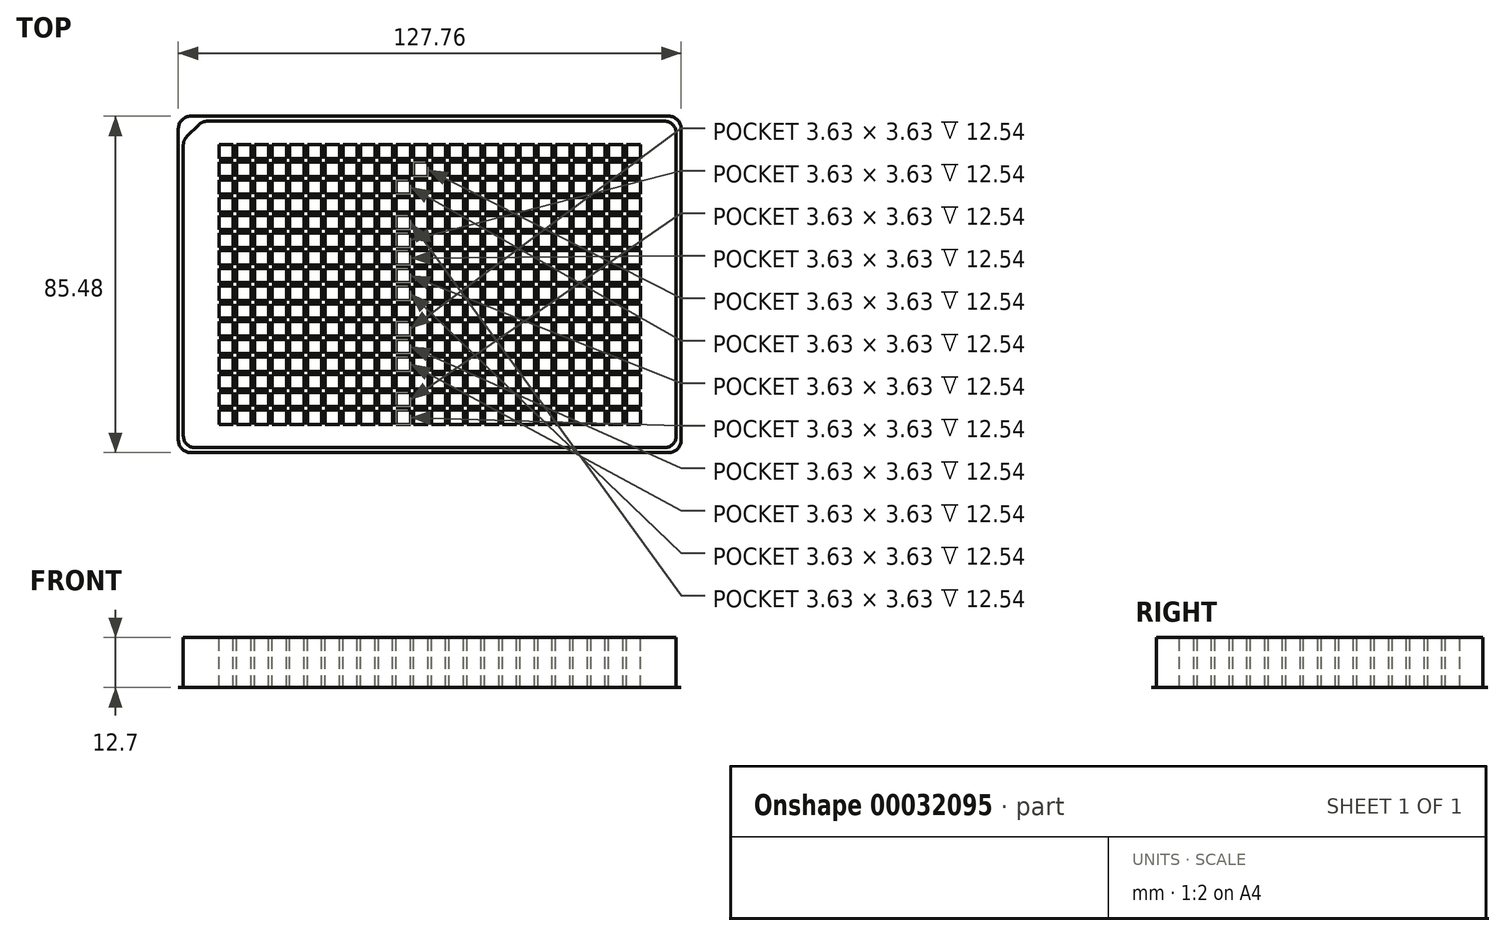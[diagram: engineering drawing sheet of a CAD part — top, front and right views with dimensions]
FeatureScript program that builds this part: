
annotation { "Feature Type Name" : "Feature", "Feature Type Description" : "" }
export const myFeature = defineFeature(function(context is Context, id is Id, definition is map)
    precondition{}
    {
        {
            var Q0;
            Q0=qCreatedBy(makeId("Top.planeOp"),FACE);
            var sketch = newSketch(context, id + "F0", { "sketchPlane" : qUnion([Q0])});
            skLineSegment(sketch, "E0.bottom", {"start": v(-60.7, 42.74) * mm, "end": v(60.7, 42.74) * mm});
            skLineSegment(sketch, "E0.top", {"start": v(-60.7, -42.74) * mm, "end": v(60.7, -42.74) * mm});
            skLineSegment(sketch, "E0.left", {"start": v(-63.88, 39.56) * mm, "end": v(-63.88, -39.56) * mm});
            skLineSegment(sketch, "E0.right", {"start": v(63.88, 39.56) * mm, "end": v(63.88, -39.56) * mm});
            skLineSegment(sketch, "E1", {"start": v(-63.88, 42.74) * mm, "end": v(63.88, -42.74) * mm, "construction": true});
            skPoint(sketch, "E2.visualSharp", {"position": v(-63.88, 42.74) * mm});
            skArc(sketch, "E2.filletArc", {"start": v(-60.7, 42.74) * mm, "mid": v(-62.95, 41.8) * mm, "end": v(-63.88, 39.56) * mm});
            skPoint(sketch, "E3.visualSharp", {"position": v(-63.88, -42.74) * mm});
            skArc(sketch, "E3.filletArc", {"start": v(-63.88, -39.56) * mm, "mid": v(-62.95, -41.8) * mm, "end": v(-60.7, -42.74) * mm});
            skPoint(sketch, "E4.visualSharp", {"position": v(63.88, 42.74) * mm});
            skArc(sketch, "E4.filletArc", {"start": v(63.88, 39.56) * mm, "mid": v(62.95, 41.8) * mm, "end": v(60.7, 42.74) * mm});
            skPoint(sketch, "E5.visualSharp", {"position": v(63.88, -42.74) * mm});
            skArc(sketch, "E5.filletArc", {"start": v(60.7, -42.74) * mm, "mid": v(62.95, -41.8) * mm, "end": v(63.88, -39.56) * mm});
            skSolve(sketch);
        }
        {
            var Q0;
            Q0=makeQuery(id+"F0.imprint","IMPRINT",FACE,{"disambiguationData":[TD([[makeQuery(id+"F0.imprint","IMPRINT",EDGE,{"derivedFrom":sQuery(id+"F0.wireOp",EDGE,"E0.bottom")}),-1.0]])]});
            extrude(context, id + "F1", {"entities" : qUnion([Q0]), "depth" : 3 / 812.8 * mm});
        }
        {
            var Q0;
            Q0=qCreatedBy(makeId("Top.planeOp"),FACE);
            var sketch = newSketch(context, id + "F2", { "sketchPlane" : qUnion([Q0])});
            skLineSegment(sketch, "E6.bottom", {"start": v(59.61, -41.47) * mm, "end": v(-59.6, -41.47) * mm});
            skLineSegment(sketch, "E6.top", {"start": v(59.61, 41.47) * mm, "end": v(-56.54, 41.47) * mm});
            skLineSegment(sketch, "E6.left", {"start": v(62.61, -38.47) * mm, "end": v(62.61, 38.47) * mm});
            skLineSegment(sketch, "E6.right", {"start": v(-62.6, -38.47) * mm, "end": v(-62.61, 35.4) * mm});
            skPoint(sketch, "E7.visualSharp", {"position": v(-62.61, -41.47) * mm});
            skArc(sketch, "E7.filletArc", {"start": v(-62.6, -38.47) * mm, "mid": v(-61.73, -40.6) * mm, "end": v(-59.6, -41.47) * mm});
            skPoint(sketch, "E8.visualSharp", {"position": v(62.6, -41.47) * mm});
            skArc(sketch, "E8.filletArc", {"start": v(59.61, -41.47) * mm, "mid": v(61.73, -40.6) * mm, "end": v(62.61, -38.47) * mm});
            skPoint(sketch, "E9.visualSharp", {"position": v(62.61, 41.47) * mm});
            skArc(sketch, "E9.filletArc", {"start": v(62.61, 38.47) * mm, "mid": v(61.73, 40.6) * mm, "end": v(59.61, 41.47) * mm});
            skLineSegment(sketch, "E10", {"start": v(-61.73, 37.52) * mm, "end": v(-58.66, 40.6) * mm});
            skPoint(sketch, "E11.orphan", {"position": v(-62.61, 41.47) * mm});
            skPoint(sketch, "E12.visualSharp", {"position": v(-62.61, 36.64) * mm});
            skArc(sketch, "E12.filletArc", {"start": v(-61.73, 37.52) * mm, "mid": v(-62.38, 36.55) * mm, "end": v(-62.61, 35.4) * mm});
            skPoint(sketch, "E13.visualSharp", {"position": v(-57.78, 41.47) * mm});
            skArc(sketch, "E13.filletArc", {"start": v(-56.54, 41.47) * mm, "mid": v(-57.69, 41.24) * mm, "end": v(-58.66, 40.6) * mm});
            skSolve(sketch);
        }
        {
            var Q0;
            Q0 = qSketchRegion(id + "F2", true);
            extrude(context, id + "F3", {"entities" : qUnion([Q0]), "operationType" : NewBodyOperationType.ADD, "depth" : 12.7 * mm});
        }
        {
            var Q0;
            Q0=makeQuery(id+"F3.opExtrude","CAP_FACE",FACE,{"disambiguationData":[OSD([sQuery(id+"F2.wireOp",EDGE,"E6.bottom"),sQuery(id+"F2.wireOp",EDGE,"E6.top"),sQuery(id+"F2.wireOp",EDGE,"E6.left"),sQuery(id+"F2.wireOp",EDGE,"E6.right"),sQuery(id+"F2.wireOp",EDGE,"E7.filletArc"),sQuery(id+"F2.wireOp",EDGE,"E8.filletArc"),sQuery(id+"F2.wireOp",EDGE,"E9.filletArc"),sQuery(id+"F2.wireOp",EDGE,"E10"),sQuery(id+"F2.wireOp",EDGE,"E12.filletArc"),sQuery(id+"F2.wireOp",EDGE,"E13.filletArc")])],"isStart":false});
            var sketch = newSketch(context, id + "F4", { "sketchPlane" : qUnion([Q0])});
            skLineSegment(sketch, "E14.rect.bottom", {"start": v(-49.94, 31.93) * mm, "end": v(-53.57, 31.93) * mm});
            skLineSegment(sketch, "E14.rect.top", {"start": v(-49.94, 35.56) * mm, "end": v(-53.57, 35.56) * mm});
            skLineSegment(sketch, "E14.rect.left", {"start": v(-49.94, 31.93) * mm, "end": v(-49.94, 35.56) * mm});
            skLineSegment(sketch, "E14.rect.right", {"start": v(-53.57, 31.93) * mm, "end": v(-53.57, 35.56) * mm});
            skPoint(sketch, "E14.rect.middle", {"position": v(-51.75, 33.75) * mm});
            skLineSegment(sketch, "E15.1.0.0", {"start": v(-49.94, 27.43) * mm, "end": v(-49.94, 31.06) * mm});
            skLineSegment(sketch, "E15.1.0.1", {"start": v(-49.94, 27.43) * mm, "end": v(-53.57, 27.43) * mm});
            skLineSegment(sketch, "E15.1.0.2", {"start": v(-53.57, 27.43) * mm, "end": v(-53.57, 31.06) * mm});
            skLineSegment(sketch, "E15.1.0.3", {"start": v(-49.94, 31.06) * mm, "end": v(-53.57, 31.06) * mm});
            skLineSegment(sketch, "E15.2.0.0", {"start": v(-49.94, 22.93) * mm, "end": v(-49.94, 26.56) * mm});
            skLineSegment(sketch, "E15.2.0.1", {"start": v(-49.94, 22.93) * mm, "end": v(-53.57, 22.93) * mm});
            skLineSegment(sketch, "E15.2.0.2", {"start": v(-53.57, 22.93) * mm, "end": v(-53.57, 26.56) * mm});
            skLineSegment(sketch, "E15.2.0.3", {"start": v(-49.94, 26.56) * mm, "end": v(-53.57, 26.56) * mm});
            skLineSegment(sketch, "E15.direction1", {"start": v(-49.94, 31.93) * mm, "end": v(-49.94, 27.43) * mm, "construction": true});
            skLineSegment(sketch, "E16.0.3.0", {"start": v(-49.94, 18.43) * mm, "end": v(-49.94, 22.06) * mm});
            skLineSegment(sketch, "E16.3.3.0", {"start": v(-49.94, 18.43) * mm, "end": v(-53.57, 18.43) * mm});
            skLineSegment(sketch, "E16.6.3.0", {"start": v(-53.57, 18.43) * mm, "end": v(-53.57, 22.06) * mm});
            skLineSegment(sketch, "E16.9.3.0", {"start": v(-49.94, 22.06) * mm, "end": v(-53.57, 22.06) * mm});
            skLineSegment(sketch, "E16.0.4.0", {"start": v(-49.94, 13.93) * mm, "end": v(-49.94, 17.56) * mm});
            skLineSegment(sketch, "E16.3.4.0", {"start": v(-49.94, 13.93) * mm, "end": v(-53.57, 13.93) * mm});
            skLineSegment(sketch, "E16.6.4.0", {"start": v(-53.57, 13.93) * mm, "end": v(-53.57, 17.56) * mm});
            skLineSegment(sketch, "E16.9.4.0", {"start": v(-49.94, 17.56) * mm, "end": v(-53.57, 17.56) * mm});
            skLineSegment(sketch, "E16.0.5.0", {"start": v(-49.94, 9.43) * mm, "end": v(-49.94, 13.06) * mm});
            skLineSegment(sketch, "E16.3.5.0", {"start": v(-49.94, 9.43) * mm, "end": v(-53.57, 9.43) * mm});
            skLineSegment(sketch, "E16.6.5.0", {"start": v(-53.57, 9.43) * mm, "end": v(-53.57, 13.06) * mm});
            skLineSegment(sketch, "E16.9.5.0", {"start": v(-49.94, 13.06) * mm, "end": v(-53.57, 13.06) * mm});
            skLineSegment(sketch, "E16.0.6.0", {"start": v(-49.94, 4.93) * mm, "end": v(-49.94, 8.56) * mm});
            skLineSegment(sketch, "E16.3.6.0", {"start": v(-49.94, 4.93) * mm, "end": v(-53.57, 4.93) * mm});
            skLineSegment(sketch, "E16.6.6.0", {"start": v(-53.57, 4.93) * mm, "end": v(-53.57, 8.56) * mm});
            skLineSegment(sketch, "E16.9.6.0", {"start": v(-49.94, 8.56) * mm, "end": v(-53.57, 8.56) * mm});
            skLineSegment(sketch, "E16.0.7.0", {"start": v(-49.94, 0.43) * mm, "end": v(-49.94, 4.06) * mm});
            skLineSegment(sketch, "E16.3.7.0", {"start": v(-49.94, 0.43) * mm, "end": v(-53.57, 0.43) * mm});
            skLineSegment(sketch, "E16.6.7.0", {"start": v(-53.57, 0.43) * mm, "end": v(-53.57, 4.06) * mm});
            skLineSegment(sketch, "E16.9.7.0", {"start": v(-49.94, 4.06) * mm, "end": v(-53.57, 4.06) * mm});
            skLineSegment(sketch, "E16.0.8.0", {"start": v(-49.94, -4.07) * mm, "end": v(-49.94, -0.44) * mm});
            skLineSegment(sketch, "E16.3.8.0", {"start": v(-49.94, -4.07) * mm, "end": v(-53.57, -4.07) * mm});
            skLineSegment(sketch, "E16.6.8.0", {"start": v(-53.57, -4.07) * mm, "end": v(-53.57, -0.44) * mm});
            skLineSegment(sketch, "E16.9.8.0", {"start": v(-49.94, -0.44) * mm, "end": v(-53.57, -0.44) * mm});
            skLineSegment(sketch, "E16.0.9.0", {"start": v(-49.94, -8.57) * mm, "end": v(-49.94, -4.94) * mm});
            skLineSegment(sketch, "E16.3.9.0", {"start": v(-49.94, -8.57) * mm, "end": v(-53.57, -8.57) * mm});
            skLineSegment(sketch, "E16.6.9.0", {"start": v(-53.57, -8.57) * mm, "end": v(-53.57, -4.94) * mm});
            skLineSegment(sketch, "E16.9.9.0", {"start": v(-49.94, -4.94) * mm, "end": v(-53.57, -4.94) * mm});
            skLineSegment(sketch, "E16.0.10.0", {"start": v(-49.94, -13.07) * mm, "end": v(-49.94, -9.44) * mm});
            skLineSegment(sketch, "E16.3.10.0", {"start": v(-49.94, -13.07) * mm, "end": v(-53.57, -13.07) * mm});
            skLineSegment(sketch, "E16.6.10.0", {"start": v(-53.57, -13.07) * mm, "end": v(-53.57, -9.44) * mm});
            skLineSegment(sketch, "E16.9.10.0", {"start": v(-49.94, -9.44) * mm, "end": v(-53.57, -9.44) * mm});
            skLineSegment(sketch, "E16.0.11.0", {"start": v(-49.94, -17.57) * mm, "end": v(-49.94, -13.94) * mm});
            skLineSegment(sketch, "E16.3.11.0", {"start": v(-49.94, -17.57) * mm, "end": v(-53.57, -17.57) * mm});
            skLineSegment(sketch, "E16.6.11.0", {"start": v(-53.57, -17.57) * mm, "end": v(-53.57, -13.94) * mm});
            skLineSegment(sketch, "E16.9.11.0", {"start": v(-49.94, -13.94) * mm, "end": v(-53.57, -13.94) * mm});
            skLineSegment(sketch, "E16.0.12.0", {"start": v(-49.94, -22.07) * mm, "end": v(-49.94, -18.44) * mm});
            skLineSegment(sketch, "E16.3.12.0", {"start": v(-49.94, -22.07) * mm, "end": v(-53.57, -22.07) * mm});
            skLineSegment(sketch, "E16.6.12.0", {"start": v(-53.57, -22.07) * mm, "end": v(-53.57, -18.44) * mm});
            skLineSegment(sketch, "E16.9.12.0", {"start": v(-49.94, -18.44) * mm, "end": v(-53.57, -18.44) * mm});
            skLineSegment(sketch, "E16.0.13.0", {"start": v(-49.94, -26.57) * mm, "end": v(-49.94, -22.94) * mm});
            skLineSegment(sketch, "E16.3.13.0", {"start": v(-49.94, -26.57) * mm, "end": v(-53.57, -26.57) * mm});
            skLineSegment(sketch, "E16.6.13.0", {"start": v(-53.57, -26.57) * mm, "end": v(-53.57, -22.94) * mm});
            skLineSegment(sketch, "E16.9.13.0", {"start": v(-49.94, -22.94) * mm, "end": v(-53.57, -22.94) * mm});
            skLineSegment(sketch, "E16.0.14.0", {"start": v(-49.94, -31.07) * mm, "end": v(-49.94, -27.44) * mm});
            skLineSegment(sketch, "E16.3.14.0", {"start": v(-49.94, -31.07) * mm, "end": v(-53.57, -31.07) * mm});
            skLineSegment(sketch, "E16.6.14.0", {"start": v(-53.57, -31.07) * mm, "end": v(-53.57, -27.44) * mm});
            skLineSegment(sketch, "E16.9.14.0", {"start": v(-49.94, -27.44) * mm, "end": v(-53.57, -27.44) * mm});
            skLineSegment(sketch, "E16.0.15.0", {"start": v(-49.94, -35.57) * mm, "end": v(-49.94, -31.94) * mm});
            skLineSegment(sketch, "E16.3.15.0", {"start": v(-49.94, -35.57) * mm, "end": v(-53.57, -35.57) * mm});
            skLineSegment(sketch, "E16.6.15.0", {"start": v(-53.57, -35.57) * mm, "end": v(-53.57, -31.94) * mm});
            skLineSegment(sketch, "E16.9.15.0", {"start": v(-49.94, -31.94) * mm, "end": v(-53.57, -31.94) * mm});
            skLineSegment(sketch, "E17.1.0.0", {"start": v(-49.07, 27.43) * mm, "end": v(-49.07, 31.06) * mm});
            skLineSegment(sketch, "E17.1.0.1", {"start": v(-45.44, 27.43) * mm, "end": v(-45.44, 31.06) * mm});
            skLineSegment(sketch, "E17.1.0.2", {"start": v(-45.44, -13.07) * mm, "end": v(-45.44, -9.44) * mm});
            skLineSegment(sketch, "E17.1.0.3", {"start": v(-49.07, 9.43) * mm, "end": v(-49.07, 13.06) * mm});
            skLineSegment(sketch, "E17.1.0.4", {"start": v(-49.07, -13.07) * mm, "end": v(-49.07, -9.44) * mm});
            skLineSegment(sketch, "E17.1.0.5", {"start": v(-49.07, -31.07) * mm, "end": v(-49.07, -27.44) * mm});
            skPoint(sketch, "E17.1.0.6", {"position": v(-47.25, 33.75) * mm});
            skLineSegment(sketch, "E17.1.0.7", {"start": v(-45.44, 9.43) * mm, "end": v(-45.44, 13.06) * mm});
            skLineSegment(sketch, "E17.1.0.8", {"start": v(-45.44, -31.07) * mm, "end": v(-45.44, -27.44) * mm});
            skLineSegment(sketch, "E17.1.0.9", {"start": v(-45.44, 31.93) * mm, "end": v(-45.44, 27.43) * mm, "construction": true});
            skLineSegment(sketch, "E17.1.0.10", {"start": v(-45.44, 31.06) * mm, "end": v(-49.07, 31.06) * mm});
            skLineSegment(sketch, "E17.1.0.11", {"start": v(-45.44, 4.93) * mm, "end": v(-49.07, 4.93) * mm});
            skLineSegment(sketch, "E17.1.0.12", {"start": v(-45.44, -13.07) * mm, "end": v(-49.07, -13.07) * mm});
            skLineSegment(sketch, "E17.1.0.13", {"start": v(-45.44, -31.07) * mm, "end": v(-49.07, -31.07) * mm});
            skLineSegment(sketch, "E17.1.0.14", {"start": v(-49.07, 31.93) * mm, "end": v(-49.07, 35.56) * mm});
            skLineSegment(sketch, "E17.1.0.15", {"start": v(-45.44, 31.93) * mm, "end": v(-45.44, 35.56) * mm});
            skLineSegment(sketch, "E17.1.0.16", {"start": v(-45.44, 31.93) * mm, "end": v(-49.07, 31.93) * mm});
            skLineSegment(sketch, "E17.1.0.17", {"start": v(-49.07, 18.43) * mm, "end": v(-49.07, 22.06) * mm});
            skLineSegment(sketch, "E17.1.0.18", {"start": v(-45.44, 13.06) * mm, "end": v(-49.07, 13.06) * mm});
            skLineSegment(sketch, "E17.1.0.19", {"start": v(-45.44, -4.94) * mm, "end": v(-49.07, -4.94) * mm});
            skLineSegment(sketch, "E17.1.0.20", {"start": v(-45.44, -22.94) * mm, "end": v(-49.07, -22.94) * mm});
            skLineSegment(sketch, "E17.1.0.21", {"start": v(-45.44, -26.57) * mm, "end": v(-45.44, -22.94) * mm});
            skLineSegment(sketch, "E17.1.0.22", {"start": v(-49.07, -8.57) * mm, "end": v(-49.07, -4.94) * mm});
            skLineSegment(sketch, "E17.1.0.23", {"start": v(-49.07, -26.57) * mm, "end": v(-49.07, -22.94) * mm});
            skLineSegment(sketch, "E17.1.0.24", {"start": v(-45.44, 17.56) * mm, "end": v(-49.07, 17.56) * mm});
            skLineSegment(sketch, "E17.1.0.25", {"start": v(-45.44, -0.44) * mm, "end": v(-49.07, -0.44) * mm});
            skLineSegment(sketch, "E17.1.0.26", {"start": v(-45.44, -9.44) * mm, "end": v(-49.07, -9.44) * mm});
            skLineSegment(sketch, "E17.1.0.27", {"start": v(-49.07, -22.07) * mm, "end": v(-49.07, -18.44) * mm});
            skLineSegment(sketch, "E17.1.0.28", {"start": v(-49.07, 13.93) * mm, "end": v(-49.07, 17.56) * mm});
            skLineSegment(sketch, "E17.1.0.29", {"start": v(-49.07, -4.07) * mm, "end": v(-49.07, -0.44) * mm});
            skLineSegment(sketch, "E17.1.0.30", {"start": v(-45.44, 13.93) * mm, "end": v(-49.07, 13.93) * mm});
            skLineSegment(sketch, "E17.1.0.31", {"start": v(-45.44, -4.07) * mm, "end": v(-49.07, -4.07) * mm});
            skLineSegment(sketch, "E17.1.0.32", {"start": v(-45.44, -17.57) * mm, "end": v(-49.07, -17.57) * mm});
            skLineSegment(sketch, "E17.1.0.33", {"start": v(-45.44, -27.44) * mm, "end": v(-49.07, -27.44) * mm});
            skLineSegment(sketch, "E17.1.0.34", {"start": v(-45.44, -35.57) * mm, "end": v(-49.07, -35.57) * mm});
            skLineSegment(sketch, "E17.1.0.35", {"start": v(-45.44, 0.43) * mm, "end": v(-49.07, 0.43) * mm});
            skLineSegment(sketch, "E17.1.0.36", {"start": v(-45.44, 13.93) * mm, "end": v(-45.44, 17.56) * mm});
            skLineSegment(sketch, "E17.1.0.37", {"start": v(-45.44, -22.07) * mm, "end": v(-45.44, -18.44) * mm});
            skLineSegment(sketch, "E17.1.0.38", {"start": v(-45.44, -17.57) * mm, "end": v(-45.44, -13.94) * mm});
            skLineSegment(sketch, "E17.1.0.39", {"start": v(-49.07, 4.93) * mm, "end": v(-49.07, 8.56) * mm});
            skLineSegment(sketch, "E17.1.0.40", {"start": v(-45.44, 26.56) * mm, "end": v(-49.07, 26.56) * mm});
            skLineSegment(sketch, "E17.1.0.41", {"start": v(-45.44, 9.43) * mm, "end": v(-49.07, 9.43) * mm});
            skLineSegment(sketch, "E17.1.0.42", {"start": v(-49.07, 22.93) * mm, "end": v(-49.07, 26.56) * mm});
            skLineSegment(sketch, "E17.1.0.43", {"start": v(-45.44, -13.94) * mm, "end": v(-49.07, -13.94) * mm});
            skLineSegment(sketch, "E17.1.0.44", {"start": v(-45.44, -31.94) * mm, "end": v(-49.07, -31.94) * mm});
            skLineSegment(sketch, "E17.1.0.45", {"start": v(-45.44, 22.06) * mm, "end": v(-49.07, 22.06) * mm});
            skLineSegment(sketch, "E17.1.0.46", {"start": v(-45.44, 4.06) * mm, "end": v(-49.07, 4.06) * mm});
            skLineSegment(sketch, "E17.1.0.47", {"start": v(-49.07, 0.43) * mm, "end": v(-49.07, 4.06) * mm});
            skLineSegment(sketch, "E17.1.0.48", {"start": v(-49.07, -35.57) * mm, "end": v(-49.07, -31.94) * mm});
            skLineSegment(sketch, "E17.1.0.49", {"start": v(-45.44, 0.43) * mm, "end": v(-45.44, 4.06) * mm});
            skLineSegment(sketch, "E17.1.0.50", {"start": v(-45.44, -26.57) * mm, "end": v(-49.07, -26.57) * mm});
            skLineSegment(sketch, "E17.1.0.51", {"start": v(-45.44, -35.57) * mm, "end": v(-45.44, -31.94) * mm});
            skLineSegment(sketch, "E17.1.0.52", {"start": v(-45.44, -4.07) * mm, "end": v(-45.44, -0.44) * mm});
            skLineSegment(sketch, "E17.1.0.53", {"start": v(-45.44, -22.07) * mm, "end": v(-49.07, -22.07) * mm});
            skLineSegment(sketch, "E17.1.0.54", {"start": v(-45.44, 18.43) * mm, "end": v(-45.44, 22.06) * mm});
            skLineSegment(sketch, "E17.1.0.55", {"start": v(-45.44, -18.44) * mm, "end": v(-49.07, -18.44) * mm});
            skLineSegment(sketch, "E17.1.0.56", {"start": v(-45.44, -8.57) * mm, "end": v(-45.44, -4.94) * mm});
            skLineSegment(sketch, "E17.1.0.57", {"start": v(-45.44, 18.43) * mm, "end": v(-49.07, 18.43) * mm});
            skLineSegment(sketch, "E17.1.0.58", {"start": v(-45.44, 35.56) * mm, "end": v(-49.07, 35.56) * mm});
            skLineSegment(sketch, "E17.1.0.59", {"start": v(-45.44, 4.93) * mm, "end": v(-45.44, 8.56) * mm});
            skLineSegment(sketch, "E17.1.0.60", {"start": v(-45.44, 27.43) * mm, "end": v(-49.07, 27.43) * mm});
            skLineSegment(sketch, "E17.1.0.61", {"start": v(-45.44, -8.57) * mm, "end": v(-49.07, -8.57) * mm});
            skLineSegment(sketch, "E17.1.0.62", {"start": v(-45.44, 8.56) * mm, "end": v(-49.07, 8.56) * mm});
            skLineSegment(sketch, "E17.1.0.63", {"start": v(-49.07, -17.57) * mm, "end": v(-49.07, -13.94) * mm});
            skLineSegment(sketch, "E17.1.0.64", {"start": v(-45.44, 22.93) * mm, "end": v(-49.07, 22.93) * mm});
            skLineSegment(sketch, "E17.1.0.65", {"start": v(-45.44, 22.93) * mm, "end": v(-45.44, 26.56) * mm});
            skLineSegment(sketch, "E17.2.0.0", {"start": v(-44.57, 27.43) * mm, "end": v(-44.57, 31.06) * mm});
            skLineSegment(sketch, "E17.2.0.1", {"start": v(-40.94, 27.43) * mm, "end": v(-40.94, 31.06) * mm});
            skLineSegment(sketch, "E17.2.0.2", {"start": v(-40.94, -13.07) * mm, "end": v(-40.94, -9.44) * mm});
            skLineSegment(sketch, "E17.2.0.3", {"start": v(-44.57, 9.43) * mm, "end": v(-44.57, 13.06) * mm});
            skLineSegment(sketch, "E17.2.0.4", {"start": v(-44.56, -13.07) * mm, "end": v(-44.56, -9.44) * mm});
            skLineSegment(sketch, "E17.2.0.5", {"start": v(-44.56, -31.07) * mm, "end": v(-44.56, -27.44) * mm});
            skPoint(sketch, "E17.2.0.6", {"position": v(-42.75, 33.75) * mm});
            skLineSegment(sketch, "E17.2.0.7", {"start": v(-40.94, 9.43) * mm, "end": v(-40.94, 13.06) * mm});
            skLineSegment(sketch, "E17.2.0.8", {"start": v(-40.94, -31.07) * mm, "end": v(-40.94, -27.44) * mm});
            skLineSegment(sketch, "E17.2.0.9", {"start": v(-40.94, 31.93) * mm, "end": v(-40.94, 27.43) * mm, "construction": true});
            skLineSegment(sketch, "E17.2.0.10", {"start": v(-40.94, 31.06) * mm, "end": v(-44.57, 31.06) * mm});
            skLineSegment(sketch, "E17.2.0.11", {"start": v(-40.94, 4.93) * mm, "end": v(-44.57, 4.93) * mm});
            skLineSegment(sketch, "E17.2.0.12", {"start": v(-40.94, -13.07) * mm, "end": v(-44.57, -13.07) * mm});
            skLineSegment(sketch, "E17.2.0.13", {"start": v(-40.94, -31.07) * mm, "end": v(-44.57, -31.07) * mm});
            skLineSegment(sketch, "E17.2.0.14", {"start": v(-44.57, 31.93) * mm, "end": v(-44.57, 35.56) * mm});
            skLineSegment(sketch, "E17.2.0.15", {"start": v(-40.94, 31.93) * mm, "end": v(-40.94, 35.56) * mm});
            skLineSegment(sketch, "E17.2.0.16", {"start": v(-40.94, 31.93) * mm, "end": v(-44.57, 31.93) * mm});
            skLineSegment(sketch, "E17.2.0.17", {"start": v(-44.57, 18.43) * mm, "end": v(-44.57, 22.06) * mm});
            skLineSegment(sketch, "E17.2.0.18", {"start": v(-40.94, 13.06) * mm, "end": v(-44.57, 13.06) * mm});
            skLineSegment(sketch, "E17.2.0.19", {"start": v(-40.94, -4.94) * mm, "end": v(-44.57, -4.94) * mm});
            skLineSegment(sketch, "E17.2.0.20", {"start": v(-40.94, -22.94) * mm, "end": v(-44.57, -22.94) * mm});
            skLineSegment(sketch, "E17.2.0.21", {"start": v(-40.94, -26.57) * mm, "end": v(-40.94, -22.94) * mm});
            skLineSegment(sketch, "E17.2.0.22", {"start": v(-44.56, -8.57) * mm, "end": v(-44.56, -4.94) * mm});
            skLineSegment(sketch, "E17.2.0.23", {"start": v(-44.56, -26.57) * mm, "end": v(-44.56, -22.94) * mm});
            skLineSegment(sketch, "E17.2.0.24", {"start": v(-40.94, 17.56) * mm, "end": v(-44.57, 17.56) * mm});
            skLineSegment(sketch, "E17.2.0.25", {"start": v(-40.94, -0.44) * mm, "end": v(-44.57, -0.44) * mm});
            skLineSegment(sketch, "E17.2.0.26", {"start": v(-40.94, -9.44) * mm, "end": v(-44.57, -9.44) * mm});
            skLineSegment(sketch, "E17.2.0.27", {"start": v(-44.56, -22.07) * mm, "end": v(-44.56, -18.44) * mm});
            skLineSegment(sketch, "E17.2.0.28", {"start": v(-44.57, 13.93) * mm, "end": v(-44.57, 17.56) * mm});
            skLineSegment(sketch, "E17.2.0.29", {"start": v(-44.56, -4.07) * mm, "end": v(-44.56, -0.44) * mm});
            skLineSegment(sketch, "E17.2.0.30", {"start": v(-40.94, 13.93) * mm, "end": v(-44.57, 13.93) * mm});
            skLineSegment(sketch, "E17.2.0.31", {"start": v(-40.94, -4.07) * mm, "end": v(-44.57, -4.07) * mm});
            skLineSegment(sketch, "E17.2.0.32", {"start": v(-40.94, -17.57) * mm, "end": v(-44.57, -17.57) * mm});
            skLineSegment(sketch, "E17.2.0.33", {"start": v(-40.94, -27.44) * mm, "end": v(-44.57, -27.44) * mm});
            skLineSegment(sketch, "E17.2.0.34", {"start": v(-40.94, -35.57) * mm, "end": v(-44.57, -35.57) * mm});
            skLineSegment(sketch, "E17.2.0.35", {"start": v(-40.94, 0.43) * mm, "end": v(-44.57, 0.43) * mm});
            skLineSegment(sketch, "E17.2.0.36", {"start": v(-40.94, 13.93) * mm, "end": v(-40.94, 17.56) * mm});
            skLineSegment(sketch, "E17.2.0.37", {"start": v(-40.94, -22.07) * mm, "end": v(-40.94, -18.44) * mm});
            skLineSegment(sketch, "E17.2.0.38", {"start": v(-40.94, -17.57) * mm, "end": v(-40.94, -13.94) * mm});
            skLineSegment(sketch, "E17.2.0.39", {"start": v(-44.57, 4.93) * mm, "end": v(-44.57, 8.56) * mm});
            skLineSegment(sketch, "E17.2.0.40", {"start": v(-40.94, 26.56) * mm, "end": v(-44.57, 26.56) * mm});
            skLineSegment(sketch, "E17.2.0.41", {"start": v(-40.94, 9.43) * mm, "end": v(-44.57, 9.43) * mm});
            skLineSegment(sketch, "E17.2.0.42", {"start": v(-44.57, 22.93) * mm, "end": v(-44.57, 26.56) * mm});
            skLineSegment(sketch, "E17.2.0.43", {"start": v(-40.94, -13.94) * mm, "end": v(-44.57, -13.94) * mm});
            skLineSegment(sketch, "E17.2.0.44", {"start": v(-40.94, -31.94) * mm, "end": v(-44.57, -31.94) * mm});
            skLineSegment(sketch, "E17.2.0.45", {"start": v(-40.94, 22.06) * mm, "end": v(-44.57, 22.06) * mm});
            skLineSegment(sketch, "E17.2.0.46", {"start": v(-40.94, 4.06) * mm, "end": v(-44.57, 4.06) * mm});
            skLineSegment(sketch, "E17.2.0.47", {"start": v(-44.56, 0.43) * mm, "end": v(-44.56, 4.06) * mm});
            skLineSegment(sketch, "E17.2.0.48", {"start": v(-44.56, -35.57) * mm, "end": v(-44.56, -31.94) * mm});
            skLineSegment(sketch, "E17.2.0.49", {"start": v(-40.94, 0.43) * mm, "end": v(-40.94, 4.06) * mm});
            skLineSegment(sketch, "E17.2.0.50", {"start": v(-40.94, -26.57) * mm, "end": v(-44.57, -26.57) * mm});
            skLineSegment(sketch, "E17.2.0.51", {"start": v(-40.94, -35.57) * mm, "end": v(-40.94, -31.94) * mm});
            skLineSegment(sketch, "E17.2.0.52", {"start": v(-40.94, -4.07) * mm, "end": v(-40.94, -0.44) * mm});
            skLineSegment(sketch, "E17.2.0.53", {"start": v(-40.94, -22.07) * mm, "end": v(-44.57, -22.07) * mm});
            skLineSegment(sketch, "E17.2.0.54", {"start": v(-40.94, 18.43) * mm, "end": v(-40.94, 22.06) * mm});
            skLineSegment(sketch, "E17.2.0.55", {"start": v(-40.94, -18.44) * mm, "end": v(-44.57, -18.44) * mm});
            skLineSegment(sketch, "E17.2.0.56", {"start": v(-40.94, -8.57) * mm, "end": v(-40.94, -4.94) * mm});
            skLineSegment(sketch, "E17.2.0.57", {"start": v(-40.94, 18.43) * mm, "end": v(-44.57, 18.43) * mm});
            skLineSegment(sketch, "E17.2.0.58", {"start": v(-40.94, 35.56) * mm, "end": v(-44.57, 35.56) * mm});
            skLineSegment(sketch, "E17.2.0.59", {"start": v(-40.94, 4.93) * mm, "end": v(-40.94, 8.56) * mm});
            skLineSegment(sketch, "E17.2.0.60", {"start": v(-40.94, 27.43) * mm, "end": v(-44.57, 27.43) * mm});
            skLineSegment(sketch, "E17.2.0.61", {"start": v(-40.94, -8.57) * mm, "end": v(-44.57, -8.57) * mm});
            skLineSegment(sketch, "E17.2.0.62", {"start": v(-40.94, 8.56) * mm, "end": v(-44.57, 8.56) * mm});
            skLineSegment(sketch, "E17.2.0.63", {"start": v(-44.56, -17.57) * mm, "end": v(-44.56, -13.94) * mm});
            skLineSegment(sketch, "E17.2.0.64", {"start": v(-40.94, 22.93) * mm, "end": v(-44.57, 22.93) * mm});
            skLineSegment(sketch, "E17.2.0.65", {"start": v(-40.94, 22.93) * mm, "end": v(-40.94, 26.56) * mm});
            skLineSegment(sketch, "E17.3.0.0", {"start": v(-40.07, 27.43) * mm, "end": v(-40.07, 31.06) * mm});
            skLineSegment(sketch, "E17.3.0.1", {"start": v(-36.43, 27.43) * mm, "end": v(-36.43, 31.06) * mm});
            skLineSegment(sketch, "E17.3.0.2", {"start": v(-36.43, -13.07) * mm, "end": v(-36.43, -9.44) * mm});
            skLineSegment(sketch, "E17.3.0.3", {"start": v(-40.07, 9.43) * mm, "end": v(-40.07, 13.06) * mm});
            skLineSegment(sketch, "E17.3.0.4", {"start": v(-40.06, -13.07) * mm, "end": v(-40.06, -9.44) * mm});
            skLineSegment(sketch, "E17.3.0.5", {"start": v(-40.06, -31.07) * mm, "end": v(-40.06, -27.44) * mm});
            skPoint(sketch, "E17.3.0.6", {"position": v(-38.25, 33.75) * mm});
            skLineSegment(sketch, "E17.3.0.7", {"start": v(-36.44, 9.43) * mm, "end": v(-36.44, 13.06) * mm});
            skLineSegment(sketch, "E17.3.0.8", {"start": v(-36.43, -31.07) * mm, "end": v(-36.43, -27.44) * mm});
            skLineSegment(sketch, "E17.3.0.9", {"start": v(-36.44, 31.93) * mm, "end": v(-36.44, 27.43) * mm, "construction": true});
            skLineSegment(sketch, "E17.3.0.10", {"start": v(-36.44, 31.06) * mm, "end": v(-40.07, 31.06) * mm});
            skLineSegment(sketch, "E17.3.0.11", {"start": v(-36.44, 4.93) * mm, "end": v(-40.07, 4.93) * mm});
            skLineSegment(sketch, "E17.3.0.12", {"start": v(-36.44, -13.07) * mm, "end": v(-40.07, -13.07) * mm});
            skLineSegment(sketch, "E17.3.0.13", {"start": v(-36.44, -31.07) * mm, "end": v(-40.07, -31.07) * mm});
            skLineSegment(sketch, "E17.3.0.14", {"start": v(-40.07, 31.93) * mm, "end": v(-40.07, 35.56) * mm});
            skLineSegment(sketch, "E17.3.0.15", {"start": v(-36.44, 31.93) * mm, "end": v(-36.44, 35.56) * mm});
            skLineSegment(sketch, "E17.3.0.16", {"start": v(-36.44, 31.93) * mm, "end": v(-40.07, 31.93) * mm});
            skLineSegment(sketch, "E17.3.0.17", {"start": v(-40.07, 18.43) * mm, "end": v(-40.07, 22.06) * mm});
            skLineSegment(sketch, "E17.3.0.18", {"start": v(-36.44, 13.06) * mm, "end": v(-40.07, 13.06) * mm});
            skLineSegment(sketch, "E17.3.0.19", {"start": v(-36.44, -4.94) * mm, "end": v(-40.07, -4.94) * mm});
            skLineSegment(sketch, "E17.3.0.20", {"start": v(-36.44, -22.94) * mm, "end": v(-40.07, -22.94) * mm});
            skLineSegment(sketch, "E17.3.0.21", {"start": v(-36.43, -26.57) * mm, "end": v(-36.43, -22.94) * mm});
            skLineSegment(sketch, "E17.3.0.22", {"start": v(-40.06, -8.57) * mm, "end": v(-40.06, -4.94) * mm});
            skLineSegment(sketch, "E17.3.0.23", {"start": v(-40.06, -26.57) * mm, "end": v(-40.06, -22.94) * mm});
            skLineSegment(sketch, "E17.3.0.24", {"start": v(-36.44, 17.56) * mm, "end": v(-40.07, 17.56) * mm});
            skLineSegment(sketch, "E17.3.0.25", {"start": v(-36.44, -0.44) * mm, "end": v(-40.07, -0.44) * mm});
            skLineSegment(sketch, "E17.3.0.26", {"start": v(-36.44, -9.44) * mm, "end": v(-40.07, -9.44) * mm});
            skLineSegment(sketch, "E17.3.0.27", {"start": v(-40.06, -22.07) * mm, "end": v(-40.06, -18.44) * mm});
            skLineSegment(sketch, "E17.3.0.28", {"start": v(-40.07, 13.93) * mm, "end": v(-40.07, 17.56) * mm});
            skLineSegment(sketch, "E17.3.0.29", {"start": v(-40.06, -4.07) * mm, "end": v(-40.06, -0.44) * mm});
            skLineSegment(sketch, "E17.3.0.30", {"start": v(-36.44, 13.93) * mm, "end": v(-40.07, 13.93) * mm});
            skLineSegment(sketch, "E17.3.0.31", {"start": v(-36.44, -4.07) * mm, "end": v(-40.07, -4.07) * mm});
            skLineSegment(sketch, "E17.3.0.32", {"start": v(-36.44, -17.57) * mm, "end": v(-40.07, -17.57) * mm});
            skLineSegment(sketch, "E17.3.0.33", {"start": v(-36.44, -27.44) * mm, "end": v(-40.07, -27.44) * mm});
            skLineSegment(sketch, "E17.3.0.34", {"start": v(-36.44, -35.57) * mm, "end": v(-40.07, -35.57) * mm});
            skLineSegment(sketch, "E17.3.0.35", {"start": v(-36.44, 0.43) * mm, "end": v(-40.07, 0.43) * mm});
            skLineSegment(sketch, "E17.3.0.36", {"start": v(-36.44, 13.93) * mm, "end": v(-36.44, 17.56) * mm});
            skLineSegment(sketch, "E17.3.0.37", {"start": v(-36.43, -22.07) * mm, "end": v(-36.43, -18.44) * mm});
            skLineSegment(sketch, "E17.3.0.38", {"start": v(-36.43, -17.57) * mm, "end": v(-36.43, -13.94) * mm});
            skLineSegment(sketch, "E17.3.0.39", {"start": v(-40.07, 4.93) * mm, "end": v(-40.07, 8.56) * mm});
            skLineSegment(sketch, "E17.3.0.40", {"start": v(-36.44, 26.56) * mm, "end": v(-40.07, 26.56) * mm});
            skLineSegment(sketch, "E17.3.0.41", {"start": v(-36.44, 9.43) * mm, "end": v(-40.07, 9.43) * mm});
            skLineSegment(sketch, "E17.3.0.42", {"start": v(-40.07, 22.93) * mm, "end": v(-40.07, 26.56) * mm});
            skLineSegment(sketch, "E17.3.0.43", {"start": v(-36.44, -13.94) * mm, "end": v(-40.07, -13.94) * mm});
            skLineSegment(sketch, "E17.3.0.44", {"start": v(-36.44, -31.94) * mm, "end": v(-40.07, -31.94) * mm});
            skLineSegment(sketch, "E17.3.0.45", {"start": v(-36.44, 22.06) * mm, "end": v(-40.07, 22.06) * mm});
            skLineSegment(sketch, "E17.3.0.46", {"start": v(-36.44, 4.06) * mm, "end": v(-40.07, 4.06) * mm});
            skLineSegment(sketch, "E17.3.0.47", {"start": v(-40.06, 0.43) * mm, "end": v(-40.06, 4.06) * mm});
            skLineSegment(sketch, "E17.3.0.48", {"start": v(-40.06, -35.57) * mm, "end": v(-40.06, -31.94) * mm});
            skLineSegment(sketch, "E17.3.0.49", {"start": v(-36.43, 0.43) * mm, "end": v(-36.43, 4.06) * mm});
            skLineSegment(sketch, "E17.3.0.50", {"start": v(-36.44, -26.57) * mm, "end": v(-40.07, -26.57) * mm});
            skLineSegment(sketch, "E17.3.0.51", {"start": v(-36.43, -35.57) * mm, "end": v(-36.43, -31.94) * mm});
            skLineSegment(sketch, "E17.3.0.52", {"start": v(-36.43, -4.07) * mm, "end": v(-36.43, -0.44) * mm});
            skLineSegment(sketch, "E17.3.0.53", {"start": v(-36.44, -22.07) * mm, "end": v(-40.07, -22.07) * mm});
            skLineSegment(sketch, "E17.3.0.54", {"start": v(-36.44, 18.43) * mm, "end": v(-36.44, 22.06) * mm});
            skLineSegment(sketch, "E17.3.0.55", {"start": v(-36.44, -18.44) * mm, "end": v(-40.07, -18.44) * mm});
            skLineSegment(sketch, "E17.3.0.56", {"start": v(-36.43, -8.57) * mm, "end": v(-36.43, -4.94) * mm});
            skLineSegment(sketch, "E17.3.0.57", {"start": v(-36.44, 18.43) * mm, "end": v(-40.07, 18.43) * mm});
            skLineSegment(sketch, "E17.3.0.58", {"start": v(-36.44, 35.56) * mm, "end": v(-40.07, 35.56) * mm});
            skLineSegment(sketch, "E17.3.0.59", {"start": v(-36.44, 4.93) * mm, "end": v(-36.44, 8.56) * mm});
            skLineSegment(sketch, "E17.3.0.60", {"start": v(-36.44, 27.43) * mm, "end": v(-40.07, 27.43) * mm});
            skLineSegment(sketch, "E17.3.0.61", {"start": v(-36.44, -8.57) * mm, "end": v(-40.07, -8.57) * mm});
            skLineSegment(sketch, "E17.3.0.62", {"start": v(-36.44, 8.56) * mm, "end": v(-40.07, 8.56) * mm});
            skLineSegment(sketch, "E17.3.0.63", {"start": v(-40.06, -17.57) * mm, "end": v(-40.06, -13.94) * mm});
            skLineSegment(sketch, "E17.3.0.64", {"start": v(-36.44, 22.93) * mm, "end": v(-40.07, 22.93) * mm});
            skLineSegment(sketch, "E17.3.0.65", {"start": v(-36.44, 22.93) * mm, "end": v(-36.44, 26.56) * mm});
            skLineSegment(sketch, "E17.4.0.0", {"start": v(-35.56, 27.43) * mm, "end": v(-35.56, 31.06) * mm});
            skLineSegment(sketch, "E17.4.0.1", {"start": v(-31.93, 27.43) * mm, "end": v(-31.93, 31.06) * mm});
            skLineSegment(sketch, "E17.4.0.2", {"start": v(-31.93, -13.07) * mm, "end": v(-31.93, -9.44) * mm});
            skLineSegment(sketch, "E17.4.0.3", {"start": v(-35.56, 9.43) * mm, "end": v(-35.56, 13.06) * mm});
            skLineSegment(sketch, "E17.4.0.4", {"start": v(-35.56, -13.07) * mm, "end": v(-35.56, -9.44) * mm});
            skLineSegment(sketch, "E17.4.0.5", {"start": v(-35.56, -31.07) * mm, "end": v(-35.56, -27.44) * mm});
            skPoint(sketch, "E17.4.0.6", {"position": v(-33.75, 33.75) * mm});
            skLineSegment(sketch, "E17.4.0.7", {"start": v(-31.93, 9.43) * mm, "end": v(-31.93, 13.06) * mm});
            skLineSegment(sketch, "E17.4.0.8", {"start": v(-31.93, -31.07) * mm, "end": v(-31.93, -27.44) * mm});
            skLineSegment(sketch, "E17.4.0.9", {"start": v(-31.93, 31.93) * mm, "end": v(-31.93, 27.43) * mm, "construction": true});
            skLineSegment(sketch, "E17.4.0.10", {"start": v(-31.93, 31.06) * mm, "end": v(-35.56, 31.06) * mm});
            skLineSegment(sketch, "E17.4.0.11", {"start": v(-31.94, 4.93) * mm, "end": v(-35.57, 4.93) * mm});
            skLineSegment(sketch, "E17.4.0.12", {"start": v(-31.93, -13.07) * mm, "end": v(-35.56, -13.07) * mm});
            skLineSegment(sketch, "E17.4.0.13", {"start": v(-31.93, -31.07) * mm, "end": v(-35.56, -31.07) * mm});
            skLineSegment(sketch, "E17.4.0.14", {"start": v(-35.56, 31.93) * mm, "end": v(-35.56, 35.56) * mm});
            skLineSegment(sketch, "E17.4.0.15", {"start": v(-31.93, 31.93) * mm, "end": v(-31.93, 35.56) * mm});
            skLineSegment(sketch, "E17.4.0.16", {"start": v(-31.94, 31.93) * mm, "end": v(-35.57, 31.93) * mm});
            skLineSegment(sketch, "E17.4.0.17", {"start": v(-35.56, 18.43) * mm, "end": v(-35.56, 22.06) * mm});
            skLineSegment(sketch, "E17.4.0.18", {"start": v(-31.94, 13.06) * mm, "end": v(-35.57, 13.06) * mm});
            skLineSegment(sketch, "E17.4.0.19", {"start": v(-31.93, -4.94) * mm, "end": v(-35.56, -4.94) * mm});
            skLineSegment(sketch, "E17.4.0.20", {"start": v(-31.93, -22.94) * mm, "end": v(-35.56, -22.94) * mm});
            skLineSegment(sketch, "E17.4.0.21", {"start": v(-31.93, -26.57) * mm, "end": v(-31.93, -22.94) * mm});
            skLineSegment(sketch, "E17.4.0.22", {"start": v(-35.56, -8.57) * mm, "end": v(-35.56, -4.94) * mm});
            skLineSegment(sketch, "E17.4.0.23", {"start": v(-35.56, -26.57) * mm, "end": v(-35.56, -22.94) * mm});
            skLineSegment(sketch, "E17.4.0.24", {"start": v(-31.94, 17.56) * mm, "end": v(-35.57, 17.56) * mm});
            skLineSegment(sketch, "E17.4.0.25", {"start": v(-31.93, -0.44) * mm, "end": v(-35.56, -0.44) * mm});
            skLineSegment(sketch, "E17.4.0.26", {"start": v(-31.93, -9.44) * mm, "end": v(-35.56, -9.44) * mm});
            skLineSegment(sketch, "E17.4.0.27", {"start": v(-35.56, -22.07) * mm, "end": v(-35.56, -18.44) * mm});
            skLineSegment(sketch, "E17.4.0.28", {"start": v(-35.56, 13.93) * mm, "end": v(-35.56, 17.56) * mm});
            skLineSegment(sketch, "E17.4.0.29", {"start": v(-35.56, -4.07) * mm, "end": v(-35.56, -0.44) * mm});
            skLineSegment(sketch, "E17.4.0.30", {"start": v(-31.94, 13.93) * mm, "end": v(-35.57, 13.93) * mm});
            skLineSegment(sketch, "E17.4.0.31", {"start": v(-31.93, -4.07) * mm, "end": v(-35.56, -4.07) * mm});
            skLineSegment(sketch, "E17.4.0.32", {"start": v(-31.93, -17.57) * mm, "end": v(-35.56, -17.57) * mm});
            skLineSegment(sketch, "E17.4.0.33", {"start": v(-31.93, -27.44) * mm, "end": v(-35.56, -27.44) * mm});
            skLineSegment(sketch, "E17.4.0.34", {"start": v(-31.93, -35.57) * mm, "end": v(-35.56, -35.57) * mm});
            skLineSegment(sketch, "E17.4.0.35", {"start": v(-31.93, 0.43) * mm, "end": v(-35.56, 0.43) * mm});
            skLineSegment(sketch, "E17.4.0.36", {"start": v(-31.93, 13.93) * mm, "end": v(-31.93, 17.56) * mm});
            skLineSegment(sketch, "E17.4.0.37", {"start": v(-31.93, -22.07) * mm, "end": v(-31.93, -18.44) * mm});
            skLineSegment(sketch, "E17.4.0.38", {"start": v(-31.93, -17.57) * mm, "end": v(-31.93, -13.94) * mm});
            skLineSegment(sketch, "E17.4.0.39", {"start": v(-35.56, 4.93) * mm, "end": v(-35.56, 8.56) * mm});
            skLineSegment(sketch, "E17.4.0.40", {"start": v(-31.93, 26.56) * mm, "end": v(-35.56, 26.56) * mm});
            skLineSegment(sketch, "E17.4.0.41", {"start": v(-31.94, 9.43) * mm, "end": v(-35.57, 9.43) * mm});
            skLineSegment(sketch, "E17.4.0.42", {"start": v(-35.56, 22.93) * mm, "end": v(-35.56, 26.56) * mm});
            skLineSegment(sketch, "E17.4.0.43", {"start": v(-31.93, -13.94) * mm, "end": v(-35.56, -13.94) * mm});
            skLineSegment(sketch, "E17.4.0.44", {"start": v(-31.93, -31.94) * mm, "end": v(-35.56, -31.94) * mm});
            skLineSegment(sketch, "E17.4.0.45", {"start": v(-31.94, 22.06) * mm, "end": v(-35.57, 22.06) * mm});
            skLineSegment(sketch, "E17.4.0.46", {"start": v(-31.93, 4.06) * mm, "end": v(-35.56, 4.06) * mm});
            skLineSegment(sketch, "E17.4.0.47", {"start": v(-35.56, 0.43) * mm, "end": v(-35.56, 4.06) * mm});
            skLineSegment(sketch, "E17.4.0.48", {"start": v(-35.56, -35.57) * mm, "end": v(-35.56, -31.94) * mm});
            skLineSegment(sketch, "E17.4.0.49", {"start": v(-31.93, 0.43) * mm, "end": v(-31.93, 4.06) * mm});
            skLineSegment(sketch, "E17.4.0.50", {"start": v(-31.93, -26.57) * mm, "end": v(-35.56, -26.57) * mm});
            skLineSegment(sketch, "E17.4.0.51", {"start": v(-31.93, -35.57) * mm, "end": v(-31.93, -31.94) * mm});
            skLineSegment(sketch, "E17.4.0.52", {"start": v(-31.93, -4.07) * mm, "end": v(-31.93, -0.44) * mm});
            skLineSegment(sketch, "E17.4.0.53", {"start": v(-31.93, -22.07) * mm, "end": v(-35.56, -22.07) * mm});
            skLineSegment(sketch, "E17.4.0.54", {"start": v(-31.93, 18.43) * mm, "end": v(-31.93, 22.06) * mm});
            skLineSegment(sketch, "E17.4.0.55", {"start": v(-31.93, -18.44) * mm, "end": v(-35.56, -18.44) * mm});
            skLineSegment(sketch, "E17.4.0.56", {"start": v(-31.93, -8.57) * mm, "end": v(-31.93, -4.94) * mm});
            skLineSegment(sketch, "E17.4.0.57", {"start": v(-31.94, 18.43) * mm, "end": v(-35.57, 18.43) * mm});
            skLineSegment(sketch, "E17.4.0.58", {"start": v(-31.94, 35.56) * mm, "end": v(-35.57, 35.56) * mm});
            skLineSegment(sketch, "E17.4.0.59", {"start": v(-31.93, 4.93) * mm, "end": v(-31.93, 8.56) * mm});
            skLineSegment(sketch, "E17.4.0.60", {"start": v(-31.93, 27.43) * mm, "end": v(-35.56, 27.43) * mm});
            skLineSegment(sketch, "E17.4.0.61", {"start": v(-31.93, -8.57) * mm, "end": v(-35.56, -8.57) * mm});
            skLineSegment(sketch, "E17.4.0.62", {"start": v(-31.94, 8.56) * mm, "end": v(-35.57, 8.56) * mm});
            skLineSegment(sketch, "E17.4.0.63", {"start": v(-35.56, -17.57) * mm, "end": v(-35.56, -13.94) * mm});
            skLineSegment(sketch, "E17.4.0.64", {"start": v(-31.93, 22.93) * mm, "end": v(-35.56, 22.93) * mm});
            skLineSegment(sketch, "E17.4.0.65", {"start": v(-31.93, 22.93) * mm, "end": v(-31.93, 26.56) * mm});
            skLineSegment(sketch, "E17.5.0.0", {"start": v(-31.06, 27.43) * mm, "end": v(-31.06, 31.06) * mm});
            skLineSegment(sketch, "E17.5.0.1", {"start": v(-27.43, 27.43) * mm, "end": v(-27.43, 31.06) * mm});
            skLineSegment(sketch, "E17.5.0.2", {"start": v(-27.43, -13.07) * mm, "end": v(-27.43, -9.44) * mm});
            skLineSegment(sketch, "E17.5.0.3", {"start": v(-31.06, 9.43) * mm, "end": v(-31.06, 13.06) * mm});
            skLineSegment(sketch, "E17.5.0.4", {"start": v(-31.06, -13.07) * mm, "end": v(-31.06, -9.44) * mm});
            skLineSegment(sketch, "E17.5.0.5", {"start": v(-31.06, -31.07) * mm, "end": v(-31.06, -27.44) * mm});
            skPoint(sketch, "E17.5.0.6", {"position": v(-29.25, 33.75) * mm});
            skLineSegment(sketch, "E17.5.0.7", {"start": v(-27.43, 9.43) * mm, "end": v(-27.43, 13.06) * mm});
            skLineSegment(sketch, "E17.5.0.8", {"start": v(-27.43, -31.07) * mm, "end": v(-27.43, -27.44) * mm});
            skLineSegment(sketch, "E17.5.0.9", {"start": v(-27.43, 31.93) * mm, "end": v(-27.43, 27.43) * mm, "construction": true});
            skLineSegment(sketch, "E17.5.0.10", {"start": v(-27.43, 31.06) * mm, "end": v(-31.06, 31.06) * mm});
            skLineSegment(sketch, "E17.5.0.11", {"start": v(-27.44, 4.93) * mm, "end": v(-31.07, 4.93) * mm});
            skLineSegment(sketch, "E17.5.0.12", {"start": v(-27.43, -13.07) * mm, "end": v(-31.06, -13.07) * mm});
            skLineSegment(sketch, "E17.5.0.13", {"start": v(-27.43, -31.07) * mm, "end": v(-31.06, -31.07) * mm});
            skLineSegment(sketch, "E17.5.0.14", {"start": v(-31.06, 31.93) * mm, "end": v(-31.06, 35.56) * mm});
            skLineSegment(sketch, "E17.5.0.15", {"start": v(-27.43, 31.93) * mm, "end": v(-27.43, 35.56) * mm});
            skLineSegment(sketch, "E17.5.0.16", {"start": v(-27.44, 31.93) * mm, "end": v(-31.07, 31.93) * mm});
            skLineSegment(sketch, "E17.5.0.17", {"start": v(-31.06, 18.43) * mm, "end": v(-31.06, 22.06) * mm});
            skLineSegment(sketch, "E17.5.0.18", {"start": v(-27.44, 13.06) * mm, "end": v(-31.07, 13.06) * mm});
            skLineSegment(sketch, "E17.5.0.19", {"start": v(-27.43, -4.94) * mm, "end": v(-31.06, -4.94) * mm});
            skLineSegment(sketch, "E17.5.0.20", {"start": v(-27.43, -22.94) * mm, "end": v(-31.06, -22.94) * mm});
            skLineSegment(sketch, "E17.5.0.21", {"start": v(-27.43, -26.57) * mm, "end": v(-27.43, -22.94) * mm});
            skLineSegment(sketch, "E17.5.0.22", {"start": v(-31.06, -8.57) * mm, "end": v(-31.06, -4.94) * mm});
            skLineSegment(sketch, "E17.5.0.23", {"start": v(-31.06, -26.57) * mm, "end": v(-31.06, -22.94) * mm});
            skLineSegment(sketch, "E17.5.0.24", {"start": v(-27.44, 17.56) * mm, "end": v(-31.07, 17.56) * mm});
            skLineSegment(sketch, "E17.5.0.25", {"start": v(-27.43, -0.44) * mm, "end": v(-31.06, -0.44) * mm});
            skLineSegment(sketch, "E17.5.0.26", {"start": v(-27.43, -9.44) * mm, "end": v(-31.06, -9.44) * mm});
            skLineSegment(sketch, "E17.5.0.27", {"start": v(-31.06, -22.07) * mm, "end": v(-31.06, -18.44) * mm});
            skLineSegment(sketch, "E17.5.0.28", {"start": v(-31.06, 13.93) * mm, "end": v(-31.06, 17.56) * mm});
            skLineSegment(sketch, "E17.5.0.29", {"start": v(-31.06, -4.07) * mm, "end": v(-31.06, -0.44) * mm});
            skLineSegment(sketch, "E17.5.0.30", {"start": v(-27.44, 13.93) * mm, "end": v(-31.07, 13.93) * mm});
            skLineSegment(sketch, "E17.5.0.31", {"start": v(-27.43, -4.07) * mm, "end": v(-31.06, -4.07) * mm});
            skLineSegment(sketch, "E17.5.0.32", {"start": v(-27.43, -17.57) * mm, "end": v(-31.06, -17.57) * mm});
            skLineSegment(sketch, "E17.5.0.33", {"start": v(-27.43, -27.44) * mm, "end": v(-31.06, -27.44) * mm});
            skLineSegment(sketch, "E17.5.0.34", {"start": v(-27.43, -35.57) * mm, "end": v(-31.06, -35.57) * mm});
            skLineSegment(sketch, "E17.5.0.35", {"start": v(-27.43, 0.43) * mm, "end": v(-31.06, 0.43) * mm});
            skLineSegment(sketch, "E17.5.0.36", {"start": v(-27.43, 13.93) * mm, "end": v(-27.43, 17.56) * mm});
            skLineSegment(sketch, "E17.5.0.37", {"start": v(-27.43, -22.07) * mm, "end": v(-27.43, -18.44) * mm});
            skLineSegment(sketch, "E17.5.0.38", {"start": v(-27.43, -17.57) * mm, "end": v(-27.43, -13.94) * mm});
            skLineSegment(sketch, "E17.5.0.39", {"start": v(-31.06, 4.93) * mm, "end": v(-31.06, 8.56) * mm});
            skLineSegment(sketch, "E17.5.0.40", {"start": v(-27.43, 26.56) * mm, "end": v(-31.06, 26.56) * mm});
            skLineSegment(sketch, "E17.5.0.41", {"start": v(-27.44, 9.43) * mm, "end": v(-31.07, 9.43) * mm});
            skLineSegment(sketch, "E17.5.0.42", {"start": v(-31.06, 22.93) * mm, "end": v(-31.06, 26.56) * mm});
            skLineSegment(sketch, "E17.5.0.43", {"start": v(-27.43, -13.94) * mm, "end": v(-31.06, -13.94) * mm});
            skLineSegment(sketch, "E17.5.0.44", {"start": v(-27.43, -31.94) * mm, "end": v(-31.06, -31.94) * mm});
            skLineSegment(sketch, "E17.5.0.45", {"start": v(-27.44, 22.06) * mm, "end": v(-31.07, 22.06) * mm});
            skLineSegment(sketch, "E17.5.0.46", {"start": v(-27.43, 4.06) * mm, "end": v(-31.06, 4.06) * mm});
            skLineSegment(sketch, "E17.5.0.47", {"start": v(-31.06, 0.43) * mm, "end": v(-31.06, 4.06) * mm});
            skLineSegment(sketch, "E17.5.0.48", {"start": v(-31.06, -35.57) * mm, "end": v(-31.06, -31.94) * mm});
            skLineSegment(sketch, "E17.5.0.49", {"start": v(-27.43, 0.43) * mm, "end": v(-27.43, 4.06) * mm});
            skLineSegment(sketch, "E17.5.0.50", {"start": v(-27.43, -26.57) * mm, "end": v(-31.06, -26.57) * mm});
            skLineSegment(sketch, "E17.5.0.51", {"start": v(-27.43, -35.57) * mm, "end": v(-27.43, -31.94) * mm});
            skLineSegment(sketch, "E17.5.0.52", {"start": v(-27.43, -4.07) * mm, "end": v(-27.43, -0.44) * mm});
            skLineSegment(sketch, "E17.5.0.53", {"start": v(-27.43, -22.07) * mm, "end": v(-31.06, -22.07) * mm});
            skLineSegment(sketch, "E17.5.0.54", {"start": v(-27.43, 18.43) * mm, "end": v(-27.43, 22.06) * mm});
            skLineSegment(sketch, "E17.5.0.55", {"start": v(-27.43, -18.44) * mm, "end": v(-31.06, -18.44) * mm});
            skLineSegment(sketch, "E17.5.0.56", {"start": v(-27.43, -8.57) * mm, "end": v(-27.43, -4.94) * mm});
            skLineSegment(sketch, "E17.5.0.57", {"start": v(-27.44, 18.43) * mm, "end": v(-31.07, 18.43) * mm});
            skLineSegment(sketch, "E17.5.0.58", {"start": v(-27.44, 35.56) * mm, "end": v(-31.07, 35.56) * mm});
            skLineSegment(sketch, "E17.5.0.59", {"start": v(-27.43, 4.93) * mm, "end": v(-27.43, 8.56) * mm});
            skLineSegment(sketch, "E17.5.0.60", {"start": v(-27.43, 27.43) * mm, "end": v(-31.06, 27.43) * mm});
            skLineSegment(sketch, "E17.5.0.61", {"start": v(-27.43, -8.57) * mm, "end": v(-31.06, -8.57) * mm});
            skLineSegment(sketch, "E17.5.0.62", {"start": v(-27.44, 8.56) * mm, "end": v(-31.07, 8.56) * mm});
            skLineSegment(sketch, "E17.5.0.63", {"start": v(-31.06, -17.57) * mm, "end": v(-31.06, -13.94) * mm});
            skLineSegment(sketch, "E17.5.0.64", {"start": v(-27.43, 22.93) * mm, "end": v(-31.06, 22.93) * mm});
            skLineSegment(sketch, "E17.5.0.65", {"start": v(-27.43, 22.93) * mm, "end": v(-27.43, 26.56) * mm});
            skLineSegment(sketch, "E17.6.0.0", {"start": v(-26.56, 27.43) * mm, "end": v(-26.56, 31.06) * mm});
            skLineSegment(sketch, "E17.6.0.1", {"start": v(-22.93, 27.43) * mm, "end": v(-22.93, 31.06) * mm});
            skLineSegment(sketch, "E17.6.0.2", {"start": v(-22.93, -13.07) * mm, "end": v(-22.93, -9.44) * mm});
            skLineSegment(sketch, "E17.6.0.3", {"start": v(-26.56, 9.43) * mm, "end": v(-26.56, 13.06) * mm});
            skLineSegment(sketch, "E17.6.0.4", {"start": v(-26.56, -13.07) * mm, "end": v(-26.56, -9.44) * mm});
            skLineSegment(sketch, "E17.6.0.5", {"start": v(-26.56, -31.07) * mm, "end": v(-26.56, -27.44) * mm});
            skPoint(sketch, "E17.6.0.6", {"position": v(-24.75, 33.75) * mm});
            skLineSegment(sketch, "E17.6.0.7", {"start": v(-22.93, 9.43) * mm, "end": v(-22.93, 13.06) * mm});
            skLineSegment(sketch, "E17.6.0.8", {"start": v(-22.93, -31.07) * mm, "end": v(-22.93, -27.44) * mm});
            skLineSegment(sketch, "E17.6.0.9", {"start": v(-22.93, 31.93) * mm, "end": v(-22.93, 27.43) * mm, "construction": true});
            skLineSegment(sketch, "E17.6.0.10", {"start": v(-22.93, 31.06) * mm, "end": v(-26.56, 31.06) * mm});
            skLineSegment(sketch, "E17.6.0.11", {"start": v(-22.93, 4.93) * mm, "end": v(-26.56, 4.93) * mm});
            skLineSegment(sketch, "E17.6.0.12", {"start": v(-22.93, -13.07) * mm, "end": v(-26.56, -13.07) * mm});
            skLineSegment(sketch, "E17.6.0.13", {"start": v(-22.93, -31.07) * mm, "end": v(-26.56, -31.07) * mm});
            skLineSegment(sketch, "E17.6.0.14", {"start": v(-26.56, 31.93) * mm, "end": v(-26.56, 35.56) * mm});
            skLineSegment(sketch, "E17.6.0.15", {"start": v(-22.93, 31.93) * mm, "end": v(-22.93, 35.56) * mm});
            skLineSegment(sketch, "E17.6.0.16", {"start": v(-22.93, 31.93) * mm, "end": v(-26.56, 31.93) * mm});
            skLineSegment(sketch, "E17.6.0.17", {"start": v(-26.56, 18.43) * mm, "end": v(-26.56, 22.06) * mm});
            skLineSegment(sketch, "E17.6.0.18", {"start": v(-22.93, 13.06) * mm, "end": v(-26.56, 13.06) * mm});
            skLineSegment(sketch, "E17.6.0.19", {"start": v(-22.93, -4.94) * mm, "end": v(-26.56, -4.94) * mm});
            skLineSegment(sketch, "E17.6.0.20", {"start": v(-22.93, -22.94) * mm, "end": v(-26.56, -22.94) * mm});
            skLineSegment(sketch, "E17.6.0.21", {"start": v(-22.93, -26.57) * mm, "end": v(-22.93, -22.94) * mm});
            skLineSegment(sketch, "E17.6.0.22", {"start": v(-26.56, -8.57) * mm, "end": v(-26.56, -4.94) * mm});
            skLineSegment(sketch, "E17.6.0.23", {"start": v(-26.56, -26.57) * mm, "end": v(-26.56, -22.94) * mm});
            skLineSegment(sketch, "E17.6.0.24", {"start": v(-22.93, 17.56) * mm, "end": v(-26.56, 17.56) * mm});
            skLineSegment(sketch, "E17.6.0.25", {"start": v(-22.93, -0.44) * mm, "end": v(-26.56, -0.44) * mm});
            skLineSegment(sketch, "E17.6.0.26", {"start": v(-22.93, -9.44) * mm, "end": v(-26.56, -9.44) * mm});
            skLineSegment(sketch, "E17.6.0.27", {"start": v(-26.56, -22.07) * mm, "end": v(-26.56, -18.44) * mm});
            skLineSegment(sketch, "E17.6.0.28", {"start": v(-26.56, 13.93) * mm, "end": v(-26.56, 17.56) * mm});
            skLineSegment(sketch, "E17.6.0.29", {"start": v(-26.56, -4.07) * mm, "end": v(-26.56, -0.44) * mm});
            skLineSegment(sketch, "E17.6.0.30", {"start": v(-22.93, 13.93) * mm, "end": v(-26.56, 13.93) * mm});
            skLineSegment(sketch, "E17.6.0.31", {"start": v(-22.93, -4.07) * mm, "end": v(-26.56, -4.07) * mm});
            skLineSegment(sketch, "E17.6.0.32", {"start": v(-22.93, -17.57) * mm, "end": v(-26.56, -17.57) * mm});
            skLineSegment(sketch, "E17.6.0.33", {"start": v(-22.93, -27.44) * mm, "end": v(-26.56, -27.44) * mm});
            skLineSegment(sketch, "E17.6.0.34", {"start": v(-22.93, -35.57) * mm, "end": v(-26.56, -35.57) * mm});
            skLineSegment(sketch, "E17.6.0.35", {"start": v(-22.93, 0.43) * mm, "end": v(-26.56, 0.43) * mm});
            skLineSegment(sketch, "E17.6.0.36", {"start": v(-22.93, 13.93) * mm, "end": v(-22.93, 17.56) * mm});
            skLineSegment(sketch, "E17.6.0.37", {"start": v(-22.93, -22.07) * mm, "end": v(-22.93, -18.44) * mm});
            skLineSegment(sketch, "E17.6.0.38", {"start": v(-22.93, -17.57) * mm, "end": v(-22.93, -13.94) * mm});
            skLineSegment(sketch, "E17.6.0.39", {"start": v(-26.56, 4.93) * mm, "end": v(-26.56, 8.56) * mm});
            skLineSegment(sketch, "E17.6.0.40", {"start": v(-22.93, 26.56) * mm, "end": v(-26.56, 26.56) * mm});
            skLineSegment(sketch, "E17.6.0.41", {"start": v(-22.93, 9.43) * mm, "end": v(-26.56, 9.43) * mm});
            skLineSegment(sketch, "E17.6.0.42", {"start": v(-26.56, 22.93) * mm, "end": v(-26.56, 26.56) * mm});
            skLineSegment(sketch, "E17.6.0.43", {"start": v(-22.93, -13.94) * mm, "end": v(-26.56, -13.94) * mm});
            skLineSegment(sketch, "E17.6.0.44", {"start": v(-22.93, -31.94) * mm, "end": v(-26.56, -31.94) * mm});
            skLineSegment(sketch, "E17.6.0.45", {"start": v(-22.93, 22.06) * mm, "end": v(-26.56, 22.06) * mm});
            skLineSegment(sketch, "E17.6.0.46", {"start": v(-22.93, 4.06) * mm, "end": v(-26.56, 4.06) * mm});
            skLineSegment(sketch, "E17.6.0.47", {"start": v(-26.56, 0.43) * mm, "end": v(-26.56, 4.06) * mm});
            skLineSegment(sketch, "E17.6.0.48", {"start": v(-26.56, -35.57) * mm, "end": v(-26.56, -31.94) * mm});
            skLineSegment(sketch, "E17.6.0.49", {"start": v(-22.93, 0.43) * mm, "end": v(-22.93, 4.06) * mm});
            skLineSegment(sketch, "E17.6.0.50", {"start": v(-22.93, -26.57) * mm, "end": v(-26.56, -26.57) * mm});
            skLineSegment(sketch, "E17.6.0.51", {"start": v(-22.93, -35.57) * mm, "end": v(-22.93, -31.94) * mm});
            skLineSegment(sketch, "E17.6.0.52", {"start": v(-22.93, -4.07) * mm, "end": v(-22.93, -0.44) * mm});
            skLineSegment(sketch, "E17.6.0.53", {"start": v(-22.93, -22.07) * mm, "end": v(-26.56, -22.07) * mm});
            skLineSegment(sketch, "E17.6.0.54", {"start": v(-22.93, 18.43) * mm, "end": v(-22.93, 22.06) * mm});
            skLineSegment(sketch, "E17.6.0.55", {"start": v(-22.93, -18.44) * mm, "end": v(-26.56, -18.44) * mm});
            skLineSegment(sketch, "E17.6.0.56", {"start": v(-22.93, -8.57) * mm, "end": v(-22.93, -4.94) * mm});
            skLineSegment(sketch, "E17.6.0.57", {"start": v(-22.93, 18.43) * mm, "end": v(-26.56, 18.43) * mm});
            skLineSegment(sketch, "E17.6.0.58", {"start": v(-22.93, 35.56) * mm, "end": v(-26.56, 35.56) * mm});
            skLineSegment(sketch, "E17.6.0.59", {"start": v(-22.93, 4.93) * mm, "end": v(-22.93, 8.56) * mm});
            skLineSegment(sketch, "E17.6.0.60", {"start": v(-22.93, 27.43) * mm, "end": v(-26.56, 27.43) * mm});
            skLineSegment(sketch, "E17.6.0.61", {"start": v(-22.93, -8.57) * mm, "end": v(-26.56, -8.57) * mm});
            skLineSegment(sketch, "E17.6.0.62", {"start": v(-22.93, 8.56) * mm, "end": v(-26.56, 8.56) * mm});
            skLineSegment(sketch, "E17.6.0.63", {"start": v(-26.56, -17.57) * mm, "end": v(-26.56, -13.94) * mm});
            skLineSegment(sketch, "E17.6.0.64", {"start": v(-22.93, 22.93) * mm, "end": v(-26.56, 22.93) * mm});
            skLineSegment(sketch, "E17.6.0.65", {"start": v(-22.93, 22.93) * mm, "end": v(-22.93, 26.56) * mm});
            skLineSegment(sketch, "E17.7.0.0", {"start": v(-22.06, 27.43) * mm, "end": v(-22.06, 31.06) * mm});
            skLineSegment(sketch, "E17.7.0.1", {"start": v(-18.43, 27.43) * mm, "end": v(-18.43, 31.06) * mm});
            skLineSegment(sketch, "E17.7.0.2", {"start": v(-18.43, -13.07) * mm, "end": v(-18.43, -9.44) * mm});
            skLineSegment(sketch, "E17.7.0.3", {"start": v(-22.06, 9.43) * mm, "end": v(-22.06, 13.06) * mm});
            skLineSegment(sketch, "E17.7.0.4", {"start": v(-22.06, -13.07) * mm, "end": v(-22.06, -9.44) * mm});
            skLineSegment(sketch, "E17.7.0.5", {"start": v(-22.06, -31.07) * mm, "end": v(-22.06, -27.44) * mm});
            skPoint(sketch, "E17.7.0.6", {"position": v(-20.25, 33.75) * mm});
            skLineSegment(sketch, "E17.7.0.7", {"start": v(-18.43, 9.43) * mm, "end": v(-18.43, 13.06) * mm});
            skLineSegment(sketch, "E17.7.0.8", {"start": v(-18.43, -31.07) * mm, "end": v(-18.43, -27.44) * mm});
            skLineSegment(sketch, "E17.7.0.9", {"start": v(-18.43, 31.93) * mm, "end": v(-18.43, 27.43) * mm, "construction": true});
            skLineSegment(sketch, "E17.7.0.10", {"start": v(-18.43, 31.06) * mm, "end": v(-22.06, 31.06) * mm});
            skLineSegment(sketch, "E17.7.0.11", {"start": v(-18.43, 4.93) * mm, "end": v(-22.06, 4.93) * mm});
            skLineSegment(sketch, "E17.7.0.12", {"start": v(-18.43, -13.07) * mm, "end": v(-22.06, -13.07) * mm});
            skLineSegment(sketch, "E17.7.0.13", {"start": v(-18.43, -31.07) * mm, "end": v(-22.06, -31.07) * mm});
            skLineSegment(sketch, "E17.7.0.14", {"start": v(-22.06, 31.93) * mm, "end": v(-22.06, 35.56) * mm});
            skLineSegment(sketch, "E17.7.0.15", {"start": v(-18.43, 31.93) * mm, "end": v(-18.43, 35.56) * mm});
            skLineSegment(sketch, "E17.7.0.16", {"start": v(-18.43, 31.93) * mm, "end": v(-22.06, 31.93) * mm});
            skLineSegment(sketch, "E17.7.0.17", {"start": v(-22.06, 18.43) * mm, "end": v(-22.06, 22.06) * mm});
            skLineSegment(sketch, "E17.7.0.18", {"start": v(-18.43, 13.06) * mm, "end": v(-22.06, 13.06) * mm});
            skLineSegment(sketch, "E17.7.0.19", {"start": v(-18.43, -4.94) * mm, "end": v(-22.06, -4.94) * mm});
            skLineSegment(sketch, "E17.7.0.20", {"start": v(-18.43, -22.94) * mm, "end": v(-22.06, -22.94) * mm});
            skLineSegment(sketch, "E17.7.0.21", {"start": v(-18.43, -26.57) * mm, "end": v(-18.43, -22.94) * mm});
            skLineSegment(sketch, "E17.7.0.22", {"start": v(-22.06, -8.57) * mm, "end": v(-22.06, -4.94) * mm});
            skLineSegment(sketch, "E17.7.0.23", {"start": v(-22.06, -26.57) * mm, "end": v(-22.06, -22.94) * mm});
            skLineSegment(sketch, "E17.7.0.24", {"start": v(-18.43, 17.56) * mm, "end": v(-22.06, 17.56) * mm});
            skLineSegment(sketch, "E17.7.0.25", {"start": v(-18.43, -0.44) * mm, "end": v(-22.06, -0.44) * mm});
            skLineSegment(sketch, "E17.7.0.26", {"start": v(-18.43, -9.44) * mm, "end": v(-22.06, -9.44) * mm});
            skLineSegment(sketch, "E17.7.0.27", {"start": v(-22.06, -22.07) * mm, "end": v(-22.06, -18.44) * mm});
            skLineSegment(sketch, "E17.7.0.28", {"start": v(-22.06, 13.93) * mm, "end": v(-22.06, 17.56) * mm});
            skLineSegment(sketch, "E17.7.0.29", {"start": v(-22.06, -4.07) * mm, "end": v(-22.06, -0.44) * mm});
            skLineSegment(sketch, "E17.7.0.30", {"start": v(-18.43, 13.93) * mm, "end": v(-22.06, 13.93) * mm});
            skLineSegment(sketch, "E17.7.0.31", {"start": v(-18.43, -4.07) * mm, "end": v(-22.06, -4.07) * mm});
            skLineSegment(sketch, "E17.7.0.32", {"start": v(-18.43, -17.57) * mm, "end": v(-22.06, -17.57) * mm});
            skLineSegment(sketch, "E17.7.0.33", {"start": v(-18.43, -27.44) * mm, "end": v(-22.06, -27.44) * mm});
            skLineSegment(sketch, "E17.7.0.34", {"start": v(-18.43, -35.57) * mm, "end": v(-22.06, -35.57) * mm});
            skLineSegment(sketch, "E17.7.0.35", {"start": v(-18.43, 0.43) * mm, "end": v(-22.06, 0.43) * mm});
            skLineSegment(sketch, "E17.7.0.36", {"start": v(-18.43, 13.93) * mm, "end": v(-18.43, 17.56) * mm});
            skLineSegment(sketch, "E17.7.0.37", {"start": v(-18.43, -22.07) * mm, "end": v(-18.43, -18.44) * mm});
            skLineSegment(sketch, "E17.7.0.38", {"start": v(-18.43, -17.57) * mm, "end": v(-18.43, -13.94) * mm});
            skLineSegment(sketch, "E17.7.0.39", {"start": v(-22.06, 4.93) * mm, "end": v(-22.06, 8.56) * mm});
            skLineSegment(sketch, "E17.7.0.40", {"start": v(-18.43, 26.56) * mm, "end": v(-22.06, 26.56) * mm});
            skLineSegment(sketch, "E17.7.0.41", {"start": v(-18.43, 9.43) * mm, "end": v(-22.06, 9.43) * mm});
            skLineSegment(sketch, "E17.7.0.42", {"start": v(-22.06, 22.93) * mm, "end": v(-22.06, 26.56) * mm});
            skLineSegment(sketch, "E17.7.0.43", {"start": v(-18.43, -13.94) * mm, "end": v(-22.06, -13.94) * mm});
            skLineSegment(sketch, "E17.7.0.44", {"start": v(-18.43, -31.94) * mm, "end": v(-22.06, -31.94) * mm});
            skLineSegment(sketch, "E17.7.0.45", {"start": v(-18.43, 22.06) * mm, "end": v(-22.06, 22.06) * mm});
            skLineSegment(sketch, "E17.7.0.46", {"start": v(-18.43, 4.06) * mm, "end": v(-22.06, 4.06) * mm});
            skLineSegment(sketch, "E17.7.0.47", {"start": v(-22.06, 0.43) * mm, "end": v(-22.06, 4.06) * mm});
            skLineSegment(sketch, "E17.7.0.48", {"start": v(-22.06, -35.57) * mm, "end": v(-22.06, -31.94) * mm});
            skLineSegment(sketch, "E17.7.0.49", {"start": v(-18.43, 0.43) * mm, "end": v(-18.43, 4.06) * mm});
            skLineSegment(sketch, "E17.7.0.50", {"start": v(-18.43, -26.57) * mm, "end": v(-22.06, -26.57) * mm});
            skLineSegment(sketch, "E17.7.0.51", {"start": v(-18.43, -35.57) * mm, "end": v(-18.43, -31.94) * mm});
            skLineSegment(sketch, "E17.7.0.52", {"start": v(-18.43, -4.07) * mm, "end": v(-18.43, -0.44) * mm});
            skLineSegment(sketch, "E17.7.0.53", {"start": v(-18.43, -22.07) * mm, "end": v(-22.06, -22.07) * mm});
            skLineSegment(sketch, "E17.7.0.54", {"start": v(-18.43, 18.43) * mm, "end": v(-18.43, 22.06) * mm});
            skLineSegment(sketch, "E17.7.0.55", {"start": v(-18.43, -18.44) * mm, "end": v(-22.06, -18.44) * mm});
            skLineSegment(sketch, "E17.7.0.56", {"start": v(-18.43, -8.57) * mm, "end": v(-18.43, -4.94) * mm});
            skLineSegment(sketch, "E17.7.0.57", {"start": v(-18.43, 18.43) * mm, "end": v(-22.06, 18.43) * mm});
            skLineSegment(sketch, "E17.7.0.58", {"start": v(-18.43, 35.56) * mm, "end": v(-22.06, 35.56) * mm});
            skLineSegment(sketch, "E17.7.0.59", {"start": v(-18.43, 4.93) * mm, "end": v(-18.43, 8.56) * mm});
            skLineSegment(sketch, "E17.7.0.60", {"start": v(-18.43, 27.43) * mm, "end": v(-22.06, 27.43) * mm});
            skLineSegment(sketch, "E17.7.0.61", {"start": v(-18.43, -8.57) * mm, "end": v(-22.06, -8.57) * mm});
            skLineSegment(sketch, "E17.7.0.62", {"start": v(-18.43, 8.56) * mm, "end": v(-22.06, 8.56) * mm});
            skLineSegment(sketch, "E17.7.0.63", {"start": v(-22.06, -17.57) * mm, "end": v(-22.06, -13.94) * mm});
            skLineSegment(sketch, "E17.7.0.64", {"start": v(-18.43, 22.93) * mm, "end": v(-22.06, 22.93) * mm});
            skLineSegment(sketch, "E17.7.0.65", {"start": v(-18.43, 22.93) * mm, "end": v(-18.43, 26.56) * mm});
            skLineSegment(sketch, "E17.8.0.0", {"start": v(-17.56, 27.43) * mm, "end": v(-17.56, 31.06) * mm});
            skLineSegment(sketch, "E17.8.0.1", {"start": v(-13.93, 27.43) * mm, "end": v(-13.93, 31.06) * mm});
            skLineSegment(sketch, "E17.8.0.2", {"start": v(-13.93, -13.07) * mm, "end": v(-13.93, -9.44) * mm});
            skLineSegment(sketch, "E17.8.0.3", {"start": v(-17.56, 9.43) * mm, "end": v(-17.56, 13.06) * mm});
            skLineSegment(sketch, "E17.8.0.4", {"start": v(-17.56, -13.07) * mm, "end": v(-17.56, -9.44) * mm});
            skLineSegment(sketch, "E17.8.0.5", {"start": v(-17.56, -31.07) * mm, "end": v(-17.56, -27.44) * mm});
            skPoint(sketch, "E17.8.0.6", {"position": v(-15.75, 33.75) * mm});
            skLineSegment(sketch, "E17.8.0.7", {"start": v(-13.93, 9.43) * mm, "end": v(-13.93, 13.06) * mm});
            skLineSegment(sketch, "E17.8.0.8", {"start": v(-13.93, -31.07) * mm, "end": v(-13.93, -27.44) * mm});
            skLineSegment(sketch, "E17.8.0.9", {"start": v(-13.93, 31.93) * mm, "end": v(-13.93, 27.43) * mm, "construction": true});
            skLineSegment(sketch, "E17.8.0.10", {"start": v(-13.93, 31.06) * mm, "end": v(-17.56, 31.06) * mm});
            skLineSegment(sketch, "E17.8.0.11", {"start": v(-13.93, 4.93) * mm, "end": v(-17.56, 4.93) * mm});
            skLineSegment(sketch, "E17.8.0.12", {"start": v(-13.93, -13.07) * mm, "end": v(-17.56, -13.07) * mm});
            skLineSegment(sketch, "E17.8.0.13", {"start": v(-13.93, -31.07) * mm, "end": v(-17.56, -31.07) * mm});
            skLineSegment(sketch, "E17.8.0.14", {"start": v(-17.56, 31.93) * mm, "end": v(-17.56, 35.56) * mm});
            skLineSegment(sketch, "E17.8.0.15", {"start": v(-13.93, 31.93) * mm, "end": v(-13.93, 35.56) * mm});
            skLineSegment(sketch, "E17.8.0.16", {"start": v(-13.93, 31.93) * mm, "end": v(-17.56, 31.93) * mm});
            skLineSegment(sketch, "E17.8.0.17", {"start": v(-17.56, 18.43) * mm, "end": v(-17.56, 22.06) * mm});
            skLineSegment(sketch, "E17.8.0.18", {"start": v(-13.93, 13.06) * mm, "end": v(-17.56, 13.06) * mm});
            skLineSegment(sketch, "E17.8.0.19", {"start": v(-13.93, -4.94) * mm, "end": v(-17.56, -4.94) * mm});
            skLineSegment(sketch, "E17.8.0.20", {"start": v(-13.93, -22.94) * mm, "end": v(-17.56, -22.94) * mm});
            skLineSegment(sketch, "E17.8.0.21", {"start": v(-13.93, -26.57) * mm, "end": v(-13.93, -22.94) * mm});
            skLineSegment(sketch, "E17.8.0.22", {"start": v(-17.56, -8.57) * mm, "end": v(-17.56, -4.94) * mm});
            skLineSegment(sketch, "E17.8.0.23", {"start": v(-17.56, -26.57) * mm, "end": v(-17.56, -22.94) * mm});
            skLineSegment(sketch, "E17.8.0.24", {"start": v(-13.93, 17.56) * mm, "end": v(-17.56, 17.56) * mm});
            skLineSegment(sketch, "E17.8.0.25", {"start": v(-13.93, -0.44) * mm, "end": v(-17.56, -0.44) * mm});
            skLineSegment(sketch, "E17.8.0.26", {"start": v(-13.93, -9.44) * mm, "end": v(-17.56, -9.44) * mm});
            skLineSegment(sketch, "E17.8.0.27", {"start": v(-17.56, -22.07) * mm, "end": v(-17.56, -18.44) * mm});
            skLineSegment(sketch, "E17.8.0.28", {"start": v(-17.56, 13.93) * mm, "end": v(-17.56, 17.56) * mm});
            skLineSegment(sketch, "E17.8.0.29", {"start": v(-17.56, -4.07) * mm, "end": v(-17.56, -0.44) * mm});
            skLineSegment(sketch, "E17.8.0.30", {"start": v(-13.93, 13.93) * mm, "end": v(-17.56, 13.93) * mm});
            skLineSegment(sketch, "E17.8.0.31", {"start": v(-13.93, -4.07) * mm, "end": v(-17.56, -4.07) * mm});
            skLineSegment(sketch, "E17.8.0.32", {"start": v(-13.93, -17.57) * mm, "end": v(-17.56, -17.57) * mm});
            skLineSegment(sketch, "E17.8.0.33", {"start": v(-13.93, -27.44) * mm, "end": v(-17.56, -27.44) * mm});
            skLineSegment(sketch, "E17.8.0.34", {"start": v(-13.93, -35.57) * mm, "end": v(-17.56, -35.57) * mm});
            skLineSegment(sketch, "E17.8.0.35", {"start": v(-13.93, 0.43) * mm, "end": v(-17.56, 0.43) * mm});
            skLineSegment(sketch, "E17.8.0.36", {"start": v(-13.93, 13.93) * mm, "end": v(-13.93, 17.56) * mm});
            skLineSegment(sketch, "E17.8.0.37", {"start": v(-13.93, -22.07) * mm, "end": v(-13.93, -18.44) * mm});
            skLineSegment(sketch, "E17.8.0.38", {"start": v(-13.93, -17.57) * mm, "end": v(-13.93, -13.94) * mm});
            skLineSegment(sketch, "E17.8.0.39", {"start": v(-17.56, 4.93) * mm, "end": v(-17.56, 8.56) * mm});
            skLineSegment(sketch, "E17.8.0.40", {"start": v(-13.93, 26.56) * mm, "end": v(-17.56, 26.56) * mm});
            skLineSegment(sketch, "E17.8.0.41", {"start": v(-13.93, 9.43) * mm, "end": v(-17.56, 9.43) * mm});
            skLineSegment(sketch, "E17.8.0.42", {"start": v(-17.56, 22.93) * mm, "end": v(-17.56, 26.56) * mm});
            skLineSegment(sketch, "E17.8.0.43", {"start": v(-13.93, -13.94) * mm, "end": v(-17.56, -13.94) * mm});
            skLineSegment(sketch, "E17.8.0.44", {"start": v(-13.93, -31.94) * mm, "end": v(-17.56, -31.94) * mm});
            skLineSegment(sketch, "E17.8.0.45", {"start": v(-13.93, 22.06) * mm, "end": v(-17.56, 22.06) * mm});
            skLineSegment(sketch, "E17.8.0.46", {"start": v(-13.93, 4.06) * mm, "end": v(-17.56, 4.06) * mm});
            skLineSegment(sketch, "E17.8.0.47", {"start": v(-17.56, 0.43) * mm, "end": v(-17.56, 4.06) * mm});
            skLineSegment(sketch, "E17.8.0.48", {"start": v(-17.56, -35.57) * mm, "end": v(-17.56, -31.94) * mm});
            skLineSegment(sketch, "E17.8.0.49", {"start": v(-13.93, 0.43) * mm, "end": v(-13.93, 4.06) * mm});
            skLineSegment(sketch, "E17.8.0.50", {"start": v(-13.93, -26.57) * mm, "end": v(-17.56, -26.57) * mm});
            skLineSegment(sketch, "E17.8.0.51", {"start": v(-13.93, -35.57) * mm, "end": v(-13.93, -31.94) * mm});
            skLineSegment(sketch, "E17.8.0.52", {"start": v(-13.93, -4.07) * mm, "end": v(-13.93, -0.44) * mm});
            skLineSegment(sketch, "E17.8.0.53", {"start": v(-13.93, -22.07) * mm, "end": v(-17.56, -22.07) * mm});
            skLineSegment(sketch, "E17.8.0.54", {"start": v(-13.93, 18.43) * mm, "end": v(-13.93, 22.06) * mm});
            skLineSegment(sketch, "E17.8.0.55", {"start": v(-13.93, -18.44) * mm, "end": v(-17.56, -18.44) * mm});
            skLineSegment(sketch, "E17.8.0.56", {"start": v(-13.93, -8.57) * mm, "end": v(-13.93, -4.94) * mm});
            skLineSegment(sketch, "E17.8.0.57", {"start": v(-13.93, 18.43) * mm, "end": v(-17.56, 18.43) * mm});
            skLineSegment(sketch, "E17.8.0.58", {"start": v(-13.93, 35.56) * mm, "end": v(-17.56, 35.56) * mm});
            skLineSegment(sketch, "E17.8.0.59", {"start": v(-13.93, 4.93) * mm, "end": v(-13.93, 8.56) * mm});
            skLineSegment(sketch, "E17.8.0.60", {"start": v(-13.93, 27.43) * mm, "end": v(-17.56, 27.43) * mm});
            skLineSegment(sketch, "E17.8.0.61", {"start": v(-13.93, -8.57) * mm, "end": v(-17.56, -8.57) * mm});
            skLineSegment(sketch, "E17.8.0.62", {"start": v(-13.93, 8.56) * mm, "end": v(-17.56, 8.56) * mm});
            skLineSegment(sketch, "E17.8.0.63", {"start": v(-17.56, -17.57) * mm, "end": v(-17.56, -13.94) * mm});
            skLineSegment(sketch, "E17.8.0.64", {"start": v(-13.93, 22.93) * mm, "end": v(-17.56, 22.93) * mm});
            skLineSegment(sketch, "E17.8.0.65", {"start": v(-13.93, 22.93) * mm, "end": v(-13.93, 26.56) * mm});
            skLineSegment(sketch, "E17.9.0.0", {"start": v(-13.06, 27.43) * mm, "end": v(-13.06, 31.06) * mm});
            skLineSegment(sketch, "E17.9.0.1", {"start": v(-9.43, 27.43) * mm, "end": v(-9.43, 31.06) * mm});
            skLineSegment(sketch, "E17.9.0.2", {"start": v(-9.43, -13.07) * mm, "end": v(-9.43, -9.44) * mm});
            skLineSegment(sketch, "E17.9.0.3", {"start": v(-13.06, 9.43) * mm, "end": v(-13.06, 13.06) * mm});
            skLineSegment(sketch, "E17.9.0.4", {"start": v(-13.06, -13.07) * mm, "end": v(-13.06, -9.44) * mm});
            skLineSegment(sketch, "E17.9.0.5", {"start": v(-13.06, -31.07) * mm, "end": v(-13.06, -27.44) * mm});
            skPoint(sketch, "E17.9.0.6", {"position": v(-11.25, 33.75) * mm});
            skLineSegment(sketch, "E17.9.0.7", {"start": v(-9.43, 9.43) * mm, "end": v(-9.43, 13.06) * mm});
            skLineSegment(sketch, "E17.9.0.8", {"start": v(-9.43, -31.07) * mm, "end": v(-9.43, -27.44) * mm});
            skLineSegment(sketch, "E17.9.0.9", {"start": v(-9.43, 31.93) * mm, "end": v(-9.43, 27.43) * mm, "construction": true});
            skLineSegment(sketch, "E17.9.0.10", {"start": v(-9.43, 31.06) * mm, "end": v(-13.06, 31.06) * mm});
            skLineSegment(sketch, "E17.9.0.11", {"start": v(-9.43, 4.93) * mm, "end": v(-13.06, 4.93) * mm});
            skLineSegment(sketch, "E17.9.0.12", {"start": v(-9.43, -13.07) * mm, "end": v(-13.06, -13.07) * mm});
            skLineSegment(sketch, "E17.9.0.13", {"start": v(-9.43, -31.07) * mm, "end": v(-13.06, -31.07) * mm});
            skLineSegment(sketch, "E17.9.0.14", {"start": v(-13.06, 31.93) * mm, "end": v(-13.06, 35.56) * mm});
            skLineSegment(sketch, "E17.9.0.15", {"start": v(-9.43, 31.93) * mm, "end": v(-9.43, 35.56) * mm});
            skLineSegment(sketch, "E17.9.0.16", {"start": v(-9.43, 31.93) * mm, "end": v(-13.06, 31.93) * mm});
            skLineSegment(sketch, "E17.9.0.17", {"start": v(-13.06, 18.43) * mm, "end": v(-13.06, 22.06) * mm});
            skLineSegment(sketch, "E17.9.0.18", {"start": v(-9.43, 13.06) * mm, "end": v(-13.06, 13.06) * mm});
            skLineSegment(sketch, "E17.9.0.19", {"start": v(-9.43, -4.94) * mm, "end": v(-13.06, -4.94) * mm});
            skLineSegment(sketch, "E17.9.0.20", {"start": v(-9.43, -22.94) * mm, "end": v(-13.06, -22.94) * mm});
            skLineSegment(sketch, "E17.9.0.21", {"start": v(-9.43, -26.57) * mm, "end": v(-9.43, -22.94) * mm});
            skLineSegment(sketch, "E17.9.0.22", {"start": v(-13.06, -8.57) * mm, "end": v(-13.06, -4.94) * mm});
            skLineSegment(sketch, "E17.9.0.23", {"start": v(-13.06, -26.57) * mm, "end": v(-13.06, -22.94) * mm});
            skLineSegment(sketch, "E17.9.0.24", {"start": v(-9.43, 17.56) * mm, "end": v(-13.06, 17.56) * mm});
            skLineSegment(sketch, "E17.9.0.25", {"start": v(-9.43, -0.44) * mm, "end": v(-13.06, -0.44) * mm});
            skLineSegment(sketch, "E17.9.0.26", {"start": v(-9.43, -9.44) * mm, "end": v(-13.06, -9.44) * mm});
            skLineSegment(sketch, "E17.9.0.27", {"start": v(-13.06, -22.07) * mm, "end": v(-13.06, -18.44) * mm});
            skLineSegment(sketch, "E17.9.0.28", {"start": v(-13.06, 13.93) * mm, "end": v(-13.06, 17.56) * mm});
            skLineSegment(sketch, "E17.9.0.29", {"start": v(-13.06, -4.07) * mm, "end": v(-13.06, -0.44) * mm});
            skLineSegment(sketch, "E17.9.0.30", {"start": v(-9.43, 13.93) * mm, "end": v(-13.06, 13.93) * mm});
            skLineSegment(sketch, "E17.9.0.31", {"start": v(-9.43, -4.07) * mm, "end": v(-13.06, -4.07) * mm});
            skLineSegment(sketch, "E17.9.0.32", {"start": v(-9.43, -17.57) * mm, "end": v(-13.06, -17.57) * mm});
            skLineSegment(sketch, "E17.9.0.33", {"start": v(-9.43, -27.44) * mm, "end": v(-13.06, -27.44) * mm});
            skLineSegment(sketch, "E17.9.0.34", {"start": v(-9.43, -35.57) * mm, "end": v(-13.06, -35.57) * mm});
            skLineSegment(sketch, "E17.9.0.35", {"start": v(-9.43, 0.43) * mm, "end": v(-13.06, 0.43) * mm});
            skLineSegment(sketch, "E17.9.0.36", {"start": v(-9.43, 13.93) * mm, "end": v(-9.43, 17.56) * mm});
            skLineSegment(sketch, "E17.9.0.37", {"start": v(-9.43, -22.07) * mm, "end": v(-9.43, -18.44) * mm});
            skLineSegment(sketch, "E17.9.0.38", {"start": v(-9.43, -17.57) * mm, "end": v(-9.43, -13.94) * mm});
            skLineSegment(sketch, "E17.9.0.39", {"start": v(-13.06, 4.93) * mm, "end": v(-13.06, 8.56) * mm});
            skLineSegment(sketch, "E17.9.0.40", {"start": v(-9.43, 26.56) * mm, "end": v(-13.06, 26.56) * mm});
            skLineSegment(sketch, "E17.9.0.41", {"start": v(-9.43, 9.43) * mm, "end": v(-13.06, 9.43) * mm});
            skLineSegment(sketch, "E17.9.0.42", {"start": v(-13.06, 22.93) * mm, "end": v(-13.06, 26.56) * mm});
            skLineSegment(sketch, "E17.9.0.43", {"start": v(-9.43, -13.94) * mm, "end": v(-13.06, -13.94) * mm});
            skLineSegment(sketch, "E17.9.0.44", {"start": v(-9.43, -31.94) * mm, "end": v(-13.06, -31.94) * mm});
            skLineSegment(sketch, "E17.9.0.45", {"start": v(-9.43, 22.06) * mm, "end": v(-13.06, 22.06) * mm});
            skLineSegment(sketch, "E17.9.0.46", {"start": v(-9.43, 4.06) * mm, "end": v(-13.06, 4.06) * mm});
            skLineSegment(sketch, "E17.9.0.47", {"start": v(-13.06, 0.43) * mm, "end": v(-13.06, 4.06) * mm});
            skLineSegment(sketch, "E17.9.0.48", {"start": v(-13.06, -35.57) * mm, "end": v(-13.06, -31.94) * mm});
            skLineSegment(sketch, "E17.9.0.49", {"start": v(-9.43, 0.43) * mm, "end": v(-9.43, 4.06) * mm});
            skLineSegment(sketch, "E17.9.0.50", {"start": v(-9.43, -26.57) * mm, "end": v(-13.06, -26.57) * mm});
            skLineSegment(sketch, "E17.9.0.51", {"start": v(-9.43, -35.57) * mm, "end": v(-9.43, -31.94) * mm});
            skLineSegment(sketch, "E17.9.0.52", {"start": v(-9.43, -4.07) * mm, "end": v(-9.43, -0.44) * mm});
            skLineSegment(sketch, "E17.9.0.53", {"start": v(-9.43, -22.07) * mm, "end": v(-13.06, -22.07) * mm});
            skLineSegment(sketch, "E17.9.0.54", {"start": v(-9.43, 18.43) * mm, "end": v(-9.43, 22.06) * mm});
            skLineSegment(sketch, "E17.9.0.55", {"start": v(-9.43, -18.44) * mm, "end": v(-13.06, -18.44) * mm});
            skLineSegment(sketch, "E17.9.0.56", {"start": v(-9.43, -8.57) * mm, "end": v(-9.43, -4.94) * mm});
            skLineSegment(sketch, "E17.9.0.57", {"start": v(-9.43, 18.43) * mm, "end": v(-13.06, 18.43) * mm});
            skLineSegment(sketch, "E17.9.0.58", {"start": v(-9.43, 35.56) * mm, "end": v(-13.06, 35.56) * mm});
            skLineSegment(sketch, "E17.9.0.59", {"start": v(-9.43, 4.93) * mm, "end": v(-9.43, 8.56) * mm});
            skLineSegment(sketch, "E17.9.0.60", {"start": v(-9.43, 27.43) * mm, "end": v(-13.06, 27.43) * mm});
            skLineSegment(sketch, "E17.9.0.61", {"start": v(-9.43, -8.57) * mm, "end": v(-13.06, -8.57) * mm});
            skLineSegment(sketch, "E17.9.0.62", {"start": v(-9.43, 8.56) * mm, "end": v(-13.06, 8.56) * mm});
            skLineSegment(sketch, "E17.9.0.63", {"start": v(-13.06, -17.57) * mm, "end": v(-13.06, -13.94) * mm});
            skLineSegment(sketch, "E17.9.0.64", {"start": v(-9.43, 22.93) * mm, "end": v(-13.06, 22.93) * mm});
            skLineSegment(sketch, "E17.9.0.65", {"start": v(-9.43, 22.93) * mm, "end": v(-9.43, 26.56) * mm});
            skLineSegment(sketch, "E17.10.0.0", {"start": v(-8.56, 27.43) * mm, "end": v(-8.56, 31.06) * mm});
            skLineSegment(sketch, "E17.10.0.1", {"start": v(-4.93, 27.43) * mm, "end": v(-4.93, 31.06) * mm});
            skLineSegment(sketch, "E17.10.0.2", {"start": v(-4.93, -13.07) * mm, "end": v(-4.93, -9.44) * mm});
            skLineSegment(sketch, "E17.10.0.3", {"start": v(-8.56, 9.43) * mm, "end": v(-8.56, 13.06) * mm});
            skLineSegment(sketch, "E17.10.0.4", {"start": v(-8.56, -13.07) * mm, "end": v(-8.56, -9.44) * mm});
            skLineSegment(sketch, "E17.10.0.5", {"start": v(-8.56, -31.07) * mm, "end": v(-8.56, -27.44) * mm});
            skPoint(sketch, "E17.10.0.6", {"position": v(-6.75, 33.75) * mm});
            skLineSegment(sketch, "E17.10.0.7", {"start": v(-4.93, 9.43) * mm, "end": v(-4.93, 13.06) * mm});
            skLineSegment(sketch, "E17.10.0.8", {"start": v(-4.93, -31.07) * mm, "end": v(-4.93, -27.44) * mm});
            skLineSegment(sketch, "E17.10.0.9", {"start": v(-4.93, 31.93) * mm, "end": v(-4.93, 27.43) * mm, "construction": true});
            skLineSegment(sketch, "E17.10.0.10", {"start": v(-4.93, 31.06) * mm, "end": v(-8.56, 31.06) * mm});
            skLineSegment(sketch, "E17.10.0.11", {"start": v(-4.93, 4.93) * mm, "end": v(-8.56, 4.93) * mm});
            skLineSegment(sketch, "E17.10.0.12", {"start": v(-4.93, -13.07) * mm, "end": v(-8.56, -13.07) * mm});
            skLineSegment(sketch, "E17.10.0.13", {"start": v(-4.93, -31.07) * mm, "end": v(-8.56, -31.07) * mm});
            skLineSegment(sketch, "E17.10.0.14", {"start": v(-8.56, 31.93) * mm, "end": v(-8.56, 35.56) * mm});
            skLineSegment(sketch, "E17.10.0.15", {"start": v(-4.93, 31.93) * mm, "end": v(-4.93, 35.56) * mm});
            skLineSegment(sketch, "E17.10.0.16", {"start": v(-4.93, 31.93) * mm, "end": v(-8.56, 31.93) * mm});
            skLineSegment(sketch, "E17.10.0.17", {"start": v(-8.56, 18.43) * mm, "end": v(-8.56, 22.06) * mm});
            skLineSegment(sketch, "E17.10.0.18", {"start": v(-4.93, 13.06) * mm, "end": v(-8.56, 13.06) * mm});
            skLineSegment(sketch, "E17.10.0.19", {"start": v(-4.93, -4.94) * mm, "end": v(-8.56, -4.94) * mm});
            skLineSegment(sketch, "E17.10.0.20", {"start": v(-4.93, -22.94) * mm, "end": v(-8.56, -22.94) * mm});
            skLineSegment(sketch, "E17.10.0.21", {"start": v(-4.93, -26.57) * mm, "end": v(-4.93, -22.94) * mm});
            skLineSegment(sketch, "E17.10.0.22", {"start": v(-8.56, -8.57) * mm, "end": v(-8.56, -4.94) * mm});
            skLineSegment(sketch, "E17.10.0.23", {"start": v(-8.56, -26.57) * mm, "end": v(-8.56, -22.94) * mm});
            skLineSegment(sketch, "E17.10.0.24", {"start": v(-4.93, 17.56) * mm, "end": v(-8.56, 17.56) * mm});
            skLineSegment(sketch, "E17.10.0.25", {"start": v(-4.93, -0.44) * mm, "end": v(-8.56, -0.44) * mm});
            skLineSegment(sketch, "E17.10.0.26", {"start": v(-4.93, -9.44) * mm, "end": v(-8.56, -9.44) * mm});
            skLineSegment(sketch, "E17.10.0.27", {"start": v(-8.56, -22.07) * mm, "end": v(-8.56, -18.44) * mm});
            skLineSegment(sketch, "E17.10.0.28", {"start": v(-8.56, 13.93) * mm, "end": v(-8.56, 17.56) * mm});
            skLineSegment(sketch, "E17.10.0.29", {"start": v(-8.56, -4.07) * mm, "end": v(-8.56, -0.44) * mm});
            skLineSegment(sketch, "E17.10.0.30", {"start": v(-4.93, 13.93) * mm, "end": v(-8.56, 13.93) * mm});
            skLineSegment(sketch, "E17.10.0.31", {"start": v(-4.93, -4.07) * mm, "end": v(-8.56, -4.07) * mm});
            skLineSegment(sketch, "E17.10.0.32", {"start": v(-4.93, -17.57) * mm, "end": v(-8.56, -17.57) * mm});
            skLineSegment(sketch, "E17.10.0.33", {"start": v(-4.93, -27.44) * mm, "end": v(-8.56, -27.44) * mm});
            skLineSegment(sketch, "E17.10.0.34", {"start": v(-4.93, -35.57) * mm, "end": v(-8.56, -35.57) * mm});
            skLineSegment(sketch, "E17.10.0.35", {"start": v(-4.93, 0.43) * mm, "end": v(-8.56, 0.43) * mm});
            skLineSegment(sketch, "E17.10.0.36", {"start": v(-4.93, 13.93) * mm, "end": v(-4.93, 17.56) * mm});
            skLineSegment(sketch, "E17.10.0.37", {"start": v(-4.93, -22.07) * mm, "end": v(-4.93, -18.44) * mm});
            skLineSegment(sketch, "E17.10.0.38", {"start": v(-4.93, -17.57) * mm, "end": v(-4.93, -13.94) * mm});
            skLineSegment(sketch, "E17.10.0.39", {"start": v(-8.56, 4.93) * mm, "end": v(-8.56, 8.56) * mm});
            skLineSegment(sketch, "E17.10.0.40", {"start": v(-4.93, 26.56) * mm, "end": v(-8.56, 26.56) * mm});
            skLineSegment(sketch, "E17.10.0.41", {"start": v(-4.93, 9.43) * mm, "end": v(-8.56, 9.43) * mm});
            skLineSegment(sketch, "E17.10.0.42", {"start": v(-8.56, 22.93) * mm, "end": v(-8.56, 26.56) * mm});
            skLineSegment(sketch, "E17.10.0.43", {"start": v(-4.93, -13.94) * mm, "end": v(-8.56, -13.94) * mm});
            skLineSegment(sketch, "E17.10.0.44", {"start": v(-4.93, -31.94) * mm, "end": v(-8.56, -31.94) * mm});
            skLineSegment(sketch, "E17.10.0.45", {"start": v(-4.93, 22.06) * mm, "end": v(-8.56, 22.06) * mm});
            skLineSegment(sketch, "E17.10.0.46", {"start": v(-4.93, 4.06) * mm, "end": v(-8.56, 4.06) * mm});
            skLineSegment(sketch, "E17.10.0.47", {"start": v(-8.56, 0.43) * mm, "end": v(-8.56, 4.06) * mm});
            skLineSegment(sketch, "E17.10.0.48", {"start": v(-8.56, -35.57) * mm, "end": v(-8.56, -31.94) * mm});
            skLineSegment(sketch, "E17.10.0.49", {"start": v(-4.93, 0.43) * mm, "end": v(-4.93, 4.06) * mm});
            skLineSegment(sketch, "E17.10.0.50", {"start": v(-4.93, -26.57) * mm, "end": v(-8.56, -26.57) * mm});
            skLineSegment(sketch, "E17.10.0.51", {"start": v(-4.93, -35.57) * mm, "end": v(-4.93, -31.94) * mm});
            skLineSegment(sketch, "E17.10.0.52", {"start": v(-4.93, -4.07) * mm, "end": v(-4.93, -0.44) * mm});
            skLineSegment(sketch, "E17.10.0.53", {"start": v(-4.93, -22.07) * mm, "end": v(-8.56, -22.07) * mm});
            skLineSegment(sketch, "E17.10.0.54", {"start": v(-4.93, 18.43) * mm, "end": v(-4.93, 22.06) * mm});
            skLineSegment(sketch, "E17.10.0.55", {"start": v(-4.93, -18.44) * mm, "end": v(-8.56, -18.44) * mm});
            skLineSegment(sketch, "E17.10.0.56", {"start": v(-4.93, -8.57) * mm, "end": v(-4.93, -4.94) * mm});
            skLineSegment(sketch, "E17.10.0.57", {"start": v(-4.93, 18.43) * mm, "end": v(-8.56, 18.43) * mm});
            skLineSegment(sketch, "E17.10.0.58", {"start": v(-4.93, 35.56) * mm, "end": v(-8.56, 35.56) * mm});
            skLineSegment(sketch, "E17.10.0.59", {"start": v(-4.93, 4.93) * mm, "end": v(-4.93, 8.56) * mm});
            skLineSegment(sketch, "E17.10.0.60", {"start": v(-4.93, 27.43) * mm, "end": v(-8.56, 27.43) * mm});
            skLineSegment(sketch, "E17.10.0.61", {"start": v(-4.93, -8.57) * mm, "end": v(-8.56, -8.57) * mm});
            skLineSegment(sketch, "E17.10.0.62", {"start": v(-4.93, 8.56) * mm, "end": v(-8.56, 8.56) * mm});
            skLineSegment(sketch, "E17.10.0.63", {"start": v(-8.56, -17.57) * mm, "end": v(-8.56, -13.94) * mm});
            skLineSegment(sketch, "E17.10.0.64", {"start": v(-4.93, 22.93) * mm, "end": v(-8.56, 22.93) * mm});
            skLineSegment(sketch, "E17.10.0.65", {"start": v(-4.93, 22.93) * mm, "end": v(-4.93, 26.56) * mm});
            skLineSegment(sketch, "E17.11.0.0", {"start": v(-4.06, 27.43) * mm, "end": v(-4.06, 31.06) * mm});
            skLineSegment(sketch, "E17.11.0.1", {"start": v(-0.43, 27.43) * mm, "end": v(-0.43, 31.06) * mm});
            skLineSegment(sketch, "E17.11.0.2", {"start": v(-0.43, -13.07) * mm, "end": v(-0.43, -9.44) * mm});
            skLineSegment(sketch, "E17.11.0.3", {"start": v(-4.06, 9.43) * mm, "end": v(-4.06, 13.06) * mm});
            skLineSegment(sketch, "E17.11.0.4", {"start": v(-4.06, -13.07) * mm, "end": v(-4.06, -9.44) * mm});
            skLineSegment(sketch, "E17.11.0.5", {"start": v(-4.06, -31.07) * mm, "end": v(-4.06, -27.44) * mm});
            skPoint(sketch, "E17.11.0.6", {"position": v(-2.25, 33.75) * mm});
            skLineSegment(sketch, "E17.11.0.7", {"start": v(-0.43, 9.43) * mm, "end": v(-0.43, 13.06) * mm});
            skLineSegment(sketch, "E17.11.0.8", {"start": v(-0.43, -31.07) * mm, "end": v(-0.43, -27.44) * mm});
            skLineSegment(sketch, "E17.11.0.9", {"start": v(-0.43, 31.93) * mm, "end": v(-0.43, 27.43) * mm, "construction": true});
            skLineSegment(sketch, "E17.11.0.10", {"start": v(-0.43, 31.06) * mm, "end": v(-4.06, 31.06) * mm});
            skLineSegment(sketch, "E17.11.0.11", {"start": v(-0.43, 4.93) * mm, "end": v(-4.06, 4.93) * mm});
            skLineSegment(sketch, "E17.11.0.12", {"start": v(-0.43, -13.07) * mm, "end": v(-4.06, -13.07) * mm});
            skLineSegment(sketch, "E17.11.0.13", {"start": v(-0.43, -31.07) * mm, "end": v(-4.06, -31.07) * mm});
            skLineSegment(sketch, "E17.11.0.14", {"start": v(-4.06, 31.93) * mm, "end": v(-4.06, 35.56) * mm});
            skLineSegment(sketch, "E17.11.0.15", {"start": v(-0.43, 31.93) * mm, "end": v(-0.43, 35.56) * mm});
            skLineSegment(sketch, "E17.11.0.16", {"start": v(-0.43, 31.93) * mm, "end": v(-4.06, 31.93) * mm});
            skLineSegment(sketch, "E17.11.0.17", {"start": v(-4.06, 18.43) * mm, "end": v(-4.06, 22.06) * mm});
            skLineSegment(sketch, "E17.11.0.18", {"start": v(-0.43, 13.06) * mm, "end": v(-4.06, 13.06) * mm});
            skLineSegment(sketch, "E17.11.0.19", {"start": v(-0.43, -4.94) * mm, "end": v(-4.06, -4.94) * mm});
            skLineSegment(sketch, "E17.11.0.20", {"start": v(-0.43, -22.94) * mm, "end": v(-4.06, -22.94) * mm});
            skLineSegment(sketch, "E17.11.0.21", {"start": v(-0.43, -26.57) * mm, "end": v(-0.43, -22.94) * mm});
            skLineSegment(sketch, "E17.11.0.22", {"start": v(-4.06, -8.57) * mm, "end": v(-4.06, -4.94) * mm});
            skLineSegment(sketch, "E17.11.0.23", {"start": v(-4.06, -26.57) * mm, "end": v(-4.06, -22.94) * mm});
            skLineSegment(sketch, "E17.11.0.24", {"start": v(-0.43, 17.56) * mm, "end": v(-4.06, 17.56) * mm});
            skLineSegment(sketch, "E17.11.0.25", {"start": v(-0.43, -0.44) * mm, "end": v(-4.06, -0.44) * mm});
            skLineSegment(sketch, "E17.11.0.26", {"start": v(-0.43, -9.44) * mm, "end": v(-4.06, -9.44) * mm});
            skLineSegment(sketch, "E17.11.0.27", {"start": v(-4.06, -22.07) * mm, "end": v(-4.06, -18.44) * mm});
            skLineSegment(sketch, "E17.11.0.28", {"start": v(-4.06, 13.93) * mm, "end": v(-4.06, 17.56) * mm});
            skLineSegment(sketch, "E17.11.0.29", {"start": v(-4.06, -4.07) * mm, "end": v(-4.06, -0.44) * mm});
            skLineSegment(sketch, "E17.11.0.30", {"start": v(-0.43, 13.93) * mm, "end": v(-4.06, 13.93) * mm});
            skLineSegment(sketch, "E17.11.0.31", {"start": v(-0.43, -4.07) * mm, "end": v(-4.06, -4.07) * mm});
            skLineSegment(sketch, "E17.11.0.32", {"start": v(-0.43, -17.57) * mm, "end": v(-4.06, -17.57) * mm});
            skLineSegment(sketch, "E17.11.0.33", {"start": v(-0.43, -27.44) * mm, "end": v(-4.06, -27.44) * mm});
            skLineSegment(sketch, "E17.11.0.34", {"start": v(-0.43, -35.57) * mm, "end": v(-4.06, -35.57) * mm});
            skLineSegment(sketch, "E17.11.0.35", {"start": v(-0.43, 0.43) * mm, "end": v(-4.06, 0.43) * mm});
            skLineSegment(sketch, "E17.11.0.36", {"start": v(-0.43, 13.93) * mm, "end": v(-0.43, 17.56) * mm});
            skLineSegment(sketch, "E17.11.0.37", {"start": v(-0.43, -22.07) * mm, "end": v(-0.43, -18.44) * mm});
            skLineSegment(sketch, "E17.11.0.38", {"start": v(-0.43, -17.57) * mm, "end": v(-0.43, -13.94) * mm});
            skLineSegment(sketch, "E17.11.0.39", {"start": v(-4.06, 4.93) * mm, "end": v(-4.06, 8.56) * mm});
            skLineSegment(sketch, "E17.11.0.40", {"start": v(-0.43, 26.56) * mm, "end": v(-4.06, 26.56) * mm});
            skLineSegment(sketch, "E17.11.0.41", {"start": v(-0.43, 9.43) * mm, "end": v(-4.06, 9.43) * mm});
            skLineSegment(sketch, "E17.11.0.42", {"start": v(-4.06, 22.93) * mm, "end": v(-4.06, 26.56) * mm});
            skLineSegment(sketch, "E17.11.0.43", {"start": v(-0.43, -13.94) * mm, "end": v(-4.06, -13.94) * mm});
            skLineSegment(sketch, "E17.11.0.44", {"start": v(-0.43, -31.94) * mm, "end": v(-4.06, -31.94) * mm});
            skLineSegment(sketch, "E17.11.0.45", {"start": v(-0.43, 22.06) * mm, "end": v(-4.06, 22.06) * mm});
            skLineSegment(sketch, "E17.11.0.46", {"start": v(-0.43, 4.06) * mm, "end": v(-4.06, 4.06) * mm});
            skLineSegment(sketch, "E17.11.0.47", {"start": v(-4.06, 0.43) * mm, "end": v(-4.06, 4.06) * mm});
            skLineSegment(sketch, "E17.11.0.48", {"start": v(-4.06, -35.57) * mm, "end": v(-4.06, -31.94) * mm});
            skLineSegment(sketch, "E17.11.0.49", {"start": v(-0.43, 0.43) * mm, "end": v(-0.43, 4.06) * mm});
            skLineSegment(sketch, "E17.11.0.50", {"start": v(-0.43, -26.57) * mm, "end": v(-4.06, -26.57) * mm});
            skLineSegment(sketch, "E17.11.0.51", {"start": v(-0.43, -35.57) * mm, "end": v(-0.43, -31.94) * mm});
            skLineSegment(sketch, "E17.11.0.52", {"start": v(-0.43, -4.07) * mm, "end": v(-0.43, -0.44) * mm});
            skLineSegment(sketch, "E17.11.0.53", {"start": v(-0.43, -22.07) * mm, "end": v(-4.06, -22.07) * mm});
            skLineSegment(sketch, "E17.11.0.54", {"start": v(-0.43, 18.43) * mm, "end": v(-0.43, 22.06) * mm});
            skLineSegment(sketch, "E17.11.0.55", {"start": v(-0.43, -18.44) * mm, "end": v(-4.06, -18.44) * mm});
            skLineSegment(sketch, "E17.11.0.56", {"start": v(-0.43, -8.57) * mm, "end": v(-0.43, -4.94) * mm});
            skLineSegment(sketch, "E17.11.0.57", {"start": v(-0.43, 18.43) * mm, "end": v(-4.06, 18.43) * mm});
            skLineSegment(sketch, "E17.11.0.58", {"start": v(-0.43, 35.56) * mm, "end": v(-4.06, 35.56) * mm});
            skLineSegment(sketch, "E17.11.0.59", {"start": v(-0.43, 4.93) * mm, "end": v(-0.43, 8.56) * mm});
            skLineSegment(sketch, "E17.11.0.60", {"start": v(-0.43, 27.43) * mm, "end": v(-4.06, 27.43) * mm});
            skLineSegment(sketch, "E17.11.0.61", {"start": v(-0.43, -8.57) * mm, "end": v(-4.06, -8.57) * mm});
            skLineSegment(sketch, "E17.11.0.62", {"start": v(-0.43, 8.56) * mm, "end": v(-4.06, 8.56) * mm});
            skLineSegment(sketch, "E17.11.0.63", {"start": v(-4.06, -17.57) * mm, "end": v(-4.06, -13.94) * mm});
            skLineSegment(sketch, "E17.11.0.64", {"start": v(-0.43, 22.93) * mm, "end": v(-4.06, 22.93) * mm});
            skLineSegment(sketch, "E17.11.0.65", {"start": v(-0.43, 22.93) * mm, "end": v(-0.43, 26.56) * mm});
            skLineSegment(sketch, "E17.12.0.0", {"start": v(0.44, 27.43) * mm, "end": v(0.44, 31.06) * mm});
            skLineSegment(sketch, "E17.12.0.1", {"start": v(4.07, 27.43) * mm, "end": v(4.07, 31.06) * mm});
            skLineSegment(sketch, "E17.12.0.2", {"start": v(4.07, -13.07) * mm, "end": v(4.07, -9.44) * mm});
            skLineSegment(sketch, "E17.12.0.3", {"start": v(0.44, 9.43) * mm, "end": v(0.44, 13.06) * mm});
            skLineSegment(sketch, "E17.12.0.4", {"start": v(0.44, -13.07) * mm, "end": v(0.44, -9.44) * mm});
            skLineSegment(sketch, "E17.12.0.5", {"start": v(0.44, -31.07) * mm, "end": v(0.44, -27.44) * mm});
            skPoint(sketch, "E17.12.0.6", {"position": v(2.25, 33.75) * mm});
            skLineSegment(sketch, "E17.12.0.7", {"start": v(4.07, 9.43) * mm, "end": v(4.07, 13.06) * mm});
            skLineSegment(sketch, "E17.12.0.8", {"start": v(4.07, -31.07) * mm, "end": v(4.07, -27.44) * mm});
            skLineSegment(sketch, "E17.12.0.9", {"start": v(4.07, 31.93) * mm, "end": v(4.07, 27.43) * mm, "construction": true});
            skLineSegment(sketch, "E17.12.0.10", {"start": v(4.07, 31.06) * mm, "end": v(0.44, 31.06) * mm});
            skLineSegment(sketch, "E17.12.0.11", {"start": v(4.07, 4.93) * mm, "end": v(0.44, 4.93) * mm});
            skLineSegment(sketch, "E17.12.0.12", {"start": v(4.07, -13.07) * mm, "end": v(0.44, -13.07) * mm});
            skLineSegment(sketch, "E17.12.0.13", {"start": v(4.07, -31.07) * mm, "end": v(0.44, -31.07) * mm});
            skLineSegment(sketch, "E17.12.0.14", {"start": v(0.44, 31.93) * mm, "end": v(0.44, 35.56) * mm});
            skLineSegment(sketch, "E17.12.0.15", {"start": v(4.07, 31.93) * mm, "end": v(4.07, 35.56) * mm});
            skLineSegment(sketch, "E17.12.0.16", {"start": v(4.07, 31.93) * mm, "end": v(0.44, 31.93) * mm});
            skLineSegment(sketch, "E17.12.0.17", {"start": v(0.44, 18.43) * mm, "end": v(0.44, 22.06) * mm});
            skLineSegment(sketch, "E17.12.0.18", {"start": v(4.07, 13.06) * mm, "end": v(0.44, 13.06) * mm});
            skLineSegment(sketch, "E17.12.0.19", {"start": v(4.07, -4.94) * mm, "end": v(0.44, -4.94) * mm});
            skLineSegment(sketch, "E17.12.0.20", {"start": v(4.07, -22.94) * mm, "end": v(0.44, -22.94) * mm});
            skLineSegment(sketch, "E17.12.0.21", {"start": v(4.07, -26.57) * mm, "end": v(4.07, -22.94) * mm});
            skLineSegment(sketch, "E17.12.0.22", {"start": v(0.44, -8.57) * mm, "end": v(0.44, -4.94) * mm});
            skLineSegment(sketch, "E17.12.0.23", {"start": v(0.44, -26.57) * mm, "end": v(0.44, -22.94) * mm});
            skLineSegment(sketch, "E17.12.0.24", {"start": v(4.07, 17.56) * mm, "end": v(0.44, 17.56) * mm});
            skLineSegment(sketch, "E17.12.0.25", {"start": v(4.07, -0.44) * mm, "end": v(0.44, -0.44) * mm});
            skLineSegment(sketch, "E17.12.0.26", {"start": v(4.07, -9.44) * mm, "end": v(0.44, -9.44) * mm});
            skLineSegment(sketch, "E17.12.0.27", {"start": v(0.44, -22.07) * mm, "end": v(0.44, -18.44) * mm});
            skLineSegment(sketch, "E17.12.0.28", {"start": v(0.44, 13.93) * mm, "end": v(0.44, 17.56) * mm});
            skLineSegment(sketch, "E17.12.0.29", {"start": v(0.44, -4.07) * mm, "end": v(0.44, -0.44) * mm});
            skLineSegment(sketch, "E17.12.0.30", {"start": v(4.07, 13.93) * mm, "end": v(0.44, 13.93) * mm});
            skLineSegment(sketch, "E17.12.0.31", {"start": v(4.07, -4.07) * mm, "end": v(0.44, -4.07) * mm});
            skLineSegment(sketch, "E17.12.0.32", {"start": v(4.07, -17.57) * mm, "end": v(0.44, -17.57) * mm});
            skLineSegment(sketch, "E17.12.0.33", {"start": v(4.07, -27.44) * mm, "end": v(0.44, -27.44) * mm});
            skLineSegment(sketch, "E17.12.0.34", {"start": v(4.07, -35.57) * mm, "end": v(0.44, -35.57) * mm});
            skLineSegment(sketch, "E17.12.0.35", {"start": v(4.07, 0.43) * mm, "end": v(0.44, 0.43) * mm});
            skLineSegment(sketch, "E17.12.0.36", {"start": v(4.07, 13.93) * mm, "end": v(4.07, 17.56) * mm});
            skLineSegment(sketch, "E17.12.0.37", {"start": v(4.07, -22.07) * mm, "end": v(4.07, -18.44) * mm});
            skLineSegment(sketch, "E17.12.0.38", {"start": v(4.07, -17.57) * mm, "end": v(4.07, -13.94) * mm});
            skLineSegment(sketch, "E17.12.0.39", {"start": v(0.44, 4.93) * mm, "end": v(0.44, 8.56) * mm});
            skLineSegment(sketch, "E17.12.0.40", {"start": v(4.07, 26.56) * mm, "end": v(0.44, 26.56) * mm});
            skLineSegment(sketch, "E17.12.0.41", {"start": v(4.07, 9.43) * mm, "end": v(0.44, 9.43) * mm});
            skLineSegment(sketch, "E17.12.0.42", {"start": v(0.44, 22.93) * mm, "end": v(0.44, 26.56) * mm});
            skLineSegment(sketch, "E17.12.0.43", {"start": v(4.07, -13.94) * mm, "end": v(0.44, -13.94) * mm});
            skLineSegment(sketch, "E17.12.0.44", {"start": v(4.07, -31.94) * mm, "end": v(0.44, -31.94) * mm});
            skLineSegment(sketch, "E17.12.0.45", {"start": v(4.07, 22.06) * mm, "end": v(0.44, 22.06) * mm});
            skLineSegment(sketch, "E17.12.0.46", {"start": v(4.07, 4.06) * mm, "end": v(0.44, 4.06) * mm});
            skLineSegment(sketch, "E17.12.0.47", {"start": v(0.44, 0.43) * mm, "end": v(0.44, 4.06) * mm});
            skLineSegment(sketch, "E17.12.0.48", {"start": v(0.44, -35.57) * mm, "end": v(0.44, -31.94) * mm});
            skLineSegment(sketch, "E17.12.0.49", {"start": v(4.07, 0.43) * mm, "end": v(4.07, 4.06) * mm});
            skLineSegment(sketch, "E17.12.0.50", {"start": v(4.07, -26.57) * mm, "end": v(0.44, -26.57) * mm});
            skLineSegment(sketch, "E17.12.0.51", {"start": v(4.07, -35.57) * mm, "end": v(4.07, -31.94) * mm});
            skLineSegment(sketch, "E17.12.0.52", {"start": v(4.07, -4.07) * mm, "end": v(4.07, -0.44) * mm});
            skLineSegment(sketch, "E17.12.0.53", {"start": v(4.07, -22.07) * mm, "end": v(0.44, -22.07) * mm});
            skLineSegment(sketch, "E17.12.0.54", {"start": v(4.07, 18.43) * mm, "end": v(4.07, 22.06) * mm});
            skLineSegment(sketch, "E17.12.0.55", {"start": v(4.07, -18.44) * mm, "end": v(0.44, -18.44) * mm});
            skLineSegment(sketch, "E17.12.0.56", {"start": v(4.07, -8.57) * mm, "end": v(4.07, -4.94) * mm});
            skLineSegment(sketch, "E17.12.0.57", {"start": v(4.07, 18.43) * mm, "end": v(0.44, 18.43) * mm});
            skLineSegment(sketch, "E17.12.0.58", {"start": v(4.07, 35.56) * mm, "end": v(0.44, 35.56) * mm});
            skLineSegment(sketch, "E17.12.0.59", {"start": v(4.07, 4.93) * mm, "end": v(4.07, 8.56) * mm});
            skLineSegment(sketch, "E17.12.0.60", {"start": v(4.07, 27.43) * mm, "end": v(0.44, 27.43) * mm});
            skLineSegment(sketch, "E17.12.0.61", {"start": v(4.07, -8.57) * mm, "end": v(0.44, -8.57) * mm});
            skLineSegment(sketch, "E17.12.0.62", {"start": v(4.07, 8.56) * mm, "end": v(0.44, 8.56) * mm});
            skLineSegment(sketch, "E17.12.0.63", {"start": v(0.44, -17.57) * mm, "end": v(0.44, -13.94) * mm});
            skLineSegment(sketch, "E17.12.0.64", {"start": v(4.07, 22.93) * mm, "end": v(0.44, 22.93) * mm});
            skLineSegment(sketch, "E17.12.0.65", {"start": v(4.07, 22.93) * mm, "end": v(4.07, 26.56) * mm});
            skLineSegment(sketch, "E17.13.0.0", {"start": v(4.94, 27.43) * mm, "end": v(4.94, 31.06) * mm});
            skLineSegment(sketch, "E17.13.0.1", {"start": v(8.57, 27.43) * mm, "end": v(8.57, 31.06) * mm});
            skLineSegment(sketch, "E17.13.0.2", {"start": v(8.57, -13.07) * mm, "end": v(8.57, -9.44) * mm});
            skLineSegment(sketch, "E17.13.0.3", {"start": v(4.94, 9.43) * mm, "end": v(4.94, 13.06) * mm});
            skLineSegment(sketch, "E17.13.0.4", {"start": v(4.94, -13.07) * mm, "end": v(4.94, -9.44) * mm});
            skLineSegment(sketch, "E17.13.0.5", {"start": v(4.94, -31.07) * mm, "end": v(4.94, -27.44) * mm});
            skPoint(sketch, "E17.13.0.6", {"position": v(6.75, 33.75) * mm});
            skLineSegment(sketch, "E17.13.0.7", {"start": v(8.57, 9.43) * mm, "end": v(8.57, 13.06) * mm});
            skLineSegment(sketch, "E17.13.0.8", {"start": v(8.57, -31.07) * mm, "end": v(8.57, -27.44) * mm});
            skLineSegment(sketch, "E17.13.0.9", {"start": v(8.57, 31.93) * mm, "end": v(8.57, 27.43) * mm, "construction": true});
            skLineSegment(sketch, "E17.13.0.10", {"start": v(8.57, 31.06) * mm, "end": v(4.94, 31.06) * mm});
            skLineSegment(sketch, "E17.13.0.11", {"start": v(8.57, 4.93) * mm, "end": v(4.94, 4.93) * mm});
            skLineSegment(sketch, "E17.13.0.12", {"start": v(8.57, -13.07) * mm, "end": v(4.94, -13.07) * mm});
            skLineSegment(sketch, "E17.13.0.13", {"start": v(8.57, -31.07) * mm, "end": v(4.94, -31.07) * mm});
            skLineSegment(sketch, "E17.13.0.14", {"start": v(4.94, 31.93) * mm, "end": v(4.94, 35.56) * mm});
            skLineSegment(sketch, "E17.13.0.15", {"start": v(8.57, 31.93) * mm, "end": v(8.57, 35.56) * mm});
            skLineSegment(sketch, "E17.13.0.16", {"start": v(8.57, 31.93) * mm, "end": v(4.94, 31.93) * mm});
            skLineSegment(sketch, "E17.13.0.17", {"start": v(4.94, 18.43) * mm, "end": v(4.94, 22.06) * mm});
            skLineSegment(sketch, "E17.13.0.18", {"start": v(8.57, 13.06) * mm, "end": v(4.94, 13.06) * mm});
            skLineSegment(sketch, "E17.13.0.19", {"start": v(8.57, -4.94) * mm, "end": v(4.94, -4.94) * mm});
            skLineSegment(sketch, "E17.13.0.20", {"start": v(8.57, -22.94) * mm, "end": v(4.94, -22.94) * mm});
            skLineSegment(sketch, "E17.13.0.21", {"start": v(8.57, -26.57) * mm, "end": v(8.57, -22.94) * mm});
            skLineSegment(sketch, "E17.13.0.22", {"start": v(4.94, -8.57) * mm, "end": v(4.94, -4.94) * mm});
            skLineSegment(sketch, "E17.13.0.23", {"start": v(4.94, -26.57) * mm, "end": v(4.94, -22.94) * mm});
            skLineSegment(sketch, "E17.13.0.24", {"start": v(8.57, 17.56) * mm, "end": v(4.94, 17.56) * mm});
            skLineSegment(sketch, "E17.13.0.25", {"start": v(8.57, -0.44) * mm, "end": v(4.94, -0.44) * mm});
            skLineSegment(sketch, "E17.13.0.26", {"start": v(8.57, -9.44) * mm, "end": v(4.94, -9.44) * mm});
            skLineSegment(sketch, "E17.13.0.27", {"start": v(4.94, -22.07) * mm, "end": v(4.94, -18.44) * mm});
            skLineSegment(sketch, "E17.13.0.28", {"start": v(4.94, 13.93) * mm, "end": v(4.94, 17.56) * mm});
            skLineSegment(sketch, "E17.13.0.29", {"start": v(4.94, -4.07) * mm, "end": v(4.94, -0.44) * mm});
            skLineSegment(sketch, "E17.13.0.30", {"start": v(8.57, 13.93) * mm, "end": v(4.94, 13.93) * mm});
            skLineSegment(sketch, "E17.13.0.31", {"start": v(8.57, -4.07) * mm, "end": v(4.94, -4.07) * mm});
            skLineSegment(sketch, "E17.13.0.32", {"start": v(8.57, -17.57) * mm, "end": v(4.94, -17.57) * mm});
            skLineSegment(sketch, "E17.13.0.33", {"start": v(8.57, -27.44) * mm, "end": v(4.94, -27.44) * mm});
            skLineSegment(sketch, "E17.13.0.34", {"start": v(8.57, -35.57) * mm, "end": v(4.94, -35.57) * mm});
            skLineSegment(sketch, "E17.13.0.35", {"start": v(8.57, 0.43) * mm, "end": v(4.94, 0.43) * mm});
            skLineSegment(sketch, "E17.13.0.36", {"start": v(8.57, 13.93) * mm, "end": v(8.57, 17.56) * mm});
            skLineSegment(sketch, "E17.13.0.37", {"start": v(8.57, -22.07) * mm, "end": v(8.57, -18.44) * mm});
            skLineSegment(sketch, "E17.13.0.38", {"start": v(8.57, -17.57) * mm, "end": v(8.57, -13.94) * mm});
            skLineSegment(sketch, "E17.13.0.39", {"start": v(4.94, 4.93) * mm, "end": v(4.94, 8.56) * mm});
            skLineSegment(sketch, "E17.13.0.40", {"start": v(8.57, 26.56) * mm, "end": v(4.94, 26.56) * mm});
            skLineSegment(sketch, "E17.13.0.41", {"start": v(8.57, 9.43) * mm, "end": v(4.94, 9.43) * mm});
            skLineSegment(sketch, "E17.13.0.42", {"start": v(4.94, 22.93) * mm, "end": v(4.94, 26.56) * mm});
            skLineSegment(sketch, "E17.13.0.43", {"start": v(8.57, -13.94) * mm, "end": v(4.94, -13.94) * mm});
            skLineSegment(sketch, "E17.13.0.44", {"start": v(8.57, -31.94) * mm, "end": v(4.94, -31.94) * mm});
            skLineSegment(sketch, "E17.13.0.45", {"start": v(8.57, 22.06) * mm, "end": v(4.94, 22.06) * mm});
            skLineSegment(sketch, "E17.13.0.46", {"start": v(8.57, 4.06) * mm, "end": v(4.94, 4.06) * mm});
            skLineSegment(sketch, "E17.13.0.47", {"start": v(4.94, 0.43) * mm, "end": v(4.94, 4.06) * mm});
            skLineSegment(sketch, "E17.13.0.48", {"start": v(4.94, -35.57) * mm, "end": v(4.94, -31.94) * mm});
            skLineSegment(sketch, "E17.13.0.49", {"start": v(8.57, 0.43) * mm, "end": v(8.57, 4.06) * mm});
            skLineSegment(sketch, "E17.13.0.50", {"start": v(8.57, -26.57) * mm, "end": v(4.94, -26.57) * mm});
            skLineSegment(sketch, "E17.13.0.51", {"start": v(8.57, -35.57) * mm, "end": v(8.57, -31.94) * mm});
            skLineSegment(sketch, "E17.13.0.52", {"start": v(8.57, -4.07) * mm, "end": v(8.57, -0.44) * mm});
            skLineSegment(sketch, "E17.13.0.53", {"start": v(8.57, -22.07) * mm, "end": v(4.94, -22.07) * mm});
            skLineSegment(sketch, "E17.13.0.54", {"start": v(8.57, 18.43) * mm, "end": v(8.57, 22.06) * mm});
            skLineSegment(sketch, "E17.13.0.55", {"start": v(8.57, -18.44) * mm, "end": v(4.94, -18.44) * mm});
            skLineSegment(sketch, "E17.13.0.56", {"start": v(8.57, -8.57) * mm, "end": v(8.57, -4.94) * mm});
            skLineSegment(sketch, "E17.13.0.57", {"start": v(8.57, 18.43) * mm, "end": v(4.94, 18.43) * mm});
            skLineSegment(sketch, "E17.13.0.58", {"start": v(8.57, 35.56) * mm, "end": v(4.94, 35.56) * mm});
            skLineSegment(sketch, "E17.13.0.59", {"start": v(8.57, 4.93) * mm, "end": v(8.57, 8.56) * mm});
            skLineSegment(sketch, "E17.13.0.60", {"start": v(8.57, 27.43) * mm, "end": v(4.94, 27.43) * mm});
            skLineSegment(sketch, "E17.13.0.61", {"start": v(8.57, -8.57) * mm, "end": v(4.94, -8.57) * mm});
            skLineSegment(sketch, "E17.13.0.62", {"start": v(8.57, 8.56) * mm, "end": v(4.94, 8.56) * mm});
            skLineSegment(sketch, "E17.13.0.63", {"start": v(4.94, -17.57) * mm, "end": v(4.94, -13.94) * mm});
            skLineSegment(sketch, "E17.13.0.64", {"start": v(8.57, 22.93) * mm, "end": v(4.94, 22.93) * mm});
            skLineSegment(sketch, "E17.13.0.65", {"start": v(8.57, 22.93) * mm, "end": v(8.57, 26.56) * mm});
            skLineSegment(sketch, "E17.14.0.0", {"start": v(9.44, 27.43) * mm, "end": v(9.44, 31.06) * mm});
            skLineSegment(sketch, "E17.14.0.1", {"start": v(13.07, 27.43) * mm, "end": v(13.07, 31.06) * mm});
            skLineSegment(sketch, "E17.14.0.2", {"start": v(13.07, -13.07) * mm, "end": v(13.07, -9.44) * mm});
            skLineSegment(sketch, "E17.14.0.3", {"start": v(9.44, 9.43) * mm, "end": v(9.44, 13.06) * mm});
            skLineSegment(sketch, "E17.14.0.4", {"start": v(9.44, -13.07) * mm, "end": v(9.44, -9.44) * mm});
            skLineSegment(sketch, "E17.14.0.5", {"start": v(9.44, -31.07) * mm, "end": v(9.44, -27.44) * mm});
            skPoint(sketch, "E17.14.0.6", {"position": v(11.25, 33.75) * mm});
            skLineSegment(sketch, "E17.14.0.7", {"start": v(13.07, 9.43) * mm, "end": v(13.07, 13.06) * mm});
            skLineSegment(sketch, "E17.14.0.8", {"start": v(13.07, -31.07) * mm, "end": v(13.07, -27.44) * mm});
            skLineSegment(sketch, "E17.14.0.9", {"start": v(13.07, 31.93) * mm, "end": v(13.07, 27.43) * mm, "construction": true});
            skLineSegment(sketch, "E17.14.0.10", {"start": v(13.07, 31.06) * mm, "end": v(9.44, 31.06) * mm});
            skLineSegment(sketch, "E17.14.0.11", {"start": v(13.07, 4.93) * mm, "end": v(9.44, 4.93) * mm});
            skLineSegment(sketch, "E17.14.0.12", {"start": v(13.07, -13.07) * mm, "end": v(9.44, -13.07) * mm});
            skLineSegment(sketch, "E17.14.0.13", {"start": v(13.07, -31.07) * mm, "end": v(9.44, -31.07) * mm});
            skLineSegment(sketch, "E17.14.0.14", {"start": v(9.44, 31.93) * mm, "end": v(9.44, 35.56) * mm});
            skLineSegment(sketch, "E17.14.0.15", {"start": v(13.07, 31.93) * mm, "end": v(13.07, 35.56) * mm});
            skLineSegment(sketch, "E17.14.0.16", {"start": v(13.07, 31.93) * mm, "end": v(9.44, 31.93) * mm});
            skLineSegment(sketch, "E17.14.0.17", {"start": v(9.44, 18.43) * mm, "end": v(9.44, 22.06) * mm});
            skLineSegment(sketch, "E17.14.0.18", {"start": v(13.07, 13.06) * mm, "end": v(9.44, 13.06) * mm});
            skLineSegment(sketch, "E17.14.0.19", {"start": v(13.07, -4.94) * mm, "end": v(9.44, -4.94) * mm});
            skLineSegment(sketch, "E17.14.0.20", {"start": v(13.07, -22.94) * mm, "end": v(9.44, -22.94) * mm});
            skLineSegment(sketch, "E17.14.0.21", {"start": v(13.07, -26.57) * mm, "end": v(13.07, -22.94) * mm});
            skLineSegment(sketch, "E17.14.0.22", {"start": v(9.44, -8.57) * mm, "end": v(9.44, -4.94) * mm});
            skLineSegment(sketch, "E17.14.0.23", {"start": v(9.44, -26.57) * mm, "end": v(9.44, -22.94) * mm});
            skLineSegment(sketch, "E17.14.0.24", {"start": v(13.07, 17.56) * mm, "end": v(9.44, 17.56) * mm});
            skLineSegment(sketch, "E17.14.0.25", {"start": v(13.07, -0.44) * mm, "end": v(9.44, -0.44) * mm});
            skLineSegment(sketch, "E17.14.0.26", {"start": v(13.07, -9.44) * mm, "end": v(9.44, -9.44) * mm});
            skLineSegment(sketch, "E17.14.0.27", {"start": v(9.44, -22.07) * mm, "end": v(9.44, -18.44) * mm});
            skLineSegment(sketch, "E17.14.0.28", {"start": v(9.44, 13.93) * mm, "end": v(9.44, 17.56) * mm});
            skLineSegment(sketch, "E17.14.0.29", {"start": v(9.44, -4.07) * mm, "end": v(9.44, -0.44) * mm});
            skLineSegment(sketch, "E17.14.0.30", {"start": v(13.07, 13.93) * mm, "end": v(9.44, 13.93) * mm});
            skLineSegment(sketch, "E17.14.0.31", {"start": v(13.07, -4.07) * mm, "end": v(9.44, -4.07) * mm});
            skLineSegment(sketch, "E17.14.0.32", {"start": v(13.07, -17.57) * mm, "end": v(9.44, -17.57) * mm});
            skLineSegment(sketch, "E17.14.0.33", {"start": v(13.07, -27.44) * mm, "end": v(9.44, -27.44) * mm});
            skLineSegment(sketch, "E17.14.0.34", {"start": v(13.07, -35.57) * mm, "end": v(9.44, -35.57) * mm});
            skLineSegment(sketch, "E17.14.0.35", {"start": v(13.07, 0.43) * mm, "end": v(9.44, 0.43) * mm});
            skLineSegment(sketch, "E17.14.0.36", {"start": v(13.07, 13.93) * mm, "end": v(13.07, 17.56) * mm});
            skLineSegment(sketch, "E17.14.0.37", {"start": v(13.07, -22.07) * mm, "end": v(13.07, -18.44) * mm});
            skLineSegment(sketch, "E17.14.0.38", {"start": v(13.07, -17.57) * mm, "end": v(13.07, -13.94) * mm});
            skLineSegment(sketch, "E17.14.0.39", {"start": v(9.44, 4.93) * mm, "end": v(9.44, 8.56) * mm});
            skLineSegment(sketch, "E17.14.0.40", {"start": v(13.07, 26.56) * mm, "end": v(9.44, 26.56) * mm});
            skLineSegment(sketch, "E17.14.0.41", {"start": v(13.07, 9.43) * mm, "end": v(9.44, 9.43) * mm});
            skLineSegment(sketch, "E17.14.0.42", {"start": v(9.44, 22.93) * mm, "end": v(9.44, 26.56) * mm});
            skLineSegment(sketch, "E17.14.0.43", {"start": v(13.07, -13.94) * mm, "end": v(9.44, -13.94) * mm});
            skLineSegment(sketch, "E17.14.0.44", {"start": v(13.07, -31.94) * mm, "end": v(9.44, -31.94) * mm});
            skLineSegment(sketch, "E17.14.0.45", {"start": v(13.07, 22.06) * mm, "end": v(9.44, 22.06) * mm});
            skLineSegment(sketch, "E17.14.0.46", {"start": v(13.07, 4.06) * mm, "end": v(9.44, 4.06) * mm});
            skLineSegment(sketch, "E17.14.0.47", {"start": v(9.44, 0.43) * mm, "end": v(9.44, 4.06) * mm});
            skLineSegment(sketch, "E17.14.0.48", {"start": v(9.44, -35.57) * mm, "end": v(9.44, -31.94) * mm});
            skLineSegment(sketch, "E17.14.0.49", {"start": v(13.07, 0.43) * mm, "end": v(13.07, 4.06) * mm});
            skLineSegment(sketch, "E17.14.0.50", {"start": v(13.07, -26.57) * mm, "end": v(9.44, -26.57) * mm});
            skLineSegment(sketch, "E17.14.0.51", {"start": v(13.07, -35.57) * mm, "end": v(13.07, -31.94) * mm});
            skLineSegment(sketch, "E17.14.0.52", {"start": v(13.07, -4.07) * mm, "end": v(13.07, -0.44) * mm});
            skLineSegment(sketch, "E17.14.0.53", {"start": v(13.07, -22.07) * mm, "end": v(9.44, -22.07) * mm});
            skLineSegment(sketch, "E17.14.0.54", {"start": v(13.07, 18.43) * mm, "end": v(13.07, 22.06) * mm});
            skLineSegment(sketch, "E17.14.0.55", {"start": v(13.07, -18.44) * mm, "end": v(9.44, -18.44) * mm});
            skLineSegment(sketch, "E17.14.0.56", {"start": v(13.07, -8.57) * mm, "end": v(13.07, -4.94) * mm});
            skLineSegment(sketch, "E17.14.0.57", {"start": v(13.07, 18.43) * mm, "end": v(9.44, 18.43) * mm});
            skLineSegment(sketch, "E17.14.0.58", {"start": v(13.07, 35.56) * mm, "end": v(9.44, 35.56) * mm});
            skLineSegment(sketch, "E17.14.0.59", {"start": v(13.07, 4.93) * mm, "end": v(13.07, 8.56) * mm});
            skLineSegment(sketch, "E17.14.0.60", {"start": v(13.07, 27.43) * mm, "end": v(9.44, 27.43) * mm});
            skLineSegment(sketch, "E17.14.0.61", {"start": v(13.07, -8.57) * mm, "end": v(9.44, -8.57) * mm});
            skLineSegment(sketch, "E17.14.0.62", {"start": v(13.07, 8.56) * mm, "end": v(9.44, 8.56) * mm});
            skLineSegment(sketch, "E17.14.0.63", {"start": v(9.44, -17.57) * mm, "end": v(9.44, -13.94) * mm});
            skLineSegment(sketch, "E17.14.0.64", {"start": v(13.07, 22.93) * mm, "end": v(9.44, 22.93) * mm});
            skLineSegment(sketch, "E17.14.0.65", {"start": v(13.07, 22.93) * mm, "end": v(13.07, 26.56) * mm});
            skLineSegment(sketch, "E17.15.0.0", {"start": v(13.94, 27.43) * mm, "end": v(13.94, 31.06) * mm});
            skLineSegment(sketch, "E17.15.0.1", {"start": v(17.57, 27.43) * mm, "end": v(17.57, 31.06) * mm});
            skLineSegment(sketch, "E17.15.0.2", {"start": v(17.57, -13.07) * mm, "end": v(17.57, -9.44) * mm});
            skLineSegment(sketch, "E17.15.0.3", {"start": v(13.94, 9.43) * mm, "end": v(13.94, 13.06) * mm});
            skLineSegment(sketch, "E17.15.0.4", {"start": v(13.94, -13.07) * mm, "end": v(13.94, -9.44) * mm});
            skLineSegment(sketch, "E17.15.0.5", {"start": v(13.94, -31.07) * mm, "end": v(13.94, -27.44) * mm});
            skPoint(sketch, "E17.15.0.6", {"position": v(15.75, 33.75) * mm});
            skLineSegment(sketch, "E17.15.0.7", {"start": v(17.57, 9.43) * mm, "end": v(17.57, 13.06) * mm});
            skLineSegment(sketch, "E17.15.0.8", {"start": v(17.57, -31.07) * mm, "end": v(17.57, -27.44) * mm});
            skLineSegment(sketch, "E17.15.0.9", {"start": v(17.57, 31.93) * mm, "end": v(17.57, 27.43) * mm, "construction": true});
            skLineSegment(sketch, "E17.15.0.10", {"start": v(17.57, 31.06) * mm, "end": v(13.94, 31.06) * mm});
            skLineSegment(sketch, "E17.15.0.11", {"start": v(17.57, 4.93) * mm, "end": v(13.94, 4.93) * mm});
            skLineSegment(sketch, "E17.15.0.12", {"start": v(17.57, -13.07) * mm, "end": v(13.94, -13.07) * mm});
            skLineSegment(sketch, "E17.15.0.13", {"start": v(17.57, -31.07) * mm, "end": v(13.94, -31.07) * mm});
            skLineSegment(sketch, "E17.15.0.14", {"start": v(13.94, 31.93) * mm, "end": v(13.94, 35.56) * mm});
            skLineSegment(sketch, "E17.15.0.15", {"start": v(17.57, 31.93) * mm, "end": v(17.57, 35.56) * mm});
            skLineSegment(sketch, "E17.15.0.16", {"start": v(17.57, 31.93) * mm, "end": v(13.94, 31.93) * mm});
            skLineSegment(sketch, "E17.15.0.17", {"start": v(13.94, 18.43) * mm, "end": v(13.94, 22.06) * mm});
            skLineSegment(sketch, "E17.15.0.18", {"start": v(17.57, 13.06) * mm, "end": v(13.94, 13.06) * mm});
            skLineSegment(sketch, "E17.15.0.19", {"start": v(17.57, -4.94) * mm, "end": v(13.94, -4.94) * mm});
            skLineSegment(sketch, "E17.15.0.20", {"start": v(17.57, -22.94) * mm, "end": v(13.94, -22.94) * mm});
            skLineSegment(sketch, "E17.15.0.21", {"start": v(17.57, -26.57) * mm, "end": v(17.57, -22.94) * mm});
            skLineSegment(sketch, "E17.15.0.22", {"start": v(13.94, -8.57) * mm, "end": v(13.94, -4.94) * mm});
            skLineSegment(sketch, "E17.15.0.23", {"start": v(13.94, -26.57) * mm, "end": v(13.94, -22.94) * mm});
            skLineSegment(sketch, "E17.15.0.24", {"start": v(17.57, 17.56) * mm, "end": v(13.94, 17.56) * mm});
            skLineSegment(sketch, "E17.15.0.25", {"start": v(17.57, -0.44) * mm, "end": v(13.94, -0.44) * mm});
            skLineSegment(sketch, "E17.15.0.26", {"start": v(17.57, -9.44) * mm, "end": v(13.94, -9.44) * mm});
            skLineSegment(sketch, "E17.15.0.27", {"start": v(13.94, -22.07) * mm, "end": v(13.94, -18.44) * mm});
            skLineSegment(sketch, "E17.15.0.28", {"start": v(13.94, 13.93) * mm, "end": v(13.94, 17.56) * mm});
            skLineSegment(sketch, "E17.15.0.29", {"start": v(13.94, -4.07) * mm, "end": v(13.94, -0.44) * mm});
            skLineSegment(sketch, "E17.15.0.30", {"start": v(17.57, 13.93) * mm, "end": v(13.94, 13.93) * mm});
            skLineSegment(sketch, "E17.15.0.31", {"start": v(17.57, -4.07) * mm, "end": v(13.94, -4.07) * mm});
            skLineSegment(sketch, "E17.15.0.32", {"start": v(17.57, -17.57) * mm, "end": v(13.94, -17.57) * mm});
            skLineSegment(sketch, "E17.15.0.33", {"start": v(17.57, -27.44) * mm, "end": v(13.94, -27.44) * mm});
            skLineSegment(sketch, "E17.15.0.34", {"start": v(17.57, -35.57) * mm, "end": v(13.94, -35.57) * mm});
            skLineSegment(sketch, "E17.15.0.35", {"start": v(17.57, 0.43) * mm, "end": v(13.94, 0.43) * mm});
            skLineSegment(sketch, "E17.15.0.36", {"start": v(17.57, 13.93) * mm, "end": v(17.57, 17.56) * mm});
            skLineSegment(sketch, "E17.15.0.37", {"start": v(17.57, -22.07) * mm, "end": v(17.57, -18.44) * mm});
            skLineSegment(sketch, "E17.15.0.38", {"start": v(17.57, -17.57) * mm, "end": v(17.57, -13.94) * mm});
            skLineSegment(sketch, "E17.15.0.39", {"start": v(13.94, 4.93) * mm, "end": v(13.94, 8.56) * mm});
            skLineSegment(sketch, "E17.15.0.40", {"start": v(17.57, 26.56) * mm, "end": v(13.94, 26.56) * mm});
            skLineSegment(sketch, "E17.15.0.41", {"start": v(17.57, 9.43) * mm, "end": v(13.94, 9.43) * mm});
            skLineSegment(sketch, "E17.15.0.42", {"start": v(13.94, 22.93) * mm, "end": v(13.94, 26.56) * mm});
            skLineSegment(sketch, "E17.15.0.43", {"start": v(17.57, -13.94) * mm, "end": v(13.94, -13.94) * mm});
            skLineSegment(sketch, "E17.15.0.44", {"start": v(17.57, -31.94) * mm, "end": v(13.94, -31.94) * mm});
            skLineSegment(sketch, "E17.15.0.45", {"start": v(17.57, 22.06) * mm, "end": v(13.94, 22.06) * mm});
            skLineSegment(sketch, "E17.15.0.46", {"start": v(17.57, 4.06) * mm, "end": v(13.94, 4.06) * mm});
            skLineSegment(sketch, "E17.15.0.47", {"start": v(13.94, 0.43) * mm, "end": v(13.94, 4.06) * mm});
            skLineSegment(sketch, "E17.15.0.48", {"start": v(13.94, -35.57) * mm, "end": v(13.94, -31.94) * mm});
            skLineSegment(sketch, "E17.15.0.49", {"start": v(17.57, 0.43) * mm, "end": v(17.57, 4.06) * mm});
            skLineSegment(sketch, "E17.15.0.50", {"start": v(17.57, -26.57) * mm, "end": v(13.94, -26.57) * mm});
            skLineSegment(sketch, "E17.15.0.51", {"start": v(17.57, -35.57) * mm, "end": v(17.57, -31.94) * mm});
            skLineSegment(sketch, "E17.15.0.52", {"start": v(17.57, -4.07) * mm, "end": v(17.57, -0.44) * mm});
            skLineSegment(sketch, "E17.15.0.53", {"start": v(17.57, -22.07) * mm, "end": v(13.94, -22.07) * mm});
            skLineSegment(sketch, "E17.15.0.54", {"start": v(17.57, 18.43) * mm, "end": v(17.57, 22.06) * mm});
            skLineSegment(sketch, "E17.15.0.55", {"start": v(17.57, -18.44) * mm, "end": v(13.94, -18.44) * mm});
            skLineSegment(sketch, "E17.15.0.56", {"start": v(17.57, -8.57) * mm, "end": v(17.57, -4.94) * mm});
            skLineSegment(sketch, "E17.15.0.57", {"start": v(17.57, 18.43) * mm, "end": v(13.94, 18.43) * mm});
            skLineSegment(sketch, "E17.15.0.58", {"start": v(17.57, 35.56) * mm, "end": v(13.94, 35.56) * mm});
            skLineSegment(sketch, "E17.15.0.59", {"start": v(17.57, 4.93) * mm, "end": v(17.57, 8.56) * mm});
            skLineSegment(sketch, "E17.15.0.60", {"start": v(17.57, 27.43) * mm, "end": v(13.94, 27.43) * mm});
            skLineSegment(sketch, "E17.15.0.61", {"start": v(17.57, -8.57) * mm, "end": v(13.94, -8.57) * mm});
            skLineSegment(sketch, "E17.15.0.62", {"start": v(17.57, 8.56) * mm, "end": v(13.94, 8.56) * mm});
            skLineSegment(sketch, "E17.15.0.63", {"start": v(13.94, -17.57) * mm, "end": v(13.94, -13.94) * mm});
            skLineSegment(sketch, "E17.15.0.64", {"start": v(17.57, 22.93) * mm, "end": v(13.94, 22.93) * mm});
            skLineSegment(sketch, "E17.15.0.65", {"start": v(17.57, 22.93) * mm, "end": v(17.57, 26.56) * mm});
            skLineSegment(sketch, "E17.16.0.0", {"start": v(18.44, 27.43) * mm, "end": v(18.44, 31.06) * mm});
            skLineSegment(sketch, "E17.16.0.1", {"start": v(22.07, 27.43) * mm, "end": v(22.07, 31.06) * mm});
            skLineSegment(sketch, "E17.16.0.2", {"start": v(22.07, -13.07) * mm, "end": v(22.07, -9.44) * mm});
            skLineSegment(sketch, "E17.16.0.3", {"start": v(18.44, 9.43) * mm, "end": v(18.44, 13.06) * mm});
            skLineSegment(sketch, "E17.16.0.4", {"start": v(18.44, -13.07) * mm, "end": v(18.44, -9.44) * mm});
            skLineSegment(sketch, "E17.16.0.5", {"start": v(18.44, -31.07) * mm, "end": v(18.44, -27.44) * mm});
            skPoint(sketch, "E17.16.0.6", {"position": v(20.25, 33.75) * mm});
            skLineSegment(sketch, "E17.16.0.7", {"start": v(22.07, 9.43) * mm, "end": v(22.07, 13.06) * mm});
            skLineSegment(sketch, "E17.16.0.8", {"start": v(22.07, -31.07) * mm, "end": v(22.07, -27.44) * mm});
            skLineSegment(sketch, "E17.16.0.9", {"start": v(22.07, 31.93) * mm, "end": v(22.07, 27.43) * mm, "construction": true});
            skLineSegment(sketch, "E17.16.0.10", {"start": v(22.07, 31.06) * mm, "end": v(18.44, 31.06) * mm});
            skLineSegment(sketch, "E17.16.0.11", {"start": v(22.07, 4.93) * mm, "end": v(18.44, 4.93) * mm});
            skLineSegment(sketch, "E17.16.0.12", {"start": v(22.07, -13.07) * mm, "end": v(18.44, -13.07) * mm});
            skLineSegment(sketch, "E17.16.0.13", {"start": v(22.07, -31.07) * mm, "end": v(18.44, -31.07) * mm});
            skLineSegment(sketch, "E17.16.0.14", {"start": v(18.44, 31.93) * mm, "end": v(18.44, 35.56) * mm});
            skLineSegment(sketch, "E17.16.0.15", {"start": v(22.07, 31.93) * mm, "end": v(22.07, 35.56) * mm});
            skLineSegment(sketch, "E17.16.0.16", {"start": v(22.07, 31.93) * mm, "end": v(18.44, 31.93) * mm});
            skLineSegment(sketch, "E17.16.0.17", {"start": v(18.44, 18.43) * mm, "end": v(18.44, 22.06) * mm});
            skLineSegment(sketch, "E17.16.0.18", {"start": v(22.07, 13.06) * mm, "end": v(18.44, 13.06) * mm});
            skLineSegment(sketch, "E17.16.0.19", {"start": v(22.07, -4.94) * mm, "end": v(18.44, -4.94) * mm});
            skLineSegment(sketch, "E17.16.0.20", {"start": v(22.07, -22.94) * mm, "end": v(18.44, -22.94) * mm});
            skLineSegment(sketch, "E17.16.0.21", {"start": v(22.07, -26.57) * mm, "end": v(22.07, -22.94) * mm});
            skLineSegment(sketch, "E17.16.0.22", {"start": v(18.44, -8.57) * mm, "end": v(18.44, -4.94) * mm});
            skLineSegment(sketch, "E17.16.0.23", {"start": v(18.44, -26.57) * mm, "end": v(18.44, -22.94) * mm});
            skLineSegment(sketch, "E17.16.0.24", {"start": v(22.07, 17.56) * mm, "end": v(18.44, 17.56) * mm});
            skLineSegment(sketch, "E17.16.0.25", {"start": v(22.07, -0.44) * mm, "end": v(18.44, -0.44) * mm});
            skLineSegment(sketch, "E17.16.0.26", {"start": v(22.07, -9.44) * mm, "end": v(18.44, -9.44) * mm});
            skLineSegment(sketch, "E17.16.0.27", {"start": v(18.44, -22.07) * mm, "end": v(18.44, -18.44) * mm});
            skLineSegment(sketch, "E17.16.0.28", {"start": v(18.44, 13.93) * mm, "end": v(18.44, 17.56) * mm});
            skLineSegment(sketch, "E17.16.0.29", {"start": v(18.44, -4.07) * mm, "end": v(18.44, -0.44) * mm});
            skLineSegment(sketch, "E17.16.0.30", {"start": v(22.07, 13.93) * mm, "end": v(18.44, 13.93) * mm});
            skLineSegment(sketch, "E17.16.0.31", {"start": v(22.07, -4.07) * mm, "end": v(18.44, -4.07) * mm});
            skLineSegment(sketch, "E17.16.0.32", {"start": v(22.07, -17.57) * mm, "end": v(18.44, -17.57) * mm});
            skLineSegment(sketch, "E17.16.0.33", {"start": v(22.07, -27.44) * mm, "end": v(18.44, -27.44) * mm});
            skLineSegment(sketch, "E17.16.0.34", {"start": v(22.07, -35.57) * mm, "end": v(18.44, -35.57) * mm});
            skLineSegment(sketch, "E17.16.0.35", {"start": v(22.07, 0.43) * mm, "end": v(18.44, 0.43) * mm});
            skLineSegment(sketch, "E17.16.0.36", {"start": v(22.07, 13.93) * mm, "end": v(22.07, 17.56) * mm});
            skLineSegment(sketch, "E17.16.0.37", {"start": v(22.07, -22.07) * mm, "end": v(22.07, -18.44) * mm});
            skLineSegment(sketch, "E17.16.0.38", {"start": v(22.07, -17.57) * mm, "end": v(22.07, -13.94) * mm});
            skLineSegment(sketch, "E17.16.0.39", {"start": v(18.44, 4.93) * mm, "end": v(18.44, 8.56) * mm});
            skLineSegment(sketch, "E17.16.0.40", {"start": v(22.07, 26.56) * mm, "end": v(18.44, 26.56) * mm});
            skLineSegment(sketch, "E17.16.0.41", {"start": v(22.07, 9.43) * mm, "end": v(18.44, 9.43) * mm});
            skLineSegment(sketch, "E17.16.0.42", {"start": v(18.44, 22.93) * mm, "end": v(18.44, 26.56) * mm});
            skLineSegment(sketch, "E17.16.0.43", {"start": v(22.07, -13.94) * mm, "end": v(18.44, -13.94) * mm});
            skLineSegment(sketch, "E17.16.0.44", {"start": v(22.07, -31.94) * mm, "end": v(18.44, -31.94) * mm});
            skLineSegment(sketch, "E17.16.0.45", {"start": v(22.07, 22.06) * mm, "end": v(18.44, 22.06) * mm});
            skLineSegment(sketch, "E17.16.0.46", {"start": v(22.07, 4.06) * mm, "end": v(18.44, 4.06) * mm});
            skLineSegment(sketch, "E17.16.0.47", {"start": v(18.44, 0.43) * mm, "end": v(18.44, 4.06) * mm});
            skLineSegment(sketch, "E17.16.0.48", {"start": v(18.44, -35.57) * mm, "end": v(18.44, -31.94) * mm});
            skLineSegment(sketch, "E17.16.0.49", {"start": v(22.07, 0.43) * mm, "end": v(22.07, 4.06) * mm});
            skLineSegment(sketch, "E17.16.0.50", {"start": v(22.07, -26.57) * mm, "end": v(18.44, -26.57) * mm});
            skLineSegment(sketch, "E17.16.0.51", {"start": v(22.07, -35.57) * mm, "end": v(22.07, -31.94) * mm});
            skLineSegment(sketch, "E17.16.0.52", {"start": v(22.07, -4.07) * mm, "end": v(22.07, -0.44) * mm});
            skLineSegment(sketch, "E17.16.0.53", {"start": v(22.07, -22.07) * mm, "end": v(18.44, -22.07) * mm});
            skLineSegment(sketch, "E17.16.0.54", {"start": v(22.07, 18.43) * mm, "end": v(22.07, 22.06) * mm});
            skLineSegment(sketch, "E17.16.0.55", {"start": v(22.07, -18.44) * mm, "end": v(18.44, -18.44) * mm});
            skLineSegment(sketch, "E17.16.0.56", {"start": v(22.07, -8.57) * mm, "end": v(22.07, -4.94) * mm});
            skLineSegment(sketch, "E17.16.0.57", {"start": v(22.07, 18.43) * mm, "end": v(18.44, 18.43) * mm});
            skLineSegment(sketch, "E17.16.0.58", {"start": v(22.07, 35.56) * mm, "end": v(18.44, 35.56) * mm});
            skLineSegment(sketch, "E17.16.0.59", {"start": v(22.07, 4.93) * mm, "end": v(22.07, 8.56) * mm});
            skLineSegment(sketch, "E17.16.0.60", {"start": v(22.07, 27.43) * mm, "end": v(18.44, 27.43) * mm});
            skLineSegment(sketch, "E17.16.0.61", {"start": v(22.07, -8.57) * mm, "end": v(18.44, -8.57) * mm});
            skLineSegment(sketch, "E17.16.0.62", {"start": v(22.07, 8.56) * mm, "end": v(18.44, 8.56) * mm});
            skLineSegment(sketch, "E17.16.0.63", {"start": v(18.44, -17.57) * mm, "end": v(18.44, -13.94) * mm});
            skLineSegment(sketch, "E17.16.0.64", {"start": v(22.07, 22.93) * mm, "end": v(18.44, 22.93) * mm});
            skLineSegment(sketch, "E17.16.0.65", {"start": v(22.07, 22.93) * mm, "end": v(22.07, 26.56) * mm});
            skLineSegment(sketch, "E17.17.0.0", {"start": v(22.94, 27.43) * mm, "end": v(22.94, 31.06) * mm});
            skLineSegment(sketch, "E17.17.0.1", {"start": v(26.57, 27.43) * mm, "end": v(26.57, 31.06) * mm});
            skLineSegment(sketch, "E17.17.0.2", {"start": v(26.57, -13.07) * mm, "end": v(26.57, -9.44) * mm});
            skLineSegment(sketch, "E17.17.0.3", {"start": v(22.94, 9.43) * mm, "end": v(22.94, 13.06) * mm});
            skLineSegment(sketch, "E17.17.0.4", {"start": v(22.94, -13.07) * mm, "end": v(22.94, -9.44) * mm});
            skLineSegment(sketch, "E17.17.0.5", {"start": v(22.94, -31.07) * mm, "end": v(22.94, -27.44) * mm});
            skPoint(sketch, "E17.17.0.6", {"position": v(24.75, 33.75) * mm});
            skLineSegment(sketch, "E17.17.0.7", {"start": v(26.57, 9.43) * mm, "end": v(26.57, 13.06) * mm});
            skLineSegment(sketch, "E17.17.0.8", {"start": v(26.57, -31.07) * mm, "end": v(26.57, -27.44) * mm});
            skLineSegment(sketch, "E17.17.0.9", {"start": v(26.57, 31.93) * mm, "end": v(26.57, 27.43) * mm, "construction": true});
            skLineSegment(sketch, "E17.17.0.10", {"start": v(26.57, 31.06) * mm, "end": v(22.94, 31.06) * mm});
            skLineSegment(sketch, "E17.17.0.11", {"start": v(26.57, 4.93) * mm, "end": v(22.94, 4.93) * mm});
            skLineSegment(sketch, "E17.17.0.12", {"start": v(26.57, -13.07) * mm, "end": v(22.94, -13.07) * mm});
            skLineSegment(sketch, "E17.17.0.13", {"start": v(26.57, -31.07) * mm, "end": v(22.94, -31.07) * mm});
            skLineSegment(sketch, "E17.17.0.14", {"start": v(22.94, 31.93) * mm, "end": v(22.94, 35.56) * mm});
            skLineSegment(sketch, "E17.17.0.15", {"start": v(26.57, 31.93) * mm, "end": v(26.57, 35.56) * mm});
            skLineSegment(sketch, "E17.17.0.16", {"start": v(26.57, 31.93) * mm, "end": v(22.94, 31.93) * mm});
            skLineSegment(sketch, "E17.17.0.17", {"start": v(22.94, 18.43) * mm, "end": v(22.94, 22.06) * mm});
            skLineSegment(sketch, "E17.17.0.18", {"start": v(26.57, 13.06) * mm, "end": v(22.94, 13.06) * mm});
            skLineSegment(sketch, "E17.17.0.19", {"start": v(26.57, -4.94) * mm, "end": v(22.94, -4.94) * mm});
            skLineSegment(sketch, "E17.17.0.20", {"start": v(26.57, -22.94) * mm, "end": v(22.94, -22.94) * mm});
            skLineSegment(sketch, "E17.17.0.21", {"start": v(26.57, -26.57) * mm, "end": v(26.57, -22.94) * mm});
            skLineSegment(sketch, "E17.17.0.22", {"start": v(22.94, -8.57) * mm, "end": v(22.94, -4.94) * mm});
            skLineSegment(sketch, "E17.17.0.23", {"start": v(22.94, -26.57) * mm, "end": v(22.94, -22.94) * mm});
            skLineSegment(sketch, "E17.17.0.24", {"start": v(26.57, 17.56) * mm, "end": v(22.94, 17.56) * mm});
            skLineSegment(sketch, "E17.17.0.25", {"start": v(26.57, -0.44) * mm, "end": v(22.94, -0.44) * mm});
            skLineSegment(sketch, "E17.17.0.26", {"start": v(26.57, -9.44) * mm, "end": v(22.94, -9.44) * mm});
            skLineSegment(sketch, "E17.17.0.27", {"start": v(22.94, -22.07) * mm, "end": v(22.94, -18.44) * mm});
            skLineSegment(sketch, "E17.17.0.28", {"start": v(22.94, 13.93) * mm, "end": v(22.94, 17.56) * mm});
            skLineSegment(sketch, "E17.17.0.29", {"start": v(22.94, -4.07) * mm, "end": v(22.94, -0.44) * mm});
            skLineSegment(sketch, "E17.17.0.30", {"start": v(26.57, 13.93) * mm, "end": v(22.94, 13.93) * mm});
            skLineSegment(sketch, "E17.17.0.31", {"start": v(26.57, -4.07) * mm, "end": v(22.94, -4.07) * mm});
            skLineSegment(sketch, "E17.17.0.32", {"start": v(26.57, -17.57) * mm, "end": v(22.94, -17.57) * mm});
            skLineSegment(sketch, "E17.17.0.33", {"start": v(26.57, -27.44) * mm, "end": v(22.94, -27.44) * mm});
            skLineSegment(sketch, "E17.17.0.34", {"start": v(26.57, -35.57) * mm, "end": v(22.94, -35.57) * mm});
            skLineSegment(sketch, "E17.17.0.35", {"start": v(26.57, 0.43) * mm, "end": v(22.94, 0.43) * mm});
            skLineSegment(sketch, "E17.17.0.36", {"start": v(26.57, 13.93) * mm, "end": v(26.57, 17.56) * mm});
            skLineSegment(sketch, "E17.17.0.37", {"start": v(26.57, -22.07) * mm, "end": v(26.57, -18.44) * mm});
            skLineSegment(sketch, "E17.17.0.38", {"start": v(26.57, -17.57) * mm, "end": v(26.57, -13.94) * mm});
            skLineSegment(sketch, "E17.17.0.39", {"start": v(22.94, 4.93) * mm, "end": v(22.94, 8.56) * mm});
            skLineSegment(sketch, "E17.17.0.40", {"start": v(26.57, 26.56) * mm, "end": v(22.94, 26.56) * mm});
            skLineSegment(sketch, "E17.17.0.41", {"start": v(26.57, 9.43) * mm, "end": v(22.94, 9.43) * mm});
            skLineSegment(sketch, "E17.17.0.42", {"start": v(22.94, 22.93) * mm, "end": v(22.94, 26.56) * mm});
            skLineSegment(sketch, "E17.17.0.43", {"start": v(26.57, -13.94) * mm, "end": v(22.94, -13.94) * mm});
            skLineSegment(sketch, "E17.17.0.44", {"start": v(26.57, -31.94) * mm, "end": v(22.94, -31.94) * mm});
            skLineSegment(sketch, "E17.17.0.45", {"start": v(26.57, 22.06) * mm, "end": v(22.94, 22.06) * mm});
            skLineSegment(sketch, "E17.17.0.46", {"start": v(26.57, 4.06) * mm, "end": v(22.94, 4.06) * mm});
            skLineSegment(sketch, "E17.17.0.47", {"start": v(22.94, 0.43) * mm, "end": v(22.94, 4.06) * mm});
            skLineSegment(sketch, "E17.17.0.48", {"start": v(22.94, -35.57) * mm, "end": v(22.94, -31.94) * mm});
            skLineSegment(sketch, "E17.17.0.49", {"start": v(26.57, 0.43) * mm, "end": v(26.57, 4.06) * mm});
            skLineSegment(sketch, "E17.17.0.50", {"start": v(26.57, -26.57) * mm, "end": v(22.94, -26.57) * mm});
            skLineSegment(sketch, "E17.17.0.51", {"start": v(26.57, -35.57) * mm, "end": v(26.57, -31.94) * mm});
            skLineSegment(sketch, "E17.17.0.52", {"start": v(26.57, -4.07) * mm, "end": v(26.57, -0.44) * mm});
            skLineSegment(sketch, "E17.17.0.53", {"start": v(26.57, -22.07) * mm, "end": v(22.94, -22.07) * mm});
            skLineSegment(sketch, "E17.17.0.54", {"start": v(26.57, 18.43) * mm, "end": v(26.57, 22.06) * mm});
            skLineSegment(sketch, "E17.17.0.55", {"start": v(26.57, -18.44) * mm, "end": v(22.94, -18.44) * mm});
            skLineSegment(sketch, "E17.17.0.56", {"start": v(26.57, -8.57) * mm, "end": v(26.57, -4.94) * mm});
            skLineSegment(sketch, "E17.17.0.57", {"start": v(26.57, 18.43) * mm, "end": v(22.94, 18.43) * mm});
            skLineSegment(sketch, "E17.17.0.58", {"start": v(26.57, 35.56) * mm, "end": v(22.94, 35.56) * mm});
            skLineSegment(sketch, "E17.17.0.59", {"start": v(26.57, 4.93) * mm, "end": v(26.57, 8.56) * mm});
            skLineSegment(sketch, "E17.17.0.60", {"start": v(26.57, 27.43) * mm, "end": v(22.94, 27.43) * mm});
            skLineSegment(sketch, "E17.17.0.61", {"start": v(26.57, -8.57) * mm, "end": v(22.94, -8.57) * mm});
            skLineSegment(sketch, "E17.17.0.62", {"start": v(26.57, 8.56) * mm, "end": v(22.94, 8.56) * mm});
            skLineSegment(sketch, "E17.17.0.63", {"start": v(22.94, -17.57) * mm, "end": v(22.94, -13.94) * mm});
            skLineSegment(sketch, "E17.17.0.64", {"start": v(26.57, 22.93) * mm, "end": v(22.94, 22.93) * mm});
            skLineSegment(sketch, "E17.17.0.65", {"start": v(26.57, 22.93) * mm, "end": v(26.57, 26.56) * mm});
            skLineSegment(sketch, "E17.18.0.0", {"start": v(27.44, 27.43) * mm, "end": v(27.44, 31.06) * mm});
            skLineSegment(sketch, "E17.18.0.1", {"start": v(31.07, 27.43) * mm, "end": v(31.07, 31.06) * mm});
            skLineSegment(sketch, "E17.18.0.2", {"start": v(31.07, -13.07) * mm, "end": v(31.07, -9.44) * mm});
            skLineSegment(sketch, "E17.18.0.3", {"start": v(27.44, 9.43) * mm, "end": v(27.44, 13.06) * mm});
            skLineSegment(sketch, "E17.18.0.4", {"start": v(27.44, -13.07) * mm, "end": v(27.44, -9.44) * mm});
            skLineSegment(sketch, "E17.18.0.5", {"start": v(27.44, -31.07) * mm, "end": v(27.44, -27.44) * mm});
            skPoint(sketch, "E17.18.0.6", {"position": v(29.25, 33.75) * mm});
            skLineSegment(sketch, "E17.18.0.7", {"start": v(31.07, 9.43) * mm, "end": v(31.07, 13.06) * mm});
            skLineSegment(sketch, "E17.18.0.8", {"start": v(31.07, -31.07) * mm, "end": v(31.07, -27.44) * mm});
            skLineSegment(sketch, "E17.18.0.9", {"start": v(31.07, 31.93) * mm, "end": v(31.07, 27.43) * mm, "construction": true});
            skLineSegment(sketch, "E17.18.0.10", {"start": v(31.07, 31.06) * mm, "end": v(27.44, 31.06) * mm});
            skLineSegment(sketch, "E17.18.0.11", {"start": v(31.07, 4.93) * mm, "end": v(27.44, 4.93) * mm});
            skLineSegment(sketch, "E17.18.0.12", {"start": v(31.07, -13.07) * mm, "end": v(27.44, -13.07) * mm});
            skLineSegment(sketch, "E17.18.0.13", {"start": v(31.07, -31.07) * mm, "end": v(27.44, -31.07) * mm});
            skLineSegment(sketch, "E17.18.0.14", {"start": v(27.44, 31.93) * mm, "end": v(27.44, 35.56) * mm});
            skLineSegment(sketch, "E17.18.0.15", {"start": v(31.07, 31.93) * mm, "end": v(31.07, 35.56) * mm});
            skLineSegment(sketch, "E17.18.0.16", {"start": v(31.07, 31.93) * mm, "end": v(27.44, 31.93) * mm});
            skLineSegment(sketch, "E17.18.0.17", {"start": v(27.44, 18.43) * mm, "end": v(27.44, 22.06) * mm});
            skLineSegment(sketch, "E17.18.0.18", {"start": v(31.07, 13.06) * mm, "end": v(27.44, 13.06) * mm});
            skLineSegment(sketch, "E17.18.0.19", {"start": v(31.07, -4.94) * mm, "end": v(27.44, -4.94) * mm});
            skLineSegment(sketch, "E17.18.0.20", {"start": v(31.07, -22.94) * mm, "end": v(27.44, -22.94) * mm});
            skLineSegment(sketch, "E17.18.0.21", {"start": v(31.07, -26.57) * mm, "end": v(31.07, -22.94) * mm});
            skLineSegment(sketch, "E17.18.0.22", {"start": v(27.44, -8.57) * mm, "end": v(27.44, -4.94) * mm});
            skLineSegment(sketch, "E17.18.0.23", {"start": v(27.44, -26.57) * mm, "end": v(27.44, -22.94) * mm});
            skLineSegment(sketch, "E17.18.0.24", {"start": v(31.07, 17.56) * mm, "end": v(27.44, 17.56) * mm});
            skLineSegment(sketch, "E17.18.0.25", {"start": v(31.07, -0.44) * mm, "end": v(27.44, -0.44) * mm});
            skLineSegment(sketch, "E17.18.0.26", {"start": v(31.07, -9.44) * mm, "end": v(27.44, -9.44) * mm});
            skLineSegment(sketch, "E17.18.0.27", {"start": v(27.44, -22.07) * mm, "end": v(27.44, -18.44) * mm});
            skLineSegment(sketch, "E17.18.0.28", {"start": v(27.44, 13.93) * mm, "end": v(27.44, 17.56) * mm});
            skLineSegment(sketch, "E17.18.0.29", {"start": v(27.44, -4.07) * mm, "end": v(27.44, -0.44) * mm});
            skLineSegment(sketch, "E17.18.0.30", {"start": v(31.07, 13.93) * mm, "end": v(27.44, 13.93) * mm});
            skLineSegment(sketch, "E17.18.0.31", {"start": v(31.07, -4.07) * mm, "end": v(27.44, -4.07) * mm});
            skLineSegment(sketch, "E17.18.0.32", {"start": v(31.07, -17.57) * mm, "end": v(27.44, -17.57) * mm});
            skLineSegment(sketch, "E17.18.0.33", {"start": v(31.07, -27.44) * mm, "end": v(27.44, -27.44) * mm});
            skLineSegment(sketch, "E17.18.0.34", {"start": v(31.07, -35.57) * mm, "end": v(27.44, -35.57) * mm});
            skLineSegment(sketch, "E17.18.0.35", {"start": v(31.07, 0.43) * mm, "end": v(27.44, 0.43) * mm});
            skLineSegment(sketch, "E17.18.0.36", {"start": v(31.07, 13.93) * mm, "end": v(31.07, 17.56) * mm});
            skLineSegment(sketch, "E17.18.0.37", {"start": v(31.07, -22.07) * mm, "end": v(31.07, -18.44) * mm});
            skLineSegment(sketch, "E17.18.0.38", {"start": v(31.07, -17.57) * mm, "end": v(31.07, -13.94) * mm});
            skLineSegment(sketch, "E17.18.0.39", {"start": v(27.44, 4.93) * mm, "end": v(27.44, 8.56) * mm});
            skLineSegment(sketch, "E17.18.0.40", {"start": v(31.07, 26.56) * mm, "end": v(27.44, 26.56) * mm});
            skLineSegment(sketch, "E17.18.0.41", {"start": v(31.07, 9.43) * mm, "end": v(27.44, 9.43) * mm});
            skLineSegment(sketch, "E17.18.0.42", {"start": v(27.44, 22.93) * mm, "end": v(27.44, 26.56) * mm});
            skLineSegment(sketch, "E17.18.0.43", {"start": v(31.07, -13.94) * mm, "end": v(27.44, -13.94) * mm});
            skLineSegment(sketch, "E17.18.0.44", {"start": v(31.07, -31.94) * mm, "end": v(27.44, -31.94) * mm});
            skLineSegment(sketch, "E17.18.0.45", {"start": v(31.07, 22.06) * mm, "end": v(27.44, 22.06) * mm});
            skLineSegment(sketch, "E17.18.0.46", {"start": v(31.07, 4.06) * mm, "end": v(27.44, 4.06) * mm});
            skLineSegment(sketch, "E17.18.0.47", {"start": v(27.44, 0.43) * mm, "end": v(27.44, 4.06) * mm});
            skLineSegment(sketch, "E17.18.0.48", {"start": v(27.44, -35.57) * mm, "end": v(27.44, -31.94) * mm});
            skLineSegment(sketch, "E17.18.0.49", {"start": v(31.07, 0.43) * mm, "end": v(31.07, 4.06) * mm});
            skLineSegment(sketch, "E17.18.0.50", {"start": v(31.07, -26.57) * mm, "end": v(27.44, -26.57) * mm});
            skLineSegment(sketch, "E17.18.0.51", {"start": v(31.07, -35.57) * mm, "end": v(31.07, -31.94) * mm});
            skLineSegment(sketch, "E17.18.0.52", {"start": v(31.07, -4.07) * mm, "end": v(31.07, -0.44) * mm});
            skLineSegment(sketch, "E17.18.0.53", {"start": v(31.07, -22.07) * mm, "end": v(27.44, -22.07) * mm});
            skLineSegment(sketch, "E17.18.0.54", {"start": v(31.07, 18.43) * mm, "end": v(31.07, 22.06) * mm});
            skLineSegment(sketch, "E17.18.0.55", {"start": v(31.07, -18.44) * mm, "end": v(27.44, -18.44) * mm});
            skLineSegment(sketch, "E17.18.0.56", {"start": v(31.07, -8.57) * mm, "end": v(31.07, -4.94) * mm});
            skLineSegment(sketch, "E17.18.0.57", {"start": v(31.07, 18.43) * mm, "end": v(27.44, 18.43) * mm});
            skLineSegment(sketch, "E17.18.0.58", {"start": v(31.07, 35.56) * mm, "end": v(27.44, 35.56) * mm});
            skLineSegment(sketch, "E17.18.0.59", {"start": v(31.07, 4.93) * mm, "end": v(31.07, 8.56) * mm});
            skLineSegment(sketch, "E17.18.0.60", {"start": v(31.07, 27.43) * mm, "end": v(27.44, 27.43) * mm});
            skLineSegment(sketch, "E17.18.0.61", {"start": v(31.07, -8.57) * mm, "end": v(27.44, -8.57) * mm});
            skLineSegment(sketch, "E17.18.0.62", {"start": v(31.07, 8.56) * mm, "end": v(27.44, 8.56) * mm});
            skLineSegment(sketch, "E17.18.0.63", {"start": v(27.44, -17.57) * mm, "end": v(27.44, -13.94) * mm});
            skLineSegment(sketch, "E17.18.0.64", {"start": v(31.07, 22.93) * mm, "end": v(27.44, 22.93) * mm});
            skLineSegment(sketch, "E17.18.0.65", {"start": v(31.07, 22.93) * mm, "end": v(31.07, 26.56) * mm});
            skLineSegment(sketch, "E17.19.0.0", {"start": v(31.94, 27.43) * mm, "end": v(31.94, 31.06) * mm});
            skLineSegment(sketch, "E17.19.0.1", {"start": v(35.57, 27.43) * mm, "end": v(35.57, 31.06) * mm});
            skLineSegment(sketch, "E17.19.0.2", {"start": v(35.57, -13.07) * mm, "end": v(35.57, -9.44) * mm});
            skLineSegment(sketch, "E17.19.0.3", {"start": v(31.94, 9.43) * mm, "end": v(31.94, 13.06) * mm});
            skLineSegment(sketch, "E17.19.0.4", {"start": v(31.94, -13.07) * mm, "end": v(31.94, -9.44) * mm});
            skLineSegment(sketch, "E17.19.0.5", {"start": v(31.94, -31.07) * mm, "end": v(31.94, -27.44) * mm});
            skPoint(sketch, "E17.19.0.6", {"position": v(33.75, 33.75) * mm});
            skLineSegment(sketch, "E17.19.0.7", {"start": v(35.57, 9.43) * mm, "end": v(35.57, 13.06) * mm});
            skLineSegment(sketch, "E17.19.0.8", {"start": v(35.57, -31.07) * mm, "end": v(35.57, -27.44) * mm});
            skLineSegment(sketch, "E17.19.0.9", {"start": v(35.57, 31.93) * mm, "end": v(35.57, 27.43) * mm, "construction": true});
            skLineSegment(sketch, "E17.19.0.10", {"start": v(35.57, 31.06) * mm, "end": v(31.94, 31.06) * mm});
            skLineSegment(sketch, "E17.19.0.11", {"start": v(35.57, 4.93) * mm, "end": v(31.94, 4.93) * mm});
            skLineSegment(sketch, "E17.19.0.12", {"start": v(35.57, -13.07) * mm, "end": v(31.94, -13.07) * mm});
            skLineSegment(sketch, "E17.19.0.13", {"start": v(35.57, -31.07) * mm, "end": v(31.94, -31.07) * mm});
            skLineSegment(sketch, "E17.19.0.14", {"start": v(31.94, 31.93) * mm, "end": v(31.94, 35.56) * mm});
            skLineSegment(sketch, "E17.19.0.15", {"start": v(35.57, 31.93) * mm, "end": v(35.57, 35.56) * mm});
            skLineSegment(sketch, "E17.19.0.16", {"start": v(35.57, 31.93) * mm, "end": v(31.94, 31.93) * mm});
            skLineSegment(sketch, "E17.19.0.17", {"start": v(31.94, 18.43) * mm, "end": v(31.94, 22.06) * mm});
            skLineSegment(sketch, "E17.19.0.18", {"start": v(35.57, 13.06) * mm, "end": v(31.94, 13.06) * mm});
            skLineSegment(sketch, "E17.19.0.19", {"start": v(35.57, -4.94) * mm, "end": v(31.94, -4.94) * mm});
            skLineSegment(sketch, "E17.19.0.20", {"start": v(35.57, -22.94) * mm, "end": v(31.94, -22.94) * mm});
            skLineSegment(sketch, "E17.19.0.21", {"start": v(35.57, -26.57) * mm, "end": v(35.57, -22.94) * mm});
            skLineSegment(sketch, "E17.19.0.22", {"start": v(31.94, -8.57) * mm, "end": v(31.94, -4.94) * mm});
            skLineSegment(sketch, "E17.19.0.23", {"start": v(31.94, -26.57) * mm, "end": v(31.94, -22.94) * mm});
            skLineSegment(sketch, "E17.19.0.24", {"start": v(35.57, 17.56) * mm, "end": v(31.94, 17.56) * mm});
            skLineSegment(sketch, "E17.19.0.25", {"start": v(35.57, -0.44) * mm, "end": v(31.94, -0.44) * mm});
            skLineSegment(sketch, "E17.19.0.26", {"start": v(35.57, -9.44) * mm, "end": v(31.94, -9.44) * mm});
            skLineSegment(sketch, "E17.19.0.27", {"start": v(31.94, -22.07) * mm, "end": v(31.94, -18.44) * mm});
            skLineSegment(sketch, "E17.19.0.28", {"start": v(31.94, 13.93) * mm, "end": v(31.94, 17.56) * mm});
            skLineSegment(sketch, "E17.19.0.29", {"start": v(31.94, -4.07) * mm, "end": v(31.94, -0.44) * mm});
            skLineSegment(sketch, "E17.19.0.30", {"start": v(35.57, 13.93) * mm, "end": v(31.94, 13.93) * mm});
            skLineSegment(sketch, "E17.19.0.31", {"start": v(35.57, -4.07) * mm, "end": v(31.94, -4.07) * mm});
            skLineSegment(sketch, "E17.19.0.32", {"start": v(35.57, -17.57) * mm, "end": v(31.94, -17.57) * mm});
            skLineSegment(sketch, "E17.19.0.33", {"start": v(35.57, -27.44) * mm, "end": v(31.94, -27.44) * mm});
            skLineSegment(sketch, "E17.19.0.34", {"start": v(35.57, -35.57) * mm, "end": v(31.94, -35.57) * mm});
            skLineSegment(sketch, "E17.19.0.35", {"start": v(35.57, 0.43) * mm, "end": v(31.94, 0.43) * mm});
            skLineSegment(sketch, "E17.19.0.36", {"start": v(35.57, 13.93) * mm, "end": v(35.57, 17.56) * mm});
            skLineSegment(sketch, "E17.19.0.37", {"start": v(35.57, -22.07) * mm, "end": v(35.57, -18.44) * mm});
            skLineSegment(sketch, "E17.19.0.38", {"start": v(35.57, -17.57) * mm, "end": v(35.57, -13.94) * mm});
            skLineSegment(sketch, "E17.19.0.39", {"start": v(31.94, 4.93) * mm, "end": v(31.94, 8.56) * mm});
            skLineSegment(sketch, "E17.19.0.40", {"start": v(35.57, 26.56) * mm, "end": v(31.94, 26.56) * mm});
            skLineSegment(sketch, "E17.19.0.41", {"start": v(35.57, 9.43) * mm, "end": v(31.94, 9.43) * mm});
            skLineSegment(sketch, "E17.19.0.42", {"start": v(31.94, 22.93) * mm, "end": v(31.94, 26.56) * mm});
            skLineSegment(sketch, "E17.19.0.43", {"start": v(35.57, -13.94) * mm, "end": v(31.94, -13.94) * mm});
            skLineSegment(sketch, "E17.19.0.44", {"start": v(35.57, -31.94) * mm, "end": v(31.94, -31.94) * mm});
            skLineSegment(sketch, "E17.19.0.45", {"start": v(35.57, 22.06) * mm, "end": v(31.94, 22.06) * mm});
            skLineSegment(sketch, "E17.19.0.46", {"start": v(35.57, 4.06) * mm, "end": v(31.94, 4.06) * mm});
            skLineSegment(sketch, "E17.19.0.47", {"start": v(31.94, 0.43) * mm, "end": v(31.94, 4.06) * mm});
            skLineSegment(sketch, "E17.19.0.48", {"start": v(31.94, -35.57) * mm, "end": v(31.94, -31.94) * mm});
            skLineSegment(sketch, "E17.19.0.49", {"start": v(35.57, 0.43) * mm, "end": v(35.57, 4.06) * mm});
            skLineSegment(sketch, "E17.19.0.50", {"start": v(35.57, -26.57) * mm, "end": v(31.94, -26.57) * mm});
            skLineSegment(sketch, "E17.19.0.51", {"start": v(35.57, -35.57) * mm, "end": v(35.57, -31.94) * mm});
            skLineSegment(sketch, "E17.19.0.52", {"start": v(35.57, -4.07) * mm, "end": v(35.57, -0.44) * mm});
            skLineSegment(sketch, "E17.19.0.53", {"start": v(35.57, -22.07) * mm, "end": v(31.94, -22.07) * mm});
            skLineSegment(sketch, "E17.19.0.54", {"start": v(35.57, 18.43) * mm, "end": v(35.57, 22.06) * mm});
            skLineSegment(sketch, "E17.19.0.55", {"start": v(35.57, -18.44) * mm, "end": v(31.94, -18.44) * mm});
            skLineSegment(sketch, "E17.19.0.56", {"start": v(35.57, -8.57) * mm, "end": v(35.57, -4.94) * mm});
            skLineSegment(sketch, "E17.19.0.57", {"start": v(35.57, 18.43) * mm, "end": v(31.94, 18.43) * mm});
            skLineSegment(sketch, "E17.19.0.58", {"start": v(35.57, 35.56) * mm, "end": v(31.94, 35.56) * mm});
            skLineSegment(sketch, "E17.19.0.59", {"start": v(35.57, 4.93) * mm, "end": v(35.57, 8.56) * mm});
            skLineSegment(sketch, "E17.19.0.60", {"start": v(35.57, 27.43) * mm, "end": v(31.94, 27.43) * mm});
            skLineSegment(sketch, "E17.19.0.61", {"start": v(35.57, -8.57) * mm, "end": v(31.94, -8.57) * mm});
            skLineSegment(sketch, "E17.19.0.62", {"start": v(35.57, 8.56) * mm, "end": v(31.94, 8.56) * mm});
            skLineSegment(sketch, "E17.19.0.63", {"start": v(31.94, -17.57) * mm, "end": v(31.94, -13.94) * mm});
            skLineSegment(sketch, "E17.19.0.64", {"start": v(35.57, 22.93) * mm, "end": v(31.94, 22.93) * mm});
            skLineSegment(sketch, "E17.19.0.65", {"start": v(35.57, 22.93) * mm, "end": v(35.57, 26.56) * mm});
            skLineSegment(sketch, "E17.20.0.0", {"start": v(36.44, 27.43) * mm, "end": v(36.44, 31.06) * mm});
            skLineSegment(sketch, "E17.20.0.1", {"start": v(40.07, 27.43) * mm, "end": v(40.07, 31.06) * mm});
            skLineSegment(sketch, "E17.20.0.2", {"start": v(40.07, -13.07) * mm, "end": v(40.07, -9.44) * mm});
            skLineSegment(sketch, "E17.20.0.3", {"start": v(36.44, 9.43) * mm, "end": v(36.44, 13.06) * mm});
            skLineSegment(sketch, "E17.20.0.4", {"start": v(36.44, -13.07) * mm, "end": v(36.44, -9.44) * mm});
            skLineSegment(sketch, "E17.20.0.5", {"start": v(36.44, -31.07) * mm, "end": v(36.44, -27.44) * mm});
            skPoint(sketch, "E17.20.0.6", {"position": v(38.25, 33.75) * mm});
            skLineSegment(sketch, "E17.20.0.7", {"start": v(40.07, 9.43) * mm, "end": v(40.07, 13.06) * mm});
            skLineSegment(sketch, "E17.20.0.8", {"start": v(40.07, -31.07) * mm, "end": v(40.07, -27.44) * mm});
            skLineSegment(sketch, "E17.20.0.9", {"start": v(40.07, 31.93) * mm, "end": v(40.07, 27.43) * mm, "construction": true});
            skLineSegment(sketch, "E17.20.0.10", {"start": v(40.07, 31.06) * mm, "end": v(36.44, 31.06) * mm});
            skLineSegment(sketch, "E17.20.0.11", {"start": v(40.07, 4.93) * mm, "end": v(36.44, 4.93) * mm});
            skLineSegment(sketch, "E17.20.0.12", {"start": v(40.07, -13.07) * mm, "end": v(36.44, -13.07) * mm});
            skLineSegment(sketch, "E17.20.0.13", {"start": v(40.07, -31.07) * mm, "end": v(36.44, -31.07) * mm});
            skLineSegment(sketch, "E17.20.0.14", {"start": v(36.44, 31.93) * mm, "end": v(36.44, 35.56) * mm});
            skLineSegment(sketch, "E17.20.0.15", {"start": v(40.07, 31.93) * mm, "end": v(40.07, 35.56) * mm});
            skLineSegment(sketch, "E17.20.0.16", {"start": v(40.07, 31.93) * mm, "end": v(36.44, 31.93) * mm});
            skLineSegment(sketch, "E17.20.0.17", {"start": v(36.44, 18.43) * mm, "end": v(36.44, 22.06) * mm});
            skLineSegment(sketch, "E17.20.0.18", {"start": v(40.07, 13.06) * mm, "end": v(36.44, 13.06) * mm});
            skLineSegment(sketch, "E17.20.0.19", {"start": v(40.07, -4.94) * mm, "end": v(36.44, -4.94) * mm});
            skLineSegment(sketch, "E17.20.0.20", {"start": v(40.07, -22.94) * mm, "end": v(36.44, -22.94) * mm});
            skLineSegment(sketch, "E17.20.0.21", {"start": v(40.07, -26.57) * mm, "end": v(40.07, -22.94) * mm});
            skLineSegment(sketch, "E17.20.0.22", {"start": v(36.44, -8.57) * mm, "end": v(36.44, -4.94) * mm});
            skLineSegment(sketch, "E17.20.0.23", {"start": v(36.44, -26.57) * mm, "end": v(36.44, -22.94) * mm});
            skLineSegment(sketch, "E17.20.0.24", {"start": v(40.07, 17.56) * mm, "end": v(36.44, 17.56) * mm});
            skLineSegment(sketch, "E17.20.0.25", {"start": v(40.07, -0.44) * mm, "end": v(36.44, -0.44) * mm});
            skLineSegment(sketch, "E17.20.0.26", {"start": v(40.07, -9.44) * mm, "end": v(36.44, -9.44) * mm});
            skLineSegment(sketch, "E17.20.0.27", {"start": v(36.44, -22.07) * mm, "end": v(36.44, -18.44) * mm});
            skLineSegment(sketch, "E17.20.0.28", {"start": v(36.44, 13.93) * mm, "end": v(36.44, 17.56) * mm});
            skLineSegment(sketch, "E17.20.0.29", {"start": v(36.44, -4.07) * mm, "end": v(36.44, -0.44) * mm});
            skLineSegment(sketch, "E17.20.0.30", {"start": v(40.07, 13.93) * mm, "end": v(36.44, 13.93) * mm});
            skLineSegment(sketch, "E17.20.0.31", {"start": v(40.07, -4.07) * mm, "end": v(36.44, -4.07) * mm});
            skLineSegment(sketch, "E17.20.0.32", {"start": v(40.07, -17.57) * mm, "end": v(36.44, -17.57) * mm});
            skLineSegment(sketch, "E17.20.0.33", {"start": v(40.07, -27.44) * mm, "end": v(36.44, -27.44) * mm});
            skLineSegment(sketch, "E17.20.0.34", {"start": v(40.07, -35.57) * mm, "end": v(36.44, -35.57) * mm});
            skLineSegment(sketch, "E17.20.0.35", {"start": v(40.07, 0.43) * mm, "end": v(36.44, 0.43) * mm});
            skLineSegment(sketch, "E17.20.0.36", {"start": v(40.07, 13.93) * mm, "end": v(40.07, 17.56) * mm});
            skLineSegment(sketch, "E17.20.0.37", {"start": v(40.07, -22.07) * mm, "end": v(40.07, -18.44) * mm});
            skLineSegment(sketch, "E17.20.0.38", {"start": v(40.07, -17.57) * mm, "end": v(40.07, -13.94) * mm});
            skLineSegment(sketch, "E17.20.0.39", {"start": v(36.44, 4.93) * mm, "end": v(36.44, 8.56) * mm});
            skLineSegment(sketch, "E17.20.0.40", {"start": v(40.07, 26.56) * mm, "end": v(36.44, 26.56) * mm});
            skLineSegment(sketch, "E17.20.0.41", {"start": v(40.07, 9.43) * mm, "end": v(36.44, 9.43) * mm});
            skLineSegment(sketch, "E17.20.0.42", {"start": v(36.44, 22.93) * mm, "end": v(36.44, 26.56) * mm});
            skLineSegment(sketch, "E17.20.0.43", {"start": v(40.07, -13.94) * mm, "end": v(36.44, -13.94) * mm});
            skLineSegment(sketch, "E17.20.0.44", {"start": v(40.07, -31.94) * mm, "end": v(36.44, -31.94) * mm});
            skLineSegment(sketch, "E17.20.0.45", {"start": v(40.07, 22.06) * mm, "end": v(36.44, 22.06) * mm});
            skLineSegment(sketch, "E17.20.0.46", {"start": v(40.07, 4.06) * mm, "end": v(36.44, 4.06) * mm});
            skLineSegment(sketch, "E17.20.0.47", {"start": v(36.44, 0.43) * mm, "end": v(36.44, 4.06) * mm});
            skLineSegment(sketch, "E17.20.0.48", {"start": v(36.44, -35.57) * mm, "end": v(36.44, -31.94) * mm});
            skLineSegment(sketch, "E17.20.0.49", {"start": v(40.07, 0.43) * mm, "end": v(40.07, 4.06) * mm});
            skLineSegment(sketch, "E17.20.0.50", {"start": v(40.07, -26.57) * mm, "end": v(36.44, -26.57) * mm});
            skLineSegment(sketch, "E17.20.0.51", {"start": v(40.07, -35.57) * mm, "end": v(40.07, -31.94) * mm});
            skLineSegment(sketch, "E17.20.0.52", {"start": v(40.07, -4.07) * mm, "end": v(40.07, -0.44) * mm});
            skLineSegment(sketch, "E17.20.0.53", {"start": v(40.07, -22.07) * mm, "end": v(36.44, -22.07) * mm});
            skLineSegment(sketch, "E17.20.0.54", {"start": v(40.07, 18.43) * mm, "end": v(40.07, 22.06) * mm});
            skLineSegment(sketch, "E17.20.0.55", {"start": v(40.07, -18.44) * mm, "end": v(36.44, -18.44) * mm});
            skLineSegment(sketch, "E17.20.0.56", {"start": v(40.07, -8.57) * mm, "end": v(40.07, -4.94) * mm});
            skLineSegment(sketch, "E17.20.0.57", {"start": v(40.07, 18.43) * mm, "end": v(36.44, 18.43) * mm});
            skLineSegment(sketch, "E17.20.0.58", {"start": v(40.07, 35.56) * mm, "end": v(36.44, 35.56) * mm});
            skLineSegment(sketch, "E17.20.0.59", {"start": v(40.07, 4.93) * mm, "end": v(40.07, 8.56) * mm});
            skLineSegment(sketch, "E17.20.0.60", {"start": v(40.07, 27.43) * mm, "end": v(36.44, 27.43) * mm});
            skLineSegment(sketch, "E17.20.0.61", {"start": v(40.07, -8.57) * mm, "end": v(36.44, -8.57) * mm});
            skLineSegment(sketch, "E17.20.0.62", {"start": v(40.07, 8.56) * mm, "end": v(36.44, 8.56) * mm});
            skLineSegment(sketch, "E17.20.0.63", {"start": v(36.44, -17.57) * mm, "end": v(36.44, -13.94) * mm});
            skLineSegment(sketch, "E17.20.0.64", {"start": v(40.07, 22.93) * mm, "end": v(36.44, 22.93) * mm});
            skLineSegment(sketch, "E17.20.0.65", {"start": v(40.07, 22.93) * mm, "end": v(40.07, 26.56) * mm});
            skLineSegment(sketch, "E17.21.0.0", {"start": v(40.94, 27.43) * mm, "end": v(40.94, 31.06) * mm});
            skLineSegment(sketch, "E17.21.0.1", {"start": v(44.57, 27.43) * mm, "end": v(44.57, 31.06) * mm});
            skLineSegment(sketch, "E17.21.0.2", {"start": v(44.57, -13.07) * mm, "end": v(44.57, -9.44) * mm});
            skLineSegment(sketch, "E17.21.0.3", {"start": v(40.94, 9.43) * mm, "end": v(40.94, 13.06) * mm});
            skLineSegment(sketch, "E17.21.0.4", {"start": v(40.94, -13.07) * mm, "end": v(40.94, -9.44) * mm});
            skLineSegment(sketch, "E17.21.0.5", {"start": v(40.94, -31.07) * mm, "end": v(40.94, -27.44) * mm});
            skPoint(sketch, "E17.21.0.6", {"position": v(42.75, 33.75) * mm});
            skLineSegment(sketch, "E17.21.0.7", {"start": v(44.57, 9.43) * mm, "end": v(44.57, 13.06) * mm});
            skLineSegment(sketch, "E17.21.0.8", {"start": v(44.57, -31.07) * mm, "end": v(44.57, -27.44) * mm});
            skLineSegment(sketch, "E17.21.0.9", {"start": v(44.57, 31.93) * mm, "end": v(44.57, 27.43) * mm, "construction": true});
            skLineSegment(sketch, "E17.21.0.10", {"start": v(44.57, 31.06) * mm, "end": v(40.94, 31.06) * mm});
            skLineSegment(sketch, "E17.21.0.11", {"start": v(44.57, 4.93) * mm, "end": v(40.94, 4.93) * mm});
            skLineSegment(sketch, "E17.21.0.12", {"start": v(44.57, -13.07) * mm, "end": v(40.94, -13.07) * mm});
            skLineSegment(sketch, "E17.21.0.13", {"start": v(44.57, -31.07) * mm, "end": v(40.94, -31.07) * mm});
            skLineSegment(sketch, "E17.21.0.14", {"start": v(40.94, 31.93) * mm, "end": v(40.94, 35.56) * mm});
            skLineSegment(sketch, "E17.21.0.15", {"start": v(44.57, 31.93) * mm, "end": v(44.57, 35.56) * mm});
            skLineSegment(sketch, "E17.21.0.16", {"start": v(44.57, 31.93) * mm, "end": v(40.94, 31.93) * mm});
            skLineSegment(sketch, "E17.21.0.17", {"start": v(40.94, 18.43) * mm, "end": v(40.94, 22.06) * mm});
            skLineSegment(sketch, "E17.21.0.18", {"start": v(44.57, 13.06) * mm, "end": v(40.94, 13.06) * mm});
            skLineSegment(sketch, "E17.21.0.19", {"start": v(44.57, -4.94) * mm, "end": v(40.94, -4.94) * mm});
            skLineSegment(sketch, "E17.21.0.20", {"start": v(44.57, -22.94) * mm, "end": v(40.94, -22.94) * mm});
            skLineSegment(sketch, "E17.21.0.21", {"start": v(44.57, -26.57) * mm, "end": v(44.57, -22.94) * mm});
            skLineSegment(sketch, "E17.21.0.22", {"start": v(40.94, -8.57) * mm, "end": v(40.94, -4.94) * mm});
            skLineSegment(sketch, "E17.21.0.23", {"start": v(40.94, -26.57) * mm, "end": v(40.94, -22.94) * mm});
            skLineSegment(sketch, "E17.21.0.24", {"start": v(44.57, 17.56) * mm, "end": v(40.94, 17.56) * mm});
            skLineSegment(sketch, "E17.21.0.25", {"start": v(44.57, -0.44) * mm, "end": v(40.94, -0.44) * mm});
            skLineSegment(sketch, "E17.21.0.26", {"start": v(44.57, -9.44) * mm, "end": v(40.94, -9.44) * mm});
            skLineSegment(sketch, "E17.21.0.27", {"start": v(40.94, -22.07) * mm, "end": v(40.94, -18.44) * mm});
            skLineSegment(sketch, "E17.21.0.28", {"start": v(40.94, 13.93) * mm, "end": v(40.94, 17.56) * mm});
            skLineSegment(sketch, "E17.21.0.29", {"start": v(40.94, -4.07) * mm, "end": v(40.94, -0.44) * mm});
            skLineSegment(sketch, "E17.21.0.30", {"start": v(44.57, 13.93) * mm, "end": v(40.94, 13.93) * mm});
            skLineSegment(sketch, "E17.21.0.31", {"start": v(44.57, -4.07) * mm, "end": v(40.94, -4.07) * mm});
            skLineSegment(sketch, "E17.21.0.32", {"start": v(44.57, -17.57) * mm, "end": v(40.94, -17.57) * mm});
            skLineSegment(sketch, "E17.21.0.33", {"start": v(44.57, -27.44) * mm, "end": v(40.94, -27.44) * mm});
            skLineSegment(sketch, "E17.21.0.34", {"start": v(44.57, -35.57) * mm, "end": v(40.94, -35.57) * mm});
            skLineSegment(sketch, "E17.21.0.35", {"start": v(44.57, 0.43) * mm, "end": v(40.94, 0.43) * mm});
            skLineSegment(sketch, "E17.21.0.36", {"start": v(44.57, 13.93) * mm, "end": v(44.57, 17.56) * mm});
            skLineSegment(sketch, "E17.21.0.37", {"start": v(44.57, -22.07) * mm, "end": v(44.57, -18.44) * mm});
            skLineSegment(sketch, "E17.21.0.38", {"start": v(44.57, -17.57) * mm, "end": v(44.57, -13.94) * mm});
            skLineSegment(sketch, "E17.21.0.39", {"start": v(40.94, 4.93) * mm, "end": v(40.94, 8.56) * mm});
            skLineSegment(sketch, "E17.21.0.40", {"start": v(44.57, 26.56) * mm, "end": v(40.94, 26.56) * mm});
            skLineSegment(sketch, "E17.21.0.41", {"start": v(44.57, 9.43) * mm, "end": v(40.94, 9.43) * mm});
            skLineSegment(sketch, "E17.21.0.42", {"start": v(40.94, 22.93) * mm, "end": v(40.94, 26.56) * mm});
            skLineSegment(sketch, "E17.21.0.43", {"start": v(44.57, -13.94) * mm, "end": v(40.94, -13.94) * mm});
            skLineSegment(sketch, "E17.21.0.44", {"start": v(44.57, -31.94) * mm, "end": v(40.94, -31.94) * mm});
            skLineSegment(sketch, "E17.21.0.45", {"start": v(44.57, 22.06) * mm, "end": v(40.94, 22.06) * mm});
            skLineSegment(sketch, "E17.21.0.46", {"start": v(44.57, 4.06) * mm, "end": v(40.94, 4.06) * mm});
            skLineSegment(sketch, "E17.21.0.47", {"start": v(40.94, 0.43) * mm, "end": v(40.94, 4.06) * mm});
            skLineSegment(sketch, "E17.21.0.48", {"start": v(40.94, -35.57) * mm, "end": v(40.94, -31.94) * mm});
            skLineSegment(sketch, "E17.21.0.49", {"start": v(44.57, 0.43) * mm, "end": v(44.57, 4.06) * mm});
            skLineSegment(sketch, "E17.21.0.50", {"start": v(44.57, -26.57) * mm, "end": v(40.94, -26.57) * mm});
            skLineSegment(sketch, "E17.21.0.51", {"start": v(44.57, -35.57) * mm, "end": v(44.57, -31.94) * mm});
            skLineSegment(sketch, "E17.21.0.52", {"start": v(44.57, -4.07) * mm, "end": v(44.57, -0.44) * mm});
            skLineSegment(sketch, "E17.21.0.53", {"start": v(44.57, -22.07) * mm, "end": v(40.94, -22.07) * mm});
            skLineSegment(sketch, "E17.21.0.54", {"start": v(44.57, 18.43) * mm, "end": v(44.57, 22.06) * mm});
            skLineSegment(sketch, "E17.21.0.55", {"start": v(44.57, -18.44) * mm, "end": v(40.94, -18.44) * mm});
            skLineSegment(sketch, "E17.21.0.56", {"start": v(44.57, -8.57) * mm, "end": v(44.57, -4.94) * mm});
            skLineSegment(sketch, "E17.21.0.57", {"start": v(44.57, 18.43) * mm, "end": v(40.94, 18.43) * mm});
            skLineSegment(sketch, "E17.21.0.58", {"start": v(44.57, 35.56) * mm, "end": v(40.94, 35.56) * mm});
            skLineSegment(sketch, "E17.21.0.59", {"start": v(44.57, 4.93) * mm, "end": v(44.57, 8.56) * mm});
            skLineSegment(sketch, "E17.21.0.60", {"start": v(44.57, 27.43) * mm, "end": v(40.94, 27.43) * mm});
            skLineSegment(sketch, "E17.21.0.61", {"start": v(44.57, -8.57) * mm, "end": v(40.94, -8.57) * mm});
            skLineSegment(sketch, "E17.21.0.62", {"start": v(44.57, 8.56) * mm, "end": v(40.94, 8.56) * mm});
            skLineSegment(sketch, "E17.21.0.63", {"start": v(40.94, -17.57) * mm, "end": v(40.94, -13.94) * mm});
            skLineSegment(sketch, "E17.21.0.64", {"start": v(44.57, 22.93) * mm, "end": v(40.94, 22.93) * mm});
            skLineSegment(sketch, "E17.21.0.65", {"start": v(44.57, 22.93) * mm, "end": v(44.57, 26.56) * mm});
            skLineSegment(sketch, "E17.22.0.0", {"start": v(45.44, 27.43) * mm, "end": v(45.44, 31.06) * mm});
            skLineSegment(sketch, "E17.22.0.1", {"start": v(49.07, 27.43) * mm, "end": v(49.07, 31.06) * mm});
            skLineSegment(sketch, "E17.22.0.2", {"start": v(49.07, -13.07) * mm, "end": v(49.07, -9.44) * mm});
            skLineSegment(sketch, "E17.22.0.3", {"start": v(45.44, 9.43) * mm, "end": v(45.44, 13.06) * mm});
            skLineSegment(sketch, "E17.22.0.4", {"start": v(45.44, -13.07) * mm, "end": v(45.44, -9.44) * mm});
            skLineSegment(sketch, "E17.22.0.5", {"start": v(45.44, -31.07) * mm, "end": v(45.44, -27.44) * mm});
            skPoint(sketch, "E17.22.0.6", {"position": v(47.25, 33.75) * mm});
            skLineSegment(sketch, "E17.22.0.7", {"start": v(49.07, 9.43) * mm, "end": v(49.07, 13.06) * mm});
            skLineSegment(sketch, "E17.22.0.8", {"start": v(49.07, -31.07) * mm, "end": v(49.07, -27.44) * mm});
            skLineSegment(sketch, "E17.22.0.9", {"start": v(49.07, 31.93) * mm, "end": v(49.07, 27.43) * mm, "construction": true});
            skLineSegment(sketch, "E17.22.0.10", {"start": v(49.07, 31.06) * mm, "end": v(45.44, 31.06) * mm});
            skLineSegment(sketch, "E17.22.0.11", {"start": v(49.07, 4.93) * mm, "end": v(45.44, 4.93) * mm});
            skLineSegment(sketch, "E17.22.0.12", {"start": v(49.07, -13.07) * mm, "end": v(45.44, -13.07) * mm});
            skLineSegment(sketch, "E17.22.0.13", {"start": v(49.07, -31.07) * mm, "end": v(45.44, -31.07) * mm});
            skLineSegment(sketch, "E17.22.0.14", {"start": v(45.44, 31.93) * mm, "end": v(45.44, 35.56) * mm});
            skLineSegment(sketch, "E17.22.0.15", {"start": v(49.07, 31.93) * mm, "end": v(49.07, 35.56) * mm});
            skLineSegment(sketch, "E17.22.0.16", {"start": v(49.07, 31.93) * mm, "end": v(45.44, 31.93) * mm});
            skLineSegment(sketch, "E17.22.0.17", {"start": v(45.44, 18.43) * mm, "end": v(45.44, 22.06) * mm});
            skLineSegment(sketch, "E17.22.0.18", {"start": v(49.07, 13.06) * mm, "end": v(45.44, 13.06) * mm});
            skLineSegment(sketch, "E17.22.0.19", {"start": v(49.07, -4.94) * mm, "end": v(45.44, -4.94) * mm});
            skLineSegment(sketch, "E17.22.0.20", {"start": v(49.07, -22.94) * mm, "end": v(45.44, -22.94) * mm});
            skLineSegment(sketch, "E17.22.0.21", {"start": v(49.07, -26.57) * mm, "end": v(49.07, -22.94) * mm});
            skLineSegment(sketch, "E17.22.0.22", {"start": v(45.44, -8.57) * mm, "end": v(45.44, -4.94) * mm});
            skLineSegment(sketch, "E17.22.0.23", {"start": v(45.44, -26.57) * mm, "end": v(45.44, -22.94) * mm});
            skLineSegment(sketch, "E17.22.0.24", {"start": v(49.07, 17.56) * mm, "end": v(45.44, 17.56) * mm});
            skLineSegment(sketch, "E17.22.0.25", {"start": v(49.07, -0.44) * mm, "end": v(45.44, -0.44) * mm});
            skLineSegment(sketch, "E17.22.0.26", {"start": v(49.07, -9.44) * mm, "end": v(45.44, -9.44) * mm});
            skLineSegment(sketch, "E17.22.0.27", {"start": v(45.44, -22.07) * mm, "end": v(45.44, -18.44) * mm});
            skLineSegment(sketch, "E17.22.0.28", {"start": v(45.44, 13.93) * mm, "end": v(45.44, 17.56) * mm});
            skLineSegment(sketch, "E17.22.0.29", {"start": v(45.44, -4.07) * mm, "end": v(45.44, -0.44) * mm});
            skLineSegment(sketch, "E17.22.0.30", {"start": v(49.07, 13.93) * mm, "end": v(45.44, 13.93) * mm});
            skLineSegment(sketch, "E17.22.0.31", {"start": v(49.07, -4.07) * mm, "end": v(45.44, -4.07) * mm});
            skLineSegment(sketch, "E17.22.0.32", {"start": v(49.07, -17.57) * mm, "end": v(45.44, -17.57) * mm});
            skLineSegment(sketch, "E17.22.0.33", {"start": v(49.07, -27.44) * mm, "end": v(45.44, -27.44) * mm});
            skLineSegment(sketch, "E17.22.0.34", {"start": v(49.07, -35.57) * mm, "end": v(45.44, -35.57) * mm});
            skLineSegment(sketch, "E17.22.0.35", {"start": v(49.07, 0.43) * mm, "end": v(45.44, 0.43) * mm});
            skLineSegment(sketch, "E17.22.0.36", {"start": v(49.07, 13.93) * mm, "end": v(49.07, 17.56) * mm});
            skLineSegment(sketch, "E17.22.0.37", {"start": v(49.07, -22.07) * mm, "end": v(49.07, -18.44) * mm});
            skLineSegment(sketch, "E17.22.0.38", {"start": v(49.07, -17.57) * mm, "end": v(49.07, -13.94) * mm});
            skLineSegment(sketch, "E17.22.0.39", {"start": v(45.44, 4.93) * mm, "end": v(45.44, 8.56) * mm});
            skLineSegment(sketch, "E17.22.0.40", {"start": v(49.07, 26.56) * mm, "end": v(45.44, 26.56) * mm});
            skLineSegment(sketch, "E17.22.0.41", {"start": v(49.07, 9.43) * mm, "end": v(45.44, 9.43) * mm});
            skLineSegment(sketch, "E17.22.0.42", {"start": v(45.44, 22.93) * mm, "end": v(45.44, 26.56) * mm});
            skLineSegment(sketch, "E17.22.0.43", {"start": v(49.07, -13.94) * mm, "end": v(45.44, -13.94) * mm});
            skLineSegment(sketch, "E17.22.0.44", {"start": v(49.07, -31.94) * mm, "end": v(45.44, -31.94) * mm});
            skLineSegment(sketch, "E17.22.0.45", {"start": v(49.07, 22.06) * mm, "end": v(45.44, 22.06) * mm});
            skLineSegment(sketch, "E17.22.0.46", {"start": v(49.07, 4.06) * mm, "end": v(45.44, 4.06) * mm});
            skLineSegment(sketch, "E17.22.0.47", {"start": v(45.44, 0.43) * mm, "end": v(45.44, 4.06) * mm});
            skLineSegment(sketch, "E17.22.0.48", {"start": v(45.44, -35.57) * mm, "end": v(45.44, -31.94) * mm});
            skLineSegment(sketch, "E17.22.0.49", {"start": v(49.07, 0.43) * mm, "end": v(49.07, 4.06) * mm});
            skLineSegment(sketch, "E17.22.0.50", {"start": v(49.07, -26.57) * mm, "end": v(45.44, -26.57) * mm});
            skLineSegment(sketch, "E17.22.0.51", {"start": v(49.07, -35.57) * mm, "end": v(49.07, -31.94) * mm});
            skLineSegment(sketch, "E17.22.0.52", {"start": v(49.07, -4.07) * mm, "end": v(49.07, -0.44) * mm});
            skLineSegment(sketch, "E17.22.0.53", {"start": v(49.07, -22.07) * mm, "end": v(45.44, -22.07) * mm});
            skLineSegment(sketch, "E17.22.0.54", {"start": v(49.07, 18.43) * mm, "end": v(49.07, 22.06) * mm});
            skLineSegment(sketch, "E17.22.0.55", {"start": v(49.07, -18.44) * mm, "end": v(45.44, -18.44) * mm});
            skLineSegment(sketch, "E17.22.0.56", {"start": v(49.07, -8.57) * mm, "end": v(49.07, -4.94) * mm});
            skLineSegment(sketch, "E17.22.0.57", {"start": v(49.07, 18.43) * mm, "end": v(45.44, 18.43) * mm});
            skLineSegment(sketch, "E17.22.0.58", {"start": v(49.07, 35.56) * mm, "end": v(45.44, 35.56) * mm});
            skLineSegment(sketch, "E17.22.0.59", {"start": v(49.07, 4.93) * mm, "end": v(49.07, 8.56) * mm});
            skLineSegment(sketch, "E17.22.0.60", {"start": v(49.07, 27.43) * mm, "end": v(45.44, 27.43) * mm});
            skLineSegment(sketch, "E17.22.0.61", {"start": v(49.07, -8.57) * mm, "end": v(45.44, -8.57) * mm});
            skLineSegment(sketch, "E17.22.0.62", {"start": v(49.07, 8.56) * mm, "end": v(45.44, 8.56) * mm});
            skLineSegment(sketch, "E17.22.0.63", {"start": v(45.44, -17.57) * mm, "end": v(45.44, -13.94) * mm});
            skLineSegment(sketch, "E17.22.0.64", {"start": v(49.07, 22.93) * mm, "end": v(45.44, 22.93) * mm});
            skLineSegment(sketch, "E17.22.0.65", {"start": v(49.07, 22.93) * mm, "end": v(49.07, 26.56) * mm});
            skLineSegment(sketch, "E17.23.0.0", {"start": v(49.94, 27.43) * mm, "end": v(49.94, 31.06) * mm});
            skLineSegment(sketch, "E17.23.0.1", {"start": v(53.57, 27.43) * mm, "end": v(53.57, 31.06) * mm});
            skLineSegment(sketch, "E17.23.0.2", {"start": v(53.57, -13.07) * mm, "end": v(53.57, -9.44) * mm});
            skLineSegment(sketch, "E17.23.0.3", {"start": v(49.94, 9.43) * mm, "end": v(49.94, 13.06) * mm});
            skLineSegment(sketch, "E17.23.0.4", {"start": v(49.94, -13.07) * mm, "end": v(49.94, -9.44) * mm});
            skLineSegment(sketch, "E17.23.0.5", {"start": v(49.94, -31.07) * mm, "end": v(49.94, -27.44) * mm});
            skPoint(sketch, "E17.23.0.6", {"position": v(51.75, 33.75) * mm});
            skLineSegment(sketch, "E17.23.0.7", {"start": v(53.57, 9.43) * mm, "end": v(53.57, 13.06) * mm});
            skLineSegment(sketch, "E17.23.0.8", {"start": v(53.57, -31.07) * mm, "end": v(53.57, -27.44) * mm});
            skLineSegment(sketch, "E17.23.0.9", {"start": v(53.57, 31.93) * mm, "end": v(53.57, 27.43) * mm, "construction": true});
            skLineSegment(sketch, "E17.23.0.10", {"start": v(53.57, 31.06) * mm, "end": v(49.94, 31.06) * mm});
            skLineSegment(sketch, "E17.23.0.11", {"start": v(53.57, 4.93) * mm, "end": v(49.94, 4.93) * mm});
            skLineSegment(sketch, "E17.23.0.12", {"start": v(53.57, -13.07) * mm, "end": v(49.94, -13.07) * mm});
            skLineSegment(sketch, "E17.23.0.13", {"start": v(53.57, -31.07) * mm, "end": v(49.94, -31.07) * mm});
            skLineSegment(sketch, "E17.23.0.14", {"start": v(49.94, 31.93) * mm, "end": v(49.94, 35.56) * mm});
            skLineSegment(sketch, "E17.23.0.15", {"start": v(53.57, 31.93) * mm, "end": v(53.57, 35.56) * mm});
            skLineSegment(sketch, "E17.23.0.16", {"start": v(53.57, 31.93) * mm, "end": v(49.94, 31.93) * mm});
            skLineSegment(sketch, "E17.23.0.17", {"start": v(49.94, 18.43) * mm, "end": v(49.94, 22.06) * mm});
            skLineSegment(sketch, "E17.23.0.18", {"start": v(53.57, 13.06) * mm, "end": v(49.94, 13.06) * mm});
            skLineSegment(sketch, "E17.23.0.19", {"start": v(53.57, -4.94) * mm, "end": v(49.94, -4.94) * mm});
            skLineSegment(sketch, "E17.23.0.20", {"start": v(53.57, -22.94) * mm, "end": v(49.94, -22.94) * mm});
            skLineSegment(sketch, "E17.23.0.21", {"start": v(53.57, -26.57) * mm, "end": v(53.57, -22.94) * mm});
            skLineSegment(sketch, "E17.23.0.22", {"start": v(49.94, -8.57) * mm, "end": v(49.94, -4.94) * mm});
            skLineSegment(sketch, "E17.23.0.23", {"start": v(49.94, -26.57) * mm, "end": v(49.94, -22.94) * mm});
            skLineSegment(sketch, "E17.23.0.24", {"start": v(53.57, 17.56) * mm, "end": v(49.94, 17.56) * mm});
            skLineSegment(sketch, "E17.23.0.25", {"start": v(53.57, -0.44) * mm, "end": v(49.94, -0.44) * mm});
            skLineSegment(sketch, "E17.23.0.26", {"start": v(53.57, -9.44) * mm, "end": v(49.94, -9.44) * mm});
            skLineSegment(sketch, "E17.23.0.27", {"start": v(49.94, -22.07) * mm, "end": v(49.94, -18.44) * mm});
            skLineSegment(sketch, "E17.23.0.28", {"start": v(49.94, 13.93) * mm, "end": v(49.94, 17.56) * mm});
            skLineSegment(sketch, "E17.23.0.29", {"start": v(49.94, -4.07) * mm, "end": v(49.94, -0.44) * mm});
            skLineSegment(sketch, "E17.23.0.30", {"start": v(53.57, 13.93) * mm, "end": v(49.94, 13.93) * mm});
            skLineSegment(sketch, "E17.23.0.31", {"start": v(53.57, -4.07) * mm, "end": v(49.94, -4.07) * mm});
            skLineSegment(sketch, "E17.23.0.32", {"start": v(53.57, -17.57) * mm, "end": v(49.94, -17.57) * mm});
            skLineSegment(sketch, "E17.23.0.33", {"start": v(53.57, -27.44) * mm, "end": v(49.94, -27.44) * mm});
            skLineSegment(sketch, "E17.23.0.34", {"start": v(53.57, -35.57) * mm, "end": v(49.94, -35.57) * mm});
            skLineSegment(sketch, "E17.23.0.35", {"start": v(53.57, 0.43) * mm, "end": v(49.94, 0.43) * mm});
            skLineSegment(sketch, "E17.23.0.36", {"start": v(53.57, 13.93) * mm, "end": v(53.57, 17.56) * mm});
            skLineSegment(sketch, "E17.23.0.37", {"start": v(53.57, -22.07) * mm, "end": v(53.57, -18.44) * mm});
            skLineSegment(sketch, "E17.23.0.38", {"start": v(53.57, -17.57) * mm, "end": v(53.57, -13.94) * mm});
            skLineSegment(sketch, "E17.23.0.39", {"start": v(49.94, 4.93) * mm, "end": v(49.94, 8.56) * mm});
            skLineSegment(sketch, "E17.23.0.40", {"start": v(53.57, 26.56) * mm, "end": v(49.94, 26.56) * mm});
            skLineSegment(sketch, "E17.23.0.41", {"start": v(53.57, 9.43) * mm, "end": v(49.94, 9.43) * mm});
            skLineSegment(sketch, "E17.23.0.42", {"start": v(49.94, 22.93) * mm, "end": v(49.94, 26.56) * mm});
            skLineSegment(sketch, "E17.23.0.43", {"start": v(53.57, -13.94) * mm, "end": v(49.94, -13.94) * mm});
            skLineSegment(sketch, "E17.23.0.44", {"start": v(53.57, -31.94) * mm, "end": v(49.94, -31.94) * mm});
            skLineSegment(sketch, "E17.23.0.45", {"start": v(53.57, 22.06) * mm, "end": v(49.94, 22.06) * mm});
            skLineSegment(sketch, "E17.23.0.46", {"start": v(53.57, 4.06) * mm, "end": v(49.94, 4.06) * mm});
            skLineSegment(sketch, "E17.23.0.47", {"start": v(49.94, 0.43) * mm, "end": v(49.94, 4.06) * mm});
            skLineSegment(sketch, "E17.23.0.48", {"start": v(49.94, -35.57) * mm, "end": v(49.94, -31.94) * mm});
            skLineSegment(sketch, "E17.23.0.49", {"start": v(53.57, 0.43) * mm, "end": v(53.57, 4.06) * mm});
            skLineSegment(sketch, "E17.23.0.50", {"start": v(53.57, -26.57) * mm, "end": v(49.94, -26.57) * mm});
            skLineSegment(sketch, "E17.23.0.51", {"start": v(53.57, -35.57) * mm, "end": v(53.57, -31.94) * mm});
            skLineSegment(sketch, "E17.23.0.52", {"start": v(53.57, -4.07) * mm, "end": v(53.57, -0.44) * mm});
            skLineSegment(sketch, "E17.23.0.53", {"start": v(53.57, -22.07) * mm, "end": v(49.94, -22.07) * mm});
            skLineSegment(sketch, "E17.23.0.54", {"start": v(53.57, 18.43) * mm, "end": v(53.57, 22.06) * mm});
            skLineSegment(sketch, "E17.23.0.55", {"start": v(53.57, -18.44) * mm, "end": v(49.94, -18.44) * mm});
            skLineSegment(sketch, "E17.23.0.56", {"start": v(53.57, -8.57) * mm, "end": v(53.57, -4.94) * mm});
            skLineSegment(sketch, "E17.23.0.57", {"start": v(53.57, 18.43) * mm, "end": v(49.94, 18.43) * mm});
            skLineSegment(sketch, "E17.23.0.58", {"start": v(53.57, 35.56) * mm, "end": v(49.94, 35.56) * mm});
            skLineSegment(sketch, "E17.23.0.59", {"start": v(53.57, 4.93) * mm, "end": v(53.57, 8.56) * mm});
            skLineSegment(sketch, "E17.23.0.60", {"start": v(53.57, 27.43) * mm, "end": v(49.94, 27.43) * mm});
            skLineSegment(sketch, "E17.23.0.61", {"start": v(53.57, -8.57) * mm, "end": v(49.94, -8.57) * mm});
            skLineSegment(sketch, "E17.23.0.62", {"start": v(53.57, 8.56) * mm, "end": v(49.94, 8.56) * mm});
            skLineSegment(sketch, "E17.23.0.63", {"start": v(49.94, -17.57) * mm, "end": v(49.94, -13.94) * mm});
            skLineSegment(sketch, "E17.23.0.64", {"start": v(53.57, 22.93) * mm, "end": v(49.94, 22.93) * mm});
            skLineSegment(sketch, "E17.23.0.65", {"start": v(53.57, 22.93) * mm, "end": v(53.57, 26.56) * mm});
            skLineSegment(sketch, "E17.direction1", {"start": v(-53.57, 27.43) * mm, "end": v(-49.07, 27.43) * mm, "construction": true});
            skSolve(sketch);
        }
        {
            var Q0;
            Q0 = qSketchRegion(id + "F4", true);
            extrude(context, id + "F5", {"entities" : qUnion([Q0]), "operationType" : NewBodyOperationType.REMOVE, "oppositeDirection" : true, "depth" : 12.54 * mm});
        }
    });
